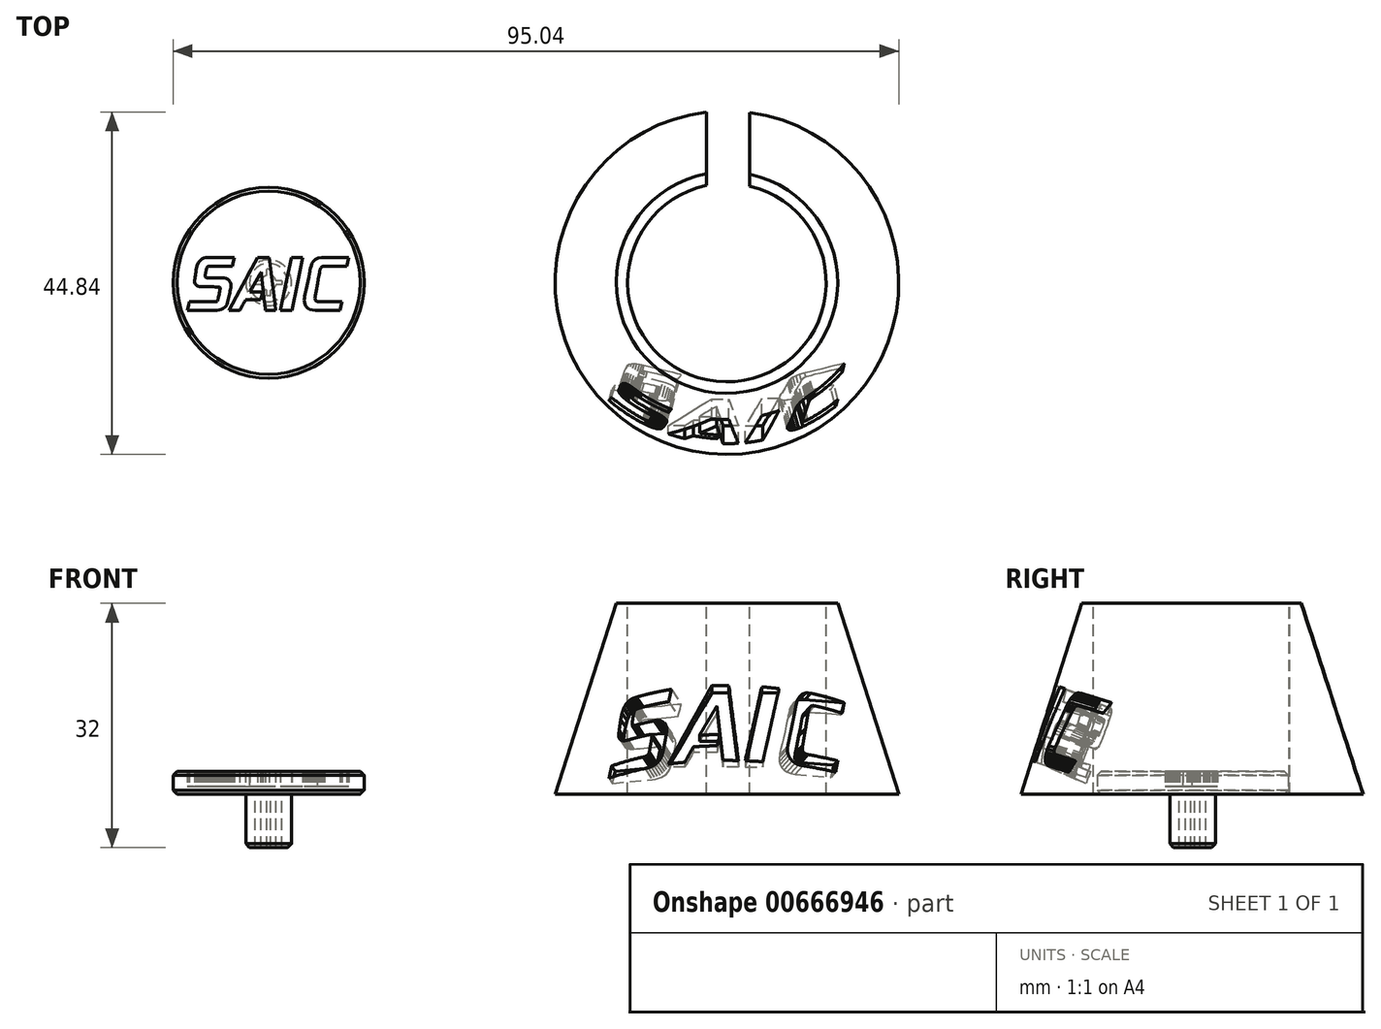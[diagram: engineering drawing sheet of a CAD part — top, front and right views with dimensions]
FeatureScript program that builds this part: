
annotation { "Feature Type Name" : "Feature", "Feature Type Description" : "" }
export const myFeature = defineFeature(function(context is Context, id is Id, definition is map)
    precondition{}
    {
        {
            var Q0;
            Q0=qCreatedBy(makeId("Top.planeOp"),FACE);
            var sketch = newSketch(context, id + "F0", { "sketchPlane" : qUnion([Q0])});
            skCircle(sketch, "E0", {"center": v(0, 0) * mm, "radius": 22.5 * mm});
            skSolve(sketch);
        }
        {
            var Q0;
            Q0=qCreatedBy(makeId("Top.planeOp"),FACE);
            cPlane(context, id + "F1", {"entities" : qUnion([Q0]), "cplaneType" : CPlaneType.OFFSET, "offset" : 25 * mm, "width" : 150 * mm, "height" : 150 * mm});
        }
        {
            var Q0;
            Q0=qCreatedBy(id+"F1.planeOp",FACE);
            var sketch = newSketch(context, id + "F2", { "sketchPlane" : qUnion([Q0])});
            skCircle(sketch, "E1", {"center": v(0, 0) * mm, "radius": 14.5 * mm});
            skSolve(sketch);
        }
        {
            var Q0;
            Q0=makeQuery(id+"F2.imprint","IMPRINT",FACE,{"disambiguationData":[TD([[makeQuery(id+"F2.imprint","IMPRINT",EDGE,{"derivedFrom":sQuery(id+"F2.wireOp",EDGE,"E1")}),1.0]])]});
            var Q1;
            Q1=makeQuery(id+"F0.imprint","IMPRINT",FACE,{"disambiguationData":[TD([[makeQuery(id+"F0.imprint","IMPRINT",EDGE,{"derivedFrom":sQuery(id+"F0.wireOp",EDGE,"E0")}),1.0]])]});
            loft(context, id + "F3", {"sheetProfilesArray" : [{ "sheetProfileEntities" : qUnion([Q0]) }, { "sheetProfileEntities" : qUnion([Q1]) }]});
        }
        {
            var Q0;
            Q0=qCreatedBy(id+"F1.planeOp",FACE);
            var sketch = newSketch(context, id + "F4", { "sketchPlane" : qUnion([Q0])});
            skCircle(sketch, "E2", {"center": v(0, 0) * mm, "radius": 13 * mm});
            skSolve(sketch);
        }
        {
            var Q0;
            Q0 = qSketchRegion(id + "F4", true);
            extrude(context, id + "F5", {"entities" : qUnion([Q0]), "operationType" : NewBodyOperationType.REMOVE, "oppositeDirection" : true, "depth" : 32.3 * mm, "offsetDistance" : 25 * mm});
        }
        {
            var Q0;
            Q0=qCreatedBy(makeId("Top.planeOp"),FACE);
            var sketch = newSketch(context, id + "F6", { "sketchPlane" : qUnion([Q0])});
            skLineSegment(sketch, "E3.bottom", {"start": v(-2.67, 29.37) * mm, "end": v(2.99, 29.37) * mm});
            skLineSegment(sketch, "E3.top", {"start": v(-2.67, 0) * mm, "end": v(2.99, 0) * mm});
            skLineSegment(sketch, "E3.left", {"start": v(-2.67, 0) * mm, "end": v(-2.67, 29.37) * mm});
            skLineSegment(sketch, "E3.right", {"start": v(2.99, 0) * mm, "end": v(2.99, 29.37) * mm});
            skSolve(sketch);
        }
        {
            var Q0;
            Q0 = qSketchRegion(id + "F6", true);
            extrude(context, id + "F7", {"entities" : qUnion([Q0]), "operationType" : NewBodyOperationType.REMOVE, "depth" : 25 * mm, "offsetDistance" : 25 * mm});
        }
        {
            var Q0;
            Q0=qCreatedBy(makeId("Front.planeOp"),FACE);
            var sketch = newSketch(context, id + "F8", { "sketchPlane" : qUnion([Q0])});
            skLineSegment(sketch, "E4", {"start": v(33.86, 8.65) * mm, "end": v(33.95, 9.1) * mm});
            skLineSegment(sketch, "E5", {"start": v(33.95, 9.1) * mm, "end": v(34.07, 9.59) * mm});
            skLineSegment(sketch, "E6", {"start": v(34.07, 9.59) * mm, "end": v(34.25, 10.1) * mm});
            skLineSegment(sketch, "E7", {"start": v(34.25, 10.1) * mm, "end": v(34.5, 10.58) * mm});
            skLineSegment(sketch, "E8", {"start": v(34.5, 10.58) * mm, "end": v(34.88, 11.02) * mm});
            skLineSegment(sketch, "E9", {"start": v(34.88, 11.02) * mm, "end": v(35.38, 11.37) * mm});
            skLineSegment(sketch, "E10", {"start": v(35.38, 11.37) * mm, "end": v(36.04, 11.6) * mm});
            skLineSegment(sketch, "E11", {"start": v(36.04, 11.6) * mm, "end": v(36.88, 11.7) * mm});
            skLineSegment(sketch, "E12", {"start": v(36.88, 11.7) * mm, "end": v(37.88, 11.7) * mm});
            skLineSegment(sketch, "E13", {"start": v(37.88, 11.7) * mm, "end": v(39.7, 11.7) * mm});
            skLineSegment(sketch, "E14", {"start": v(39.7, 11.7) * mm, "end": v(42.05, 11.7) * mm});
            skLineSegment(sketch, "E15", {"start": v(42.05, 11.7) * mm, "end": v(44.63, 11.7) * mm});
            skLineSegment(sketch, "E16", {"start": v(44.63, 11.7) * mm, "end": v(47.15, 11.7) * mm});
            skLineSegment(sketch, "E17", {"start": v(47.15, 11.7) * mm, "end": v(49.32, 11.7) * mm});
            skLineSegment(sketch, "E18", {"start": v(49.32, 11.7) * mm, "end": v(50.83, 11.7) * mm});
            skLineSegment(sketch, "E19", {"start": v(50.83, 11.7) * mm, "end": v(51.4, 11.7) * mm});
            skLineSegment(sketch, "E20", {"start": v(51.4, 11.7) * mm, "end": v(51.57, 12.38) * mm});
            skLineSegment(sketch, "E21", {"start": v(51.57, 12.38) * mm, "end": v(51.73, 13.07) * mm});
            skLineSegment(sketch, "E22", {"start": v(51.73, 13.07) * mm, "end": v(51.9, 13.76) * mm});
            skLineSegment(sketch, "E23", {"start": v(51.9, 13.76) * mm, "end": v(52.07, 14.45) * mm});
            skLineSegment(sketch, "E24", {"start": v(52.07, 14.45) * mm, "end": v(52.23, 15.14) * mm});
            skLineSegment(sketch, "E25", {"start": v(52.23, 15.14) * mm, "end": v(52.4, 15.83) * mm});
            skLineSegment(sketch, "E26", {"start": v(52.4, 15.83) * mm, "end": v(52.56, 16.52) * mm});
            skLineSegment(sketch, "E27", {"start": v(52.56, 16.52) * mm, "end": v(52.73, 17.2) * mm});
            skLineSegment(sketch, "E28", {"start": v(52.73, 17.2) * mm, "end": v(52.16, 17.2) * mm});
            skLineSegment(sketch, "E29", {"start": v(52.16, 17.2) * mm, "end": v(50.64, 17.2) * mm});
            skLineSegment(sketch, "E30", {"start": v(50.64, 17.2) * mm, "end": v(48.4, 17.2) * mm});
            skLineSegment(sketch, "E31", {"start": v(48.4, 17.2) * mm, "end": v(45.68, 17.2) * mm});
            skLineSegment(sketch, "E32", {"start": v(45.68, 17.2) * mm, "end": v(42.74, 17.2) * mm});
            skLineSegment(sketch, "E33", {"start": v(42.74, 17.2) * mm, "end": v(39.81, 17.2) * mm});
            skLineSegment(sketch, "E34", {"start": v(39.81, 17.2) * mm, "end": v(37.15, 17.2) * mm});
            skLineSegment(sketch, "E35", {"start": v(37.15, 17.2) * mm, "end": v(35, 17.2) * mm});
            skLineSegment(sketch, "E36", {"start": v(35, 17.2) * mm, "end": v(32.75, 16.9) * mm});
            skLineSegment(sketch, "E37", {"start": v(32.75, 16.9) * mm, "end": v(31.02, 16.1) * mm});
            skLineSegment(sketch, "E38", {"start": v(31.02, 16.1) * mm, "end": v(29.74, 14.92) * mm});
            skLineSegment(sketch, "E39", {"start": v(29.74, 14.92) * mm, "end": v(28.83, 13.5) * mm});
            skLineSegment(sketch, "E40", {"start": v(28.83, 13.5) * mm, "end": v(28.2, 11.98) * mm});
            skLineSegment(sketch, "E41", {"start": v(28.2, 11.98) * mm, "end": v(27.81, 10.48) * mm});
            skLineSegment(sketch, "E42", {"start": v(27.81, 10.48) * mm, "end": v(27.57, 9.14) * mm});
            skLineSegment(sketch, "E43", {"start": v(27.57, 9.14) * mm, "end": v(27.4, 8.1) * mm});
            skLineSegment(sketch, "E44", {"start": v(27.4, 8.1) * mm, "end": v(27.12, 6.75) * mm});
            skLineSegment(sketch, "E45", {"start": v(27.12, 6.75) * mm, "end": v(26.67, 4.57) * mm});
            skLineSegment(sketch, "E46", {"start": v(26.67, 4.57) * mm, "end": v(26.1, 1.88) * mm});
            skLineSegment(sketch, "E47", {"start": v(26.1, 1.88) * mm, "end": v(25.49, -1.04) * mm});
            skLineSegment(sketch, "E48", {"start": v(25.49, -1.04) * mm, "end": v(24.88, -3.87) * mm});
            skLineSegment(sketch, "E49", {"start": v(24.88, -3.87) * mm, "end": v(24.36, -6.34) * mm});
            skLineSegment(sketch, "E50", {"start": v(24.36, -6.34) * mm, "end": v(23.98, -8.13) * mm});
            skLineSegment(sketch, "E51", {"start": v(23.98, -8.13) * mm, "end": v(23.81, -8.95) * mm});
            skLineSegment(sketch, "E52", {"start": v(23.81, -8.95) * mm, "end": v(23.65, -10.47) * mm});
            skLineSegment(sketch, "E53", {"start": v(23.65, -10.47) * mm, "end": v(23.76, -11.94) * mm});
            skLineSegment(sketch, "E54", {"start": v(23.76, -11.94) * mm, "end": v(24.17, -13.34) * mm});
            skLineSegment(sketch, "E55", {"start": v(24.17, -13.34) * mm, "end": v(24.87, -14.6) * mm});
            skLineSegment(sketch, "E56", {"start": v(24.87, -14.6) * mm, "end": v(25.88, -15.67) * mm});
            skLineSegment(sketch, "E57", {"start": v(25.88, -15.67) * mm, "end": v(27.22, -16.5) * mm});
            skLineSegment(sketch, "E58", {"start": v(27.22, -16.5) * mm, "end": v(28.89, -17.03) * mm});
            skLineSegment(sketch, "E59", {"start": v(28.89, -17.03) * mm, "end": v(30.9, -17.22) * mm});
            skLineSegment(sketch, "E60", {"start": v(30.9, -17.22) * mm, "end": v(32.92, -17.22) * mm});
            skLineSegment(sketch, "E61", {"start": v(32.92, -17.22) * mm, "end": v(34.94, -17.22) * mm});
            skLineSegment(sketch, "E62", {"start": v(34.94, -17.22) * mm, "end": v(36.96, -17.22) * mm});
            skLineSegment(sketch, "E63", {"start": v(36.96, -17.22) * mm, "end": v(38.98, -17.22) * mm});
            skLineSegment(sketch, "E64", {"start": v(38.98, -17.22) * mm, "end": v(41, -17.22) * mm});
            skLineSegment(sketch, "E65", {"start": v(41, -17.22) * mm, "end": v(43.02, -17.22) * mm});
            skLineSegment(sketch, "E66", {"start": v(43.02, -17.22) * mm, "end": v(45.04, -17.22) * mm});
            skLineSegment(sketch, "E67", {"start": v(45.04, -17.22) * mm, "end": v(47.06, -17.22) * mm});
            skLineSegment(sketch, "E68", {"start": v(47.06, -17.22) * mm, "end": v(47.22, -16.53) * mm});
            skLineSegment(sketch, "E69", {"start": v(47.22, -16.53) * mm, "end": v(47.37, -15.83) * mm});
            skLineSegment(sketch, "E70", {"start": v(47.37, -15.83) * mm, "end": v(47.52, -15.14) * mm});
            skLineSegment(sketch, "E71", {"start": v(47.52, -15.14) * mm, "end": v(47.68, -14.44) * mm});
            skLineSegment(sketch, "E72", {"start": v(47.68, -14.44) * mm, "end": v(47.83, -13.75) * mm});
            skLineSegment(sketch, "E73", {"start": v(47.83, -13.75) * mm, "end": v(47.98, -13.06) * mm});
            skLineSegment(sketch, "E74", {"start": v(47.98, -13.06) * mm, "end": v(48.14, -12.36) * mm});
            skLineSegment(sketch, "E75", {"start": v(48.14, -12.36) * mm, "end": v(48.29, -11.67) * mm});
            skLineSegment(sketch, "E76", {"start": v(48.29, -11.67) * mm, "end": v(46.43, -11.67) * mm});
            skLineSegment(sketch, "E77", {"start": v(46.43, -11.67) * mm, "end": v(44.57, -11.67) * mm});
            skLineSegment(sketch, "E78", {"start": v(44.57, -11.67) * mm, "end": v(42.71, -11.67) * mm});
            skLineSegment(sketch, "E79", {"start": v(42.71, -11.67) * mm, "end": v(40.85, -11.67) * mm});
            skLineSegment(sketch, "E80", {"start": v(40.85, -11.67) * mm, "end": v(39, -11.67) * mm});
            skLineSegment(sketch, "E81", {"start": v(39, -11.67) * mm, "end": v(37.14, -11.67) * mm});
            skLineSegment(sketch, "E82", {"start": v(37.14, -11.67) * mm, "end": v(35.28, -11.67) * mm});
            skLineSegment(sketch, "E83", {"start": v(35.28, -11.67) * mm, "end": v(33.42, -11.67) * mm});
            skLineSegment(sketch, "E84", {"start": v(33.42, -11.67) * mm, "end": v(32.47, -11.59) * mm});
            skLineSegment(sketch, "E85", {"start": v(32.47, -11.59) * mm, "end": v(31.76, -11.36) * mm});
            skLineSegment(sketch, "E86", {"start": v(31.76, -11.36) * mm, "end": v(31.26, -10.99) * mm});
            skLineSegment(sketch, "E87", {"start": v(31.26, -10.99) * mm, "end": v(30.93, -10.5) * mm});
            skLineSegment(sketch, "E88", {"start": v(30.93, -10.5) * mm, "end": v(30.76, -9.9) * mm});
            skLineSegment(sketch, "E89", {"start": v(30.76, -9.9) * mm, "end": v(30.72, -9.22) * mm});
            skLineSegment(sketch, "E90", {"start": v(30.72, -9.22) * mm, "end": v(30.77, -8.46) * mm});
            skLineSegment(sketch, "E91", {"start": v(30.77, -8.46) * mm, "end": v(30.9, -7.65) * mm});
            skLineSegment(sketch, "E92", {"start": v(30.9, -7.65) * mm, "end": v(31.09, -6.63) * mm});
            skLineSegment(sketch, "E93", {"start": v(31.09, -6.63) * mm, "end": v(31.27, -5.61) * mm});
            skLineSegment(sketch, "E94", {"start": v(31.27, -5.61) * mm, "end": v(31.45, -4.6) * mm});
            skLineSegment(sketch, "E95", {"start": v(31.45, -4.6) * mm, "end": v(31.64, -3.58) * mm});
            skLineSegment(sketch, "E96", {"start": v(31.64, -3.58) * mm, "end": v(31.82, -2.57) * mm});
            skLineSegment(sketch, "E97", {"start": v(31.82, -2.57) * mm, "end": v(32, -1.55) * mm});
            skLineSegment(sketch, "E98", {"start": v(32, -1.55) * mm, "end": v(32.19, -0.54) * mm});
            skLineSegment(sketch, "E99", {"start": v(32.19, -0.54) * mm, "end": v(32.37, 0.48) * mm});
            skLineSegment(sketch, "E100", {"start": v(32.37, 0.48) * mm, "end": v(32.37, 0.48) * mm});
            skLineSegment(sketch, "E101", {"start": v(32.37, 0.48) * mm, "end": v(32.38, 0.48) * mm});
            skLineSegment(sketch, "E102", {"start": v(32.38, 0.48) * mm, "end": v(32.38, 0.48) * mm});
            skLineSegment(sketch, "E103", {"start": v(32.38, 0.48) * mm, "end": v(32.42, 0.7) * mm});
            skLineSegment(sketch, "E104", {"start": v(32.42, 0.7) * mm, "end": v(32.52, 1.3) * mm});
            skLineSegment(sketch, "E105", {"start": v(32.52, 1.3) * mm, "end": v(32.67, 2.22) * mm});
            skLineSegment(sketch, "E106", {"start": v(32.67, 2.22) * mm, "end": v(32.87, 3.36) * mm});
            skLineSegment(sketch, "E107", {"start": v(32.87, 3.36) * mm, "end": v(33.1, 4.66) * mm});
            skLineSegment(sketch, "E108", {"start": v(33.1, 4.66) * mm, "end": v(33.35, 6.02) * mm});
            skLineSegment(sketch, "E109", {"start": v(33.35, 6.02) * mm, "end": v(33.6, 7.38) * mm});
            skLineSegment(sketch, "E110", {"start": v(33.6, 7.38) * mm, "end": v(33.86, 8.65) * mm});
            skLineSegment(sketch, "E111", {"start": v(22.75, 17.21) * mm, "end": v(21.8, 17.21) * mm});
            skLineSegment(sketch, "E112", {"start": v(21.8, 17.21) * mm, "end": v(20.87, 17.21) * mm});
            skLineSegment(sketch, "E113", {"start": v(20.87, 17.21) * mm, "end": v(19.93, 17.21) * mm});
            skLineSegment(sketch, "E114", {"start": v(19.93, 17.21) * mm, "end": v(18.99, 17.21) * mm});
            skLineSegment(sketch, "E115", {"start": v(18.99, 17.21) * mm, "end": v(18.05, 17.21) * mm});
            skLineSegment(sketch, "E116", {"start": v(18.05, 17.21) * mm, "end": v(17.1, 17.21) * mm});
            skLineSegment(sketch, "E117", {"start": v(17.1, 17.21) * mm, "end": v(16.17, 17.21) * mm});
            skLineSegment(sketch, "E118", {"start": v(16.17, 17.21) * mm, "end": v(15.23, 17.21) * mm});
            skLineSegment(sketch, "E119", {"start": v(15.23, 17.21) * mm, "end": v(14.32, 12.91) * mm});
            skLineSegment(sketch, "E120", {"start": v(14.32, 12.91) * mm, "end": v(13.42, 8.6) * mm});
            skLineSegment(sketch, "E121", {"start": v(13.42, 8.6) * mm, "end": v(12.51, 4.3) * mm});
            skLineSegment(sketch, "E122", {"start": v(12.51, 4.3) * mm, "end": v(11.6, 0) * mm});
            skLineSegment(sketch, "E123", {"start": v(11.6, 0) * mm, "end": v(10.7, -4.3) * mm});
            skLineSegment(sketch, "E124", {"start": v(10.7, -4.3) * mm, "end": v(9.8, -8.6) * mm});
            skLineSegment(sketch, "E125", {"start": v(9.8, -8.6) * mm, "end": v(8.9, -12.9) * mm});
            skLineSegment(sketch, "E126", {"start": v(8.9, -12.9) * mm, "end": v(7.99, -17.2) * mm});
            skLineSegment(sketch, "E127", {"start": v(7.99, -17.2) * mm, "end": v(8.94, -17.2) * mm});
            skLineSegment(sketch, "E128", {"start": v(8.94, -17.2) * mm, "end": v(9.9, -17.2) * mm});
            skLineSegment(sketch, "E129", {"start": v(9.9, -17.2) * mm, "end": v(10.86, -17.2) * mm});
            skLineSegment(sketch, "E130", {"start": v(10.86, -17.2) * mm, "end": v(11.81, -17.2) * mm});
            skLineSegment(sketch, "E131", {"start": v(11.81, -17.2) * mm, "end": v(12.77, -17.2) * mm});
            skLineSegment(sketch, "E132", {"start": v(12.77, -17.2) * mm, "end": v(13.73, -17.2) * mm});
            skLineSegment(sketch, "E133", {"start": v(13.73, -17.2) * mm, "end": v(14.68, -17.2) * mm});
            skLineSegment(sketch, "E134", {"start": v(14.68, -17.2) * mm, "end": v(15.64, -17.2) * mm});
            skLineSegment(sketch, "E135", {"start": v(15.64, -17.2) * mm, "end": v(16.53, -12.9) * mm});
            skLineSegment(sketch, "E136", {"start": v(16.53, -12.9) * mm, "end": v(17.42, -8.6) * mm});
            skLineSegment(sketch, "E137", {"start": v(17.42, -8.6) * mm, "end": v(18.3, -4.3) * mm});
            skLineSegment(sketch, "E138", {"start": v(18.3, -4.3) * mm, "end": v(19.2, 0) * mm});
            skLineSegment(sketch, "E139", {"start": v(19.2, 0) * mm, "end": v(20.08, 4.3) * mm});
            skLineSegment(sketch, "E140", {"start": v(20.08, 4.3) * mm, "end": v(20.97, 8.6) * mm});
            skLineSegment(sketch, "E141", {"start": v(20.97, 8.6) * mm, "end": v(21.86, 12.91) * mm});
            skLineSegment(sketch, "E142", {"start": v(21.86, 12.91) * mm, "end": v(22.75, 17.21) * mm});
            skLineSegment(sketch, "E143", {"start": v(-4.42, 7.79) * mm, "end": v(-4.76, 7.19) * mm});
            skLineSegment(sketch, "E144", {"start": v(-4.76, 7.19) * mm, "end": v(-5.58, 5.78) * mm});
            skLineSegment(sketch, "E145", {"start": v(-5.58, 5.78) * mm, "end": v(-6.72, 3.81) * mm});
            skLineSegment(sketch, "E146", {"start": v(-6.72, 3.81) * mm, "end": v(-8.03, 1.55) * mm});
            skLineSegment(sketch, "E147", {"start": v(-8.03, 1.55) * mm, "end": v(-9.37, -0.75) * mm});
            skLineSegment(sketch, "E148", {"start": v(-9.37, -0.75) * mm, "end": v(-10.57, -2.83) * mm});
            skLineSegment(sketch, "E149", {"start": v(-10.57, -2.83) * mm, "end": v(-11.5, -4.42) * mm});
            skLineSegment(sketch, "E150", {"start": v(-11.5, -4.42) * mm, "end": v(-12, -5.27) * mm});
            skLineSegment(sketch, "E151", {"start": v(-12, -5.27) * mm, "end": v(-12, -5.27) * mm});
            skLineSegment(sketch, "E152", {"start": v(-12, -5.27) * mm, "end": v(-12, -5.28) * mm});
            skLineSegment(sketch, "E153", {"start": v(-12, -5.28) * mm, "end": v(-11.99, -5.28) * mm});
            skLineSegment(sketch, "E154", {"start": v(-11.99, -5.28) * mm, "end": v(-11.99, -5.28) * mm});
            skLineSegment(sketch, "E155", {"start": v(-11.99, -5.28) * mm, "end": v(-11.98, -5.28) * mm});
            skLineSegment(sketch, "E156", {"start": v(-11.98, -5.28) * mm, "end": v(-11.98, -5.28) * mm});
            skLineSegment(sketch, "E157", {"start": v(-11.98, -5.28) * mm, "end": v(-11.63, -5.28) * mm});
            skLineSegment(sketch, "E158", {"start": v(-11.63, -5.28) * mm, "end": v(-11.43, -5.28) * mm});
            skLineSegment(sketch, "E159", {"start": v(-11.43, -5.28) * mm, "end": v(-11.18, -5.28) * mm});
            skLineSegment(sketch, "E160", {"start": v(-11.18, -5.28) * mm, "end": v(-10.71, -5.28) * mm});
            skLineSegment(sketch, "E161", {"start": v(-10.71, -5.28) * mm, "end": v(-9.85, -5.28) * mm});
            skLineSegment(sketch, "E162", {"start": v(-9.85, -5.28) * mm, "end": v(-8.41, -5.28) * mm});
            skLineSegment(sketch, "E163", {"start": v(-8.41, -5.28) * mm, "end": v(-6.23, -5.28) * mm});
            skLineSegment(sketch, "E164", {"start": v(-6.23, -5.28) * mm, "end": v(-3.11, -5.28) * mm});
            skLineSegment(sketch, "E165", {"start": v(-3.11, -5.28) * mm, "end": v(-3.25, -5.92) * mm});
            skLineSegment(sketch, "E166", {"start": v(-3.25, -5.92) * mm, "end": v(-3.4, -6.56) * mm});
            skLineSegment(sketch, "E167", {"start": v(-3.4, -6.56) * mm, "end": v(-3.54, -7.2) * mm});
            skLineSegment(sketch, "E168", {"start": v(-3.54, -7.2) * mm, "end": v(-3.68, -7.84) * mm});
            skLineSegment(sketch, "E169", {"start": v(-3.68, -7.84) * mm, "end": v(-3.82, -8.48) * mm});
            skLineSegment(sketch, "E170", {"start": v(-3.82, -8.48) * mm, "end": v(-3.96, -9.12) * mm});
            skLineSegment(sketch, "E171", {"start": v(-3.96, -9.12) * mm, "end": v(-4.1, -9.76) * mm});
            skLineSegment(sketch, "E172", {"start": v(-4.1, -9.76) * mm, "end": v(-4.25, -10.4) * mm});
            skLineSegment(sketch, "E173", {"start": v(-4.25, -10.4) * mm, "end": v(-4.68, -10.4) * mm});
            skLineSegment(sketch, "E174", {"start": v(-4.68, -10.4) * mm, "end": v(-5.83, -10.4) * mm});
            skLineSegment(sketch, "E175", {"start": v(-5.83, -10.4) * mm, "end": v(-7.45, -10.4) * mm});
            skLineSegment(sketch, "E176", {"start": v(-7.45, -10.4) * mm, "end": v(-9.32, -10.4) * mm});
            skLineSegment(sketch, "E177", {"start": v(-9.32, -10.4) * mm, "end": v(-11.21, -10.4) * mm});
            skLineSegment(sketch, "E178", {"start": v(-11.21, -10.4) * mm, "end": v(-12.88, -10.4) * mm});
            skLineSegment(sketch, "E179", {"start": v(-12.88, -10.4) * mm, "end": v(-14.1, -10.4) * mm});
            skLineSegment(sketch, "E180", {"start": v(-14.1, -10.4) * mm, "end": v(-14.64, -10.4) * mm});
            skLineSegment(sketch, "E181", {"start": v(-14.64, -10.4) * mm, "end": v(-14.84, -10.77) * mm});
            skLineSegment(sketch, "E182", {"start": v(-14.84, -10.77) * mm, "end": v(-15.3, -11.58) * mm});
            skLineSegment(sketch, "E183", {"start": v(-15.3, -11.58) * mm, "end": v(-15.9, -12.68) * mm});
            skLineSegment(sketch, "E184", {"start": v(-15.9, -12.68) * mm, "end": v(-16.58, -13.9) * mm});
            skLineSegment(sketch, "E185", {"start": v(-16.58, -13.9) * mm, "end": v(-17.26, -15.12) * mm});
            skLineSegment(sketch, "E186", {"start": v(-17.26, -15.12) * mm, "end": v(-17.85, -16.17) * mm});
            skLineSegment(sketch, "E187", {"start": v(-17.85, -16.17) * mm, "end": v(-18.26, -16.91) * mm});
            skLineSegment(sketch, "E188", {"start": v(-18.26, -16.91) * mm, "end": v(-18.42, -17.2) * mm});
            skLineSegment(sketch, "E189", {"start": v(-18.42, -17.2) * mm, "end": v(-19.32, -17.2) * mm});
            skLineSegment(sketch, "E190", {"start": v(-19.32, -17.2) * mm, "end": v(-20.22, -17.2) * mm});
            skLineSegment(sketch, "E191", {"start": v(-20.22, -17.2) * mm, "end": v(-21.12, -17.2) * mm});
            skLineSegment(sketch, "E192", {"start": v(-21.12, -17.2) * mm, "end": v(-22.02, -17.2) * mm});
            skLineSegment(sketch, "E193", {"start": v(-22.02, -17.2) * mm, "end": v(-22.92, -17.2) * mm});
            skLineSegment(sketch, "E194", {"start": v(-22.92, -17.2) * mm, "end": v(-23.82, -17.2) * mm});
            skLineSegment(sketch, "E195", {"start": v(-23.82, -17.2) * mm, "end": v(-24.72, -17.2) * mm});
            skLineSegment(sketch, "E196", {"start": v(-24.72, -17.2) * mm, "end": v(-25.61, -17.2) * mm});
            skLineSegment(sketch, "E197", {"start": v(-25.61, -17.2) * mm, "end": v(-23.25, -12.9) * mm});
            skLineSegment(sketch, "E198", {"start": v(-23.25, -12.9) * mm, "end": v(-20.88, -8.6) * mm});
            skLineSegment(sketch, "E199", {"start": v(-20.88, -8.6) * mm, "end": v(-18.5, -4.3) * mm});
            skLineSegment(sketch, "E200", {"start": v(-18.5, -4.3) * mm, "end": v(-16.14, 0) * mm});
            skLineSegment(sketch, "E201", {"start": v(-16.14, 0) * mm, "end": v(-13.77, 4.29) * mm});
            skLineSegment(sketch, "E202", {"start": v(-13.77, 4.29) * mm, "end": v(-11.4, 8.58) * mm});
            skLineSegment(sketch, "E203", {"start": v(-11.4, 8.58) * mm, "end": v(-9.03, 12.88) * mm});
            skLineSegment(sketch, "E204", {"start": v(-9.03, 12.88) * mm, "end": v(-6.66, 17.18) * mm});
            skLineSegment(sketch, "E205", {"start": v(-6.66, 17.18) * mm, "end": v(-5.72, 17.18) * mm});
            skLineSegment(sketch, "E206", {"start": v(-5.72, 17.18) * mm, "end": v(-4.78, 17.18) * mm});
            skLineSegment(sketch, "E207", {"start": v(-4.78, 17.18) * mm, "end": v(-3.85, 17.18) * mm});
            skLineSegment(sketch, "E208", {"start": v(-3.85, 17.18) * mm, "end": v(-2.9, 17.18) * mm});
            skLineSegment(sketch, "E209", {"start": v(-2.9, 17.18) * mm, "end": v(-1.97, 17.18) * mm});
            skLineSegment(sketch, "E210", {"start": v(-1.97, 17.18) * mm, "end": v(-1.03, 17.18) * mm});
            skLineSegment(sketch, "E211", {"start": v(-1.03, 17.18) * mm, "end": v(-0.09, 17.18) * mm});
            skLineSegment(sketch, "E212", {"start": v(-0.09, 17.18) * mm, "end": v(0.85, 17.18) * mm});
            skLineSegment(sketch, "E213", {"start": v(0.85, 17.18) * mm, "end": v(1.37, 12.88) * mm});
            skLineSegment(sketch, "E214", {"start": v(1.37, 12.88) * mm, "end": v(1.88, 8.58) * mm});
            skLineSegment(sketch, "E215", {"start": v(1.88, 8.58) * mm, "end": v(2.4, 4.29) * mm});
            skLineSegment(sketch, "E216", {"start": v(2.4, 4.29) * mm, "end": v(2.91, 0) * mm});
            skLineSegment(sketch, "E217", {"start": v(2.91, 0) * mm, "end": v(3.43, -4.3) * mm});
            skLineSegment(sketch, "E218", {"start": v(3.43, -4.3) * mm, "end": v(3.94, -8.6) * mm});
            skLineSegment(sketch, "E219", {"start": v(3.94, -8.6) * mm, "end": v(4.46, -12.9) * mm});
            skLineSegment(sketch, "E220", {"start": v(4.46, -12.9) * mm, "end": v(4.98, -17.2) * mm});
            skLineSegment(sketch, "E221", {"start": v(4.98, -17.2) * mm, "end": v(4.14, -17.2) * mm});
            skLineSegment(sketch, "E222", {"start": v(4.14, -17.2) * mm, "end": v(3.3, -17.2) * mm});
            skLineSegment(sketch, "E223", {"start": v(3.3, -17.2) * mm, "end": v(2.46, -17.2) * mm});
            skLineSegment(sketch, "E224", {"start": v(2.46, -17.2) * mm, "end": v(1.62, -17.2) * mm});
            skLineSegment(sketch, "E225", {"start": v(1.62, -17.2) * mm, "end": v(0.79, -17.2) * mm});
            skLineSegment(sketch, "E226", {"start": v(0.79, -17.2) * mm, "end": v(-0.05, -17.2) * mm});
            skLineSegment(sketch, "E227", {"start": v(-0.05, -17.2) * mm, "end": v(-0.89, -17.2) * mm});
            skLineSegment(sketch, "E228", {"start": v(-0.89, -17.2) * mm, "end": v(-1.73, -17.2) * mm});
            skLineSegment(sketch, "E229", {"start": v(-1.73, -17.2) * mm, "end": v(-1.84, -16.13) * mm});
            skLineSegment(sketch, "E230", {"start": v(-1.84, -16.13) * mm, "end": v(-2.14, -13.33) * mm});
            skLineSegment(sketch, "E231", {"start": v(-2.14, -13.33) * mm, "end": v(-2.57, -9.35) * mm});
            skLineSegment(sketch, "E232", {"start": v(-2.57, -9.35) * mm, "end": v(-3.06, -4.8) * mm});
            skLineSegment(sketch, "E233", {"start": v(-3.06, -4.8) * mm, "end": v(-3.55, -0.22) * mm});
            skLineSegment(sketch, "E234", {"start": v(-3.55, -0.22) * mm, "end": v(-3.98, 3.78) * mm});
            skLineSegment(sketch, "E235", {"start": v(-3.98, 3.78) * mm, "end": v(-4.3, 6.64) * mm});
            skLineSegment(sketch, "E236", {"start": v(-4.3, 6.64) * mm, "end": v(-4.42, 7.79) * mm});
            skLineSegment(sketch, "E237", {"start": v(-40.51, 8.53) * mm, "end": v(-40.36, 9.35) * mm});
            skLineSegment(sketch, "E238", {"start": v(-40.36, 9.35) * mm, "end": v(-40.23, 10.03) * mm});
            skLineSegment(sketch, "E239", {"start": v(-40.23, 10.03) * mm, "end": v(-40.08, 10.58) * mm});
            skLineSegment(sketch, "E240", {"start": v(-40.08, 10.58) * mm, "end": v(-39.84, 11.01) * mm});
            skLineSegment(sketch, "E241", {"start": v(-39.84, 11.01) * mm, "end": v(-39.47, 11.33) * mm});
            skLineSegment(sketch, "E242", {"start": v(-39.47, 11.33) * mm, "end": v(-38.92, 11.54) * mm});
            skLineSegment(sketch, "E243", {"start": v(-38.92, 11.54) * mm, "end": v(-38.13, 11.66) * mm});
            skLineSegment(sketch, "E244", {"start": v(-38.13, 11.66) * mm, "end": v(-37.06, 11.7) * mm});
            skLineSegment(sketch, "E245", {"start": v(-37.06, 11.7) * mm, "end": v(-35.22, 11.7) * mm});
            skLineSegment(sketch, "E246", {"start": v(-35.22, 11.7) * mm, "end": v(-33.06, 11.7) * mm});
            skLineSegment(sketch, "E247", {"start": v(-33.06, 11.7) * mm, "end": v(-30.77, 11.7) * mm});
            skLineSegment(sketch, "E248", {"start": v(-30.77, 11.7) * mm, "end": v(-28.51, 11.7) * mm});
            skLineSegment(sketch, "E249", {"start": v(-28.51, 11.7) * mm, "end": v(-26.46, 11.7) * mm});
            skLineSegment(sketch, "E250", {"start": v(-26.46, 11.7) * mm, "end": v(-24.78, 11.69) * mm});
            skLineSegment(sketch, "E251", {"start": v(-24.78, 11.69) * mm, "end": v(-23.64, 11.69) * mm});
            skLineSegment(sketch, "E252", {"start": v(-23.64, 11.69) * mm, "end": v(-23.23, 11.69) * mm});
            skLineSegment(sketch, "E253", {"start": v(-23.23, 11.69) * mm, "end": v(-23.06, 12.38) * mm});
            skLineSegment(sketch, "E254", {"start": v(-23.06, 12.38) * mm, "end": v(-22.9, 13.07) * mm});
            skLineSegment(sketch, "E255", {"start": v(-22.9, 13.07) * mm, "end": v(-22.72, 13.76) * mm});
            skLineSegment(sketch, "E256", {"start": v(-22.72, 13.76) * mm, "end": v(-22.56, 14.45) * mm});
            skLineSegment(sketch, "E257", {"start": v(-22.56, 14.45) * mm, "end": v(-22.4, 15.14) * mm});
            skLineSegment(sketch, "E258", {"start": v(-22.4, 15.14) * mm, "end": v(-22.22, 15.83) * mm});
            skLineSegment(sketch, "E259", {"start": v(-22.22, 15.83) * mm, "end": v(-22.06, 16.52) * mm});
            skLineSegment(sketch, "E260", {"start": v(-22.06, 16.52) * mm, "end": v(-21.89, 17.21) * mm});
            skLineSegment(sketch, "E261", {"start": v(-21.89, 17.21) * mm, "end": v(-22.35, 17.21) * mm});
            skLineSegment(sketch, "E262", {"start": v(-22.35, 17.21) * mm, "end": v(-23.61, 17.21) * mm});
            skLineSegment(sketch, "E263", {"start": v(-23.61, 17.21) * mm, "end": v(-25.52, 17.21) * mm});
            skLineSegment(sketch, "E264", {"start": v(-25.52, 17.21) * mm, "end": v(-27.89, 17.21) * mm});
            skLineSegment(sketch, "E265", {"start": v(-27.89, 17.21) * mm, "end": v(-30.56, 17.21) * mm});
            skLineSegment(sketch, "E266", {"start": v(-30.56, 17.21) * mm, "end": v(-33.36, 17.21) * mm});
            skLineSegment(sketch, "E267", {"start": v(-33.36, 17.21) * mm, "end": v(-36.12, 17.2) * mm});
            skLineSegment(sketch, "E268", {"start": v(-36.12, 17.2) * mm, "end": v(-38.68, 17.2) * mm});
            skLineSegment(sketch, "E269", {"start": v(-38.68, 17.2) * mm, "end": v(-39.6, 17.22) * mm});
            skLineSegment(sketch, "E270", {"start": v(-39.6, 17.22) * mm, "end": v(-40.71, 17.17) * mm});
            skLineSegment(sketch, "E271", {"start": v(-40.71, 17.17) * mm, "end": v(-41.91, 16.95) * mm});
            skLineSegment(sketch, "E272", {"start": v(-41.91, 16.95) * mm, "end": v(-43.15, 16.44) * mm});
            skLineSegment(sketch, "E273", {"start": v(-43.15, 16.44) * mm, "end": v(-44.34, 15.5) * mm});
            skLineSegment(sketch, "E274", {"start": v(-44.34, 15.5) * mm, "end": v(-45.42, 14.05) * mm});
            skLineSegment(sketch, "E275", {"start": v(-45.42, 14.05) * mm, "end": v(-46.31, 11.93) * mm});
            skLineSegment(sketch, "E276", {"start": v(-46.31, 11.93) * mm, "end": v(-46.95, 9.05) * mm});
            skLineSegment(sketch, "E277", {"start": v(-46.95, 9.05) * mm, "end": v(-47.15, 7.72) * mm});
            skLineSegment(sketch, "E278", {"start": v(-47.15, 7.72) * mm, "end": v(-47.33, 6.55) * mm});
            skLineSegment(sketch, "E279", {"start": v(-47.33, 6.55) * mm, "end": v(-47.48, 5.53) * mm});
            skLineSegment(sketch, "E280", {"start": v(-47.48, 5.53) * mm, "end": v(-47.61, 4.64) * mm});
            skLineSegment(sketch, "E281", {"start": v(-47.61, 4.64) * mm, "end": v(-47.72, 3.88) * mm});
            skLineSegment(sketch, "E282", {"start": v(-47.72, 3.88) * mm, "end": v(-47.8, 3.22) * mm});
            skLineSegment(sketch, "E283", {"start": v(-47.8, 3.22) * mm, "end": v(-47.87, 2.65) * mm});
            skLineSegment(sketch, "E284", {"start": v(-47.87, 2.65) * mm, "end": v(-47.91, 2.16) * mm});
            skLineSegment(sketch, "E285", {"start": v(-47.91, 2.16) * mm, "end": v(-47.86, 1.1) * mm});
            skLineSegment(sketch, "E286", {"start": v(-47.86, 1.1) * mm, "end": v(-47.57, 0.23) * mm});
            skLineSegment(sketch, "E287", {"start": v(-47.57, 0.23) * mm, "end": v(-47.09, -0.47) * mm});
            skLineSegment(sketch, "E288", {"start": v(-47.09, -0.47) * mm, "end": v(-46.45, -1.01) * mm});
            skLineSegment(sketch, "E289", {"start": v(-46.45, -1.01) * mm, "end": v(-45.7, -1.4) * mm});
            skLineSegment(sketch, "E290", {"start": v(-45.7, -1.4) * mm, "end": v(-44.86, -1.67) * mm});
            skLineSegment(sketch, "E291", {"start": v(-44.86, -1.67) * mm, "end": v(-43.98, -1.82) * mm});
            skLineSegment(sketch, "E292", {"start": v(-43.98, -1.82) * mm, "end": v(-43.11, -1.87) * mm});
            skLineSegment(sketch, "E293", {"start": v(-43.11, -1.87) * mm, "end": v(-41.8, -1.87) * mm});
            skLineSegment(sketch, "E294", {"start": v(-41.8, -1.87) * mm, "end": v(-40.26, -1.87) * mm});
            skLineSegment(sketch, "E295", {"start": v(-40.26, -1.87) * mm, "end": v(-38.6, -1.87) * mm});
            skLineSegment(sketch, "E296", {"start": v(-38.6, -1.87) * mm, "end": v(-36.98, -1.87) * mm});
            skLineSegment(sketch, "E297", {"start": v(-36.98, -1.87) * mm, "end": v(-35.5, -1.87) * mm});
            skLineSegment(sketch, "E298", {"start": v(-35.5, -1.87) * mm, "end": v(-34.29, -1.87) * mm});
            skLineSegment(sketch, "E299", {"start": v(-34.29, -1.87) * mm, "end": v(-33.47, -1.87) * mm});
            skLineSegment(sketch, "E300", {"start": v(-33.47, -1.87) * mm, "end": v(-33.16, -1.87) * mm});
            skLineSegment(sketch, "E301", {"start": v(-33.16, -1.87) * mm, "end": v(-32.64, -1.87) * mm});
            skLineSegment(sketch, "E302", {"start": v(-32.64, -1.87) * mm, "end": v(-32.2, -1.89) * mm});
            skLineSegment(sketch, "E303", {"start": v(-32.2, -1.89) * mm, "end": v(-31.85, -1.93) * mm});
            skLineSegment(sketch, "E304", {"start": v(-31.85, -1.93) * mm, "end": v(-31.57, -2.01) * mm});
            skLineSegment(sketch, "E305", {"start": v(-31.57, -2.01) * mm, "end": v(-31.37, -2.15) * mm});
            skLineSegment(sketch, "E306", {"start": v(-31.37, -2.15) * mm, "end": v(-31.26, -2.35) * mm});
            skLineSegment(sketch, "E307", {"start": v(-31.26, -2.35) * mm, "end": v(-31.22, -2.63) * mm});
            skLineSegment(sketch, "E308", {"start": v(-31.22, -2.63) * mm, "end": v(-31.26, -3) * mm});
            skLineSegment(sketch, "E309", {"start": v(-31.26, -3) * mm, "end": v(-31.41, -3.84) * mm});
            skLineSegment(sketch, "E310", {"start": v(-31.41, -3.84) * mm, "end": v(-31.6, -4.8) * mm});
            skLineSegment(sketch, "E311", {"start": v(-31.6, -4.8) * mm, "end": v(-31.79, -5.82) * mm});
            skLineSegment(sketch, "E312", {"start": v(-31.79, -5.82) * mm, "end": v(-32, -6.86) * mm});
            skLineSegment(sketch, "E313", {"start": v(-32, -6.86) * mm, "end": v(-32.19, -7.86) * mm});
            skLineSegment(sketch, "E314", {"start": v(-32.19, -7.86) * mm, "end": v(-32.37, -8.77) * mm});
            skLineSegment(sketch, "E315", {"start": v(-32.37, -8.77) * mm, "end": v(-32.53, -9.52) * mm});
            skLineSegment(sketch, "E316", {"start": v(-32.53, -9.52) * mm, "end": v(-32.64, -10.08) * mm});
            skLineSegment(sketch, "E317", {"start": v(-32.64, -10.08) * mm, "end": v(-32.87, -10.68) * mm});
            skLineSegment(sketch, "E318", {"start": v(-32.87, -10.68) * mm, "end": v(-33.23, -11.1) * mm});
            skLineSegment(sketch, "E319", {"start": v(-33.23, -11.1) * mm, "end": v(-33.72, -11.39) * mm});
            skLineSegment(sketch, "E320", {"start": v(-33.72, -11.39) * mm, "end": v(-34.29, -11.56) * mm});
            skLineSegment(sketch, "E321", {"start": v(-34.29, -11.56) * mm, "end": v(-34.93, -11.64) * mm});
            skLineSegment(sketch, "E322", {"start": v(-34.93, -11.64) * mm, "end": v(-35.63, -11.67) * mm});
            skLineSegment(sketch, "E323", {"start": v(-35.63, -11.67) * mm, "end": v(-36.34, -11.67) * mm});
            skLineSegment(sketch, "E324", {"start": v(-36.34, -11.67) * mm, "end": v(-37.06, -11.67) * mm});
            skLineSegment(sketch, "E325", {"start": v(-37.06, -11.67) * mm, "end": v(-38.86, -11.67) * mm});
            skLineSegment(sketch, "E326", {"start": v(-38.86, -11.67) * mm, "end": v(-40.66, -11.67) * mm});
            skLineSegment(sketch, "E327", {"start": v(-40.66, -11.67) * mm, "end": v(-42.47, -11.67) * mm});
            skLineSegment(sketch, "E328", {"start": v(-42.47, -11.67) * mm, "end": v(-44.27, -11.67) * mm});
            skLineSegment(sketch, "E329", {"start": v(-44.27, -11.67) * mm, "end": v(-46.07, -11.67) * mm});
            skLineSegment(sketch, "E330", {"start": v(-46.07, -11.67) * mm, "end": v(-47.87, -11.67) * mm});
            skLineSegment(sketch, "E331", {"start": v(-47.87, -11.67) * mm, "end": v(-49.67, -11.67) * mm});
            skLineSegment(sketch, "E332", {"start": v(-49.67, -11.67) * mm, "end": v(-51.47, -11.67) * mm});
            skLineSegment(sketch, "E333", {"start": v(-51.47, -11.67) * mm, "end": v(-51.63, -12.36) * mm});
            skLineSegment(sketch, "E334", {"start": v(-51.63, -12.36) * mm, "end": v(-51.79, -13.05) * mm});
            skLineSegment(sketch, "E335", {"start": v(-51.79, -13.05) * mm, "end": v(-51.94, -13.74) * mm});
            skLineSegment(sketch, "E336", {"start": v(-51.94, -13.74) * mm, "end": v(-52.1, -14.43) * mm});
            skLineSegment(sketch, "E337", {"start": v(-52.1, -14.43) * mm, "end": v(-52.26, -15.12) * mm});
            skLineSegment(sketch, "E338", {"start": v(-52.26, -15.12) * mm, "end": v(-52.41, -15.81) * mm});
            skLineSegment(sketch, "E339", {"start": v(-52.41, -15.81) * mm, "end": v(-52.57, -16.5) * mm});
            skLineSegment(sketch, "E340", {"start": v(-52.57, -16.5) * mm, "end": v(-52.73, -17.2) * mm});
            skLineSegment(sketch, "E341", {"start": v(-52.73, -17.2) * mm, "end": v(-52.1, -17.2) * mm});
            skLineSegment(sketch, "E342", {"start": v(-52.1, -17.2) * mm, "end": v(-50.45, -17.2) * mm});
            skLineSegment(sketch, "E343", {"start": v(-50.45, -17.2) * mm, "end": v(-48.03, -17.2) * mm});
            skLineSegment(sketch, "E344", {"start": v(-48.03, -17.2) * mm, "end": v(-45.14, -17.2) * mm});
            skLineSegment(sketch, "E345", {"start": v(-45.14, -17.2) * mm, "end": v(-42.07, -17.2) * mm});
            skLineSegment(sketch, "E346", {"start": v(-42.07, -17.2) * mm, "end": v(-39.12, -17.2) * mm});
            skLineSegment(sketch, "E347", {"start": v(-39.12, -17.2) * mm, "end": v(-36.55, -17.2) * mm});
            skLineSegment(sketch, "E348", {"start": v(-36.55, -17.2) * mm, "end": v(-34.68, -17.2) * mm});
            skLineSegment(sketch, "E349", {"start": v(-34.68, -17.2) * mm, "end": v(-33.26, -17.13) * mm});
            skLineSegment(sketch, "E350", {"start": v(-33.26, -17.13) * mm, "end": v(-31.9, -16.92) * mm});
            skLineSegment(sketch, "E351", {"start": v(-31.9, -16.92) * mm, "end": v(-30.62, -16.56) * mm});
            skLineSegment(sketch, "E352", {"start": v(-30.62, -16.56) * mm, "end": v(-29.46, -16.03) * mm});
            skLineSegment(sketch, "E353", {"start": v(-29.46, -16.03) * mm, "end": v(-28.42, -15.32) * mm});
            skLineSegment(sketch, "E354", {"start": v(-28.42, -15.32) * mm, "end": v(-27.55, -14.42) * mm});
            skLineSegment(sketch, "E355", {"start": v(-27.55, -14.42) * mm, "end": v(-26.87, -13.31) * mm});
            skLineSegment(sketch, "E356", {"start": v(-26.87, -13.31) * mm, "end": v(-26.4, -12) * mm});
            skLineSegment(sketch, "E357", {"start": v(-26.4, -12) * mm, "end": v(-26.05, -10.58) * mm});
            skLineSegment(sketch, "E358", {"start": v(-26.05, -10.58) * mm, "end": v(-25.74, -9.27) * mm});
            skLineSegment(sketch, "E359", {"start": v(-25.74, -9.27) * mm, "end": v(-25.47, -8.04) * mm});
            skLineSegment(sketch, "E360", {"start": v(-25.47, -8.04) * mm, "end": v(-25.22, -6.87) * mm});
            skLineSegment(sketch, "E361", {"start": v(-25.22, -6.87) * mm, "end": v(-25, -5.73) * mm});
            skLineSegment(sketch, "E362", {"start": v(-25, -5.73) * mm, "end": v(-24.77, -4.6) * mm});
            skLineSegment(sketch, "E363", {"start": v(-24.77, -4.6) * mm, "end": v(-24.56, -3.48) * mm});
            skLineSegment(sketch, "E364", {"start": v(-24.56, -3.48) * mm, "end": v(-24.36, -2.34) * mm});
            skLineSegment(sketch, "E365", {"start": v(-24.36, -2.34) * mm, "end": v(-24.24, -1) * mm});
            skLineSegment(sketch, "E366", {"start": v(-24.24, -1) * mm, "end": v(-24.38, 0.24) * mm});
            skLineSegment(sketch, "E367", {"start": v(-24.38, 0.24) * mm, "end": v(-24.78, 1.34) * mm});
            skLineSegment(sketch, "E368", {"start": v(-24.78, 1.34) * mm, "end": v(-25.4, 2.28) * mm});
            skLineSegment(sketch, "E369", {"start": v(-25.4, 2.28) * mm, "end": v(-26.27, 3.05) * mm});
            skLineSegment(sketch, "E370", {"start": v(-26.27, 3.05) * mm, "end": v(-27.34, 3.62) * mm});
            skLineSegment(sketch, "E371", {"start": v(-27.34, 3.62) * mm, "end": v(-28.62, 3.98) * mm});
            skLineSegment(sketch, "E372", {"start": v(-28.62, 3.98) * mm, "end": v(-30.08, 4.1) * mm});
            skLineSegment(sketch, "E373", {"start": v(-30.08, 4.1) * mm, "end": v(-30.66, 4.1) * mm});
            skLineSegment(sketch, "E374", {"start": v(-30.66, 4.1) * mm, "end": v(-31.75, 4.1) * mm});
            skLineSegment(sketch, "E375", {"start": v(-31.75, 4.1) * mm, "end": v(-33.17, 4.1) * mm});
            skLineSegment(sketch, "E376", {"start": v(-33.17, 4.1) * mm, "end": v(-34.73, 4.1) * mm});
            skLineSegment(sketch, "E377", {"start": v(-34.73, 4.1) * mm, "end": v(-36.26, 4.1) * mm});
            skLineSegment(sketch, "E378", {"start": v(-36.26, 4.1) * mm, "end": v(-37.58, 4.1) * mm});
            skLineSegment(sketch, "E379", {"start": v(-37.58, 4.1) * mm, "end": v(-38.5, 4.1) * mm});
            skLineSegment(sketch, "E380", {"start": v(-38.5, 4.1) * mm, "end": v(-38.85, 4.1) * mm});
            skLineSegment(sketch, "E381", {"start": v(-38.85, 4.1) * mm, "end": v(-39.23, 4.1) * mm});
            skLineSegment(sketch, "E382", {"start": v(-39.23, 4.1) * mm, "end": v(-39.63, 4.1) * mm});
            skLineSegment(sketch, "E383", {"start": v(-39.63, 4.1) * mm, "end": v(-40.04, 4.12) * mm});
            skLineSegment(sketch, "E384", {"start": v(-40.04, 4.12) * mm, "end": v(-40.4, 4.2) * mm});
            skLineSegment(sketch, "E385", {"start": v(-40.4, 4.2) * mm, "end": v(-40.72, 4.35) * mm});
            skLineSegment(sketch, "E386", {"start": v(-40.72, 4.35) * mm, "end": v(-40.95, 4.6) * mm});
            skLineSegment(sketch, "E387", {"start": v(-40.95, 4.6) * mm, "end": v(-41.06, 4.97) * mm});
            skLineSegment(sketch, "E388", {"start": v(-41.06, 4.97) * mm, "end": v(-41.03, 5.5) * mm});
            skLineSegment(sketch, "E389", {"start": v(-41.03, 5.5) * mm, "end": v(-40.99, 5.77) * mm});
            skLineSegment(sketch, "E390", {"start": v(-40.99, 5.77) * mm, "end": v(-40.94, 6.06) * mm});
            skLineSegment(sketch, "E391", {"start": v(-40.94, 6.06) * mm, "end": v(-40.89, 6.37) * mm});
            skLineSegment(sketch, "E392", {"start": v(-40.89, 6.37) * mm, "end": v(-40.83, 6.72) * mm});
            skLineSegment(sketch, "E393", {"start": v(-40.83, 6.72) * mm, "end": v(-40.77, 7.1) * mm});
            skLineSegment(sketch, "E394", {"start": v(-40.77, 7.1) * mm, "end": v(-40.7, 7.53) * mm});
            skLineSegment(sketch, "E395", {"start": v(-40.7, 7.53) * mm, "end": v(-40.61, 8) * mm});
            skLineSegment(sketch, "E396", {"start": v(-40.61, 8) * mm, "end": v(-40.51, 8.53) * mm});
            skSolve(sketch);
        }
        {
            var Q0;
            Q0 = qSketchRegion(id + "F8", true);
            extrude(context, id + "F9", {"entities" : qUnion([Q0]), "depth" : 40 * mm, "offsetDistance" : 25 * mm});
        }
        {
            var Q0;
            Q0=makeQuery(id+"F9.opExtrude","SWEPT_BODY",BODY,{"disambiguationData":[OSD([sQuery(id+"F8.wireOp",EDGE,"E237"),sQuery(id+"F8.wireOp",EDGE,"E238"),sQuery(id+"F8.wireOp",EDGE,"E239"),sQuery(id+"F8.wireOp",EDGE,"E240"),sQuery(id+"F8.wireOp",EDGE,"E241"),sQuery(id+"F8.wireOp",EDGE,"E242"),sQuery(id+"F8.wireOp",EDGE,"E243"),sQuery(id+"F8.wireOp",EDGE,"E244"),sQuery(id+"F8.wireOp",EDGE,"E245"),sQuery(id+"F8.wireOp",EDGE,"E246"),sQuery(id+"F8.wireOp",EDGE,"E247"),sQuery(id+"F8.wireOp",EDGE,"E248"),sQuery(id+"F8.wireOp",EDGE,"E249"),sQuery(id+"F8.wireOp",EDGE,"E250"),sQuery(id+"F8.wireOp",EDGE,"E251"),sQuery(id+"F8.wireOp",EDGE,"E252"),sQuery(id+"F8.wireOp",EDGE,"E253"),sQuery(id+"F8.wireOp",EDGE,"E254"),sQuery(id+"F8.wireOp",EDGE,"E255"),sQuery(id+"F8.wireOp",EDGE,"E256"),sQuery(id+"F8.wireOp",EDGE,"E257"),sQuery(id+"F8.wireOp",EDGE,"E258"),sQuery(id+"F8.wireOp",EDGE,"E259"),sQuery(id+"F8.wireOp",EDGE,"E260"),sQuery(id+"F8.wireOp",EDGE,"E261"),sQuery(id+"F8.wireOp",EDGE,"E262"),sQuery(id+"F8.wireOp",EDGE,"E263"),sQuery(id+"F8.wireOp",EDGE,"E264"),sQuery(id+"F8.wireOp",EDGE,"E265"),sQuery(id+"F8.wireOp",EDGE,"E266"),sQuery(id+"F8.wireOp",EDGE,"E267"),sQuery(id+"F8.wireOp",EDGE,"E268"),sQuery(id+"F8.wireOp",EDGE,"E269"),sQuery(id+"F8.wireOp",EDGE,"E270"),sQuery(id+"F8.wireOp",EDGE,"E271"),sQuery(id+"F8.wireOp",EDGE,"E272"),sQuery(id+"F8.wireOp",EDGE,"E273"),sQuery(id+"F8.wireOp",EDGE,"E274"),sQuery(id+"F8.wireOp",EDGE,"E275"),sQuery(id+"F8.wireOp",EDGE,"E276"),sQuery(id+"F8.wireOp",EDGE,"E277"),sQuery(id+"F8.wireOp",EDGE,"E278"),sQuery(id+"F8.wireOp",EDGE,"E279"),sQuery(id+"F8.wireOp",EDGE,"E280"),sQuery(id+"F8.wireOp",EDGE,"E281"),sQuery(id+"F8.wireOp",EDGE,"E282"),sQuery(id+"F8.wireOp",EDGE,"E283"),sQuery(id+"F8.wireOp",EDGE,"E284"),sQuery(id+"F8.wireOp",EDGE,"E285"),sQuery(id+"F8.wireOp",EDGE,"E286"),sQuery(id+"F8.wireOp",EDGE,"E287"),sQuery(id+"F8.wireOp",EDGE,"E288"),sQuery(id+"F8.wireOp",EDGE,"E289"),sQuery(id+"F8.wireOp",EDGE,"E290"),sQuery(id+"F8.wireOp",EDGE,"E291"),sQuery(id+"F8.wireOp",EDGE,"E292"),sQuery(id+"F8.wireOp",EDGE,"E293"),sQuery(id+"F8.wireOp",EDGE,"E294"),sQuery(id+"F8.wireOp",EDGE,"E295"),sQuery(id+"F8.wireOp",EDGE,"E296"),sQuery(id+"F8.wireOp",EDGE,"E297"),sQuery(id+"F8.wireOp",EDGE,"E298"),sQuery(id+"F8.wireOp",EDGE,"E299"),sQuery(id+"F8.wireOp",EDGE,"E300"),sQuery(id+"F8.wireOp",EDGE,"E301"),sQuery(id+"F8.wireOp",EDGE,"E302"),sQuery(id+"F8.wireOp",EDGE,"E303"),sQuery(id+"F8.wireOp",EDGE,"E304"),sQuery(id+"F8.wireOp",EDGE,"E305"),sQuery(id+"F8.wireOp",EDGE,"E306"),sQuery(id+"F8.wireOp",EDGE,"E307"),sQuery(id+"F8.wireOp",EDGE,"E308"),sQuery(id+"F8.wireOp",EDGE,"E309"),sQuery(id+"F8.wireOp",EDGE,"E310"),sQuery(id+"F8.wireOp",EDGE,"E311"),sQuery(id+"F8.wireOp",EDGE,"E312"),sQuery(id+"F8.wireOp",EDGE,"E313"),sQuery(id+"F8.wireOp",EDGE,"E314"),sQuery(id+"F8.wireOp",EDGE,"E315"),sQuery(id+"F8.wireOp",EDGE,"E316"),sQuery(id+"F8.wireOp",EDGE,"E317"),sQuery(id+"F8.wireOp",EDGE,"E318"),sQuery(id+"F8.wireOp",EDGE,"E319"),sQuery(id+"F8.wireOp",EDGE,"E320"),sQuery(id+"F8.wireOp",EDGE,"E321"),sQuery(id+"F8.wireOp",EDGE,"E322"),sQuery(id+"F8.wireOp",EDGE,"E323"),sQuery(id+"F8.wireOp",EDGE,"E324"),sQuery(id+"F8.wireOp",EDGE,"E325"),sQuery(id+"F8.wireOp",EDGE,"E326"),sQuery(id+"F8.wireOp",EDGE,"E327"),sQuery(id+"F8.wireOp",EDGE,"E328"),sQuery(id+"F8.wireOp",EDGE,"E329"),sQuery(id+"F8.wireOp",EDGE,"E330"),sQuery(id+"F8.wireOp",EDGE,"E331"),sQuery(id+"F8.wireOp",EDGE,"E332"),sQuery(id+"F8.wireOp",EDGE,"E333"),sQuery(id+"F8.wireOp",EDGE,"E334"),sQuery(id+"F8.wireOp",EDGE,"E335"),sQuery(id+"F8.wireOp",EDGE,"E336"),sQuery(id+"F8.wireOp",EDGE,"E337"),sQuery(id+"F8.wireOp",EDGE,"E338"),sQuery(id+"F8.wireOp",EDGE,"E339"),sQuery(id+"F8.wireOp",EDGE,"E340"),sQuery(id+"F8.wireOp",EDGE,"E341"),sQuery(id+"F8.wireOp",EDGE,"E342"),sQuery(id+"F8.wireOp",EDGE,"E343"),sQuery(id+"F8.wireOp",EDGE,"E344"),sQuery(id+"F8.wireOp",EDGE,"E345"),sQuery(id+"F8.wireOp",EDGE,"E346"),sQuery(id+"F8.wireOp",EDGE,"E347"),sQuery(id+"F8.wireOp",EDGE,"E348"),sQuery(id+"F8.wireOp",EDGE,"E349"),sQuery(id+"F8.wireOp",EDGE,"E350"),sQuery(id+"F8.wireOp",EDGE,"E351"),sQuery(id+"F8.wireOp",EDGE,"E352"),sQuery(id+"F8.wireOp",EDGE,"E353"),sQuery(id+"F8.wireOp",EDGE,"E354"),sQuery(id+"F8.wireOp",EDGE,"E355"),sQuery(id+"F8.wireOp",EDGE,"E356"),sQuery(id+"F8.wireOp",EDGE,"E357"),sQuery(id+"F8.wireOp",EDGE,"E358"),sQuery(id+"F8.wireOp",EDGE,"E359"),sQuery(id+"F8.wireOp",EDGE,"E360"),sQuery(id+"F8.wireOp",EDGE,"E361"),sQuery(id+"F8.wireOp",EDGE,"E362"),sQuery(id+"F8.wireOp",EDGE,"E363"),sQuery(id+"F8.wireOp",EDGE,"E364"),sQuery(id+"F8.wireOp",EDGE,"E365"),sQuery(id+"F8.wireOp",EDGE,"E366"),sQuery(id+"F8.wireOp",EDGE,"E367"),sQuery(id+"F8.wireOp",EDGE,"E368"),sQuery(id+"F8.wireOp",EDGE,"E369"),sQuery(id+"F8.wireOp",EDGE,"E370"),sQuery(id+"F8.wireOp",EDGE,"E371"),sQuery(id+"F8.wireOp",EDGE,"E372"),sQuery(id+"F8.wireOp",EDGE,"E373"),sQuery(id+"F8.wireOp",EDGE,"E374"),sQuery(id+"F8.wireOp",EDGE,"E375"),sQuery(id+"F8.wireOp",EDGE,"E376"),sQuery(id+"F8.wireOp",EDGE,"E377"),sQuery(id+"F8.wireOp",EDGE,"E378"),sQuery(id+"F8.wireOp",EDGE,"E379"),sQuery(id+"F8.wireOp",EDGE,"E380"),sQuery(id+"F8.wireOp",EDGE,"E381"),sQuery(id+"F8.wireOp",EDGE,"E382"),sQuery(id+"F8.wireOp",EDGE,"E383"),sQuery(id+"F8.wireOp",EDGE,"E384"),sQuery(id+"F8.wireOp",EDGE,"E385"),sQuery(id+"F8.wireOp",EDGE,"E386"),sQuery(id+"F8.wireOp",EDGE,"E387"),sQuery(id+"F8.wireOp",EDGE,"E388"),sQuery(id+"F8.wireOp",EDGE,"E389"),sQuery(id+"F8.wireOp",EDGE,"E390"),sQuery(id+"F8.wireOp",EDGE,"E391"),sQuery(id+"F8.wireOp",EDGE,"E392"),sQuery(id+"F8.wireOp",EDGE,"E393"),sQuery(id+"F8.wireOp",EDGE,"E394"),sQuery(id+"F8.wireOp",EDGE,"E395"),sQuery(id+"F8.wireOp",EDGE,"E396")])]});
            var Q1;
            Q1=makeQuery(id+"F9.opExtrude","SWEPT_BODY",BODY,{"disambiguationData":[OSD([sQuery(id+"F8.wireOp",EDGE,"E143"),sQuery(id+"F8.wireOp",EDGE,"E144"),sQuery(id+"F8.wireOp",EDGE,"E145"),sQuery(id+"F8.wireOp",EDGE,"E146"),sQuery(id+"F8.wireOp",EDGE,"E147"),sQuery(id+"F8.wireOp",EDGE,"E148"),sQuery(id+"F8.wireOp",EDGE,"E149"),sQuery(id+"F8.wireOp",EDGE,"E150"),sQuery(id+"F8.wireOp",EDGE,"E151"),sQuery(id+"F8.wireOp",EDGE,"E152"),sQuery(id+"F8.wireOp",EDGE,"E153"),sQuery(id+"F8.wireOp",EDGE,"E154"),sQuery(id+"F8.wireOp",EDGE,"E155"),sQuery(id+"F8.wireOp",EDGE,"E156"),sQuery(id+"F8.wireOp",EDGE,"E156"),sQuery(id+"F8.wireOp",EDGE,"E156"),sQuery(id+"F8.wireOp",EDGE,"E157"),sQuery(id+"F8.wireOp",EDGE,"E158"),sQuery(id+"F8.wireOp",EDGE,"E159"),sQuery(id+"F8.wireOp",EDGE,"E160"),sQuery(id+"F8.wireOp",EDGE,"E161"),sQuery(id+"F8.wireOp",EDGE,"E162"),sQuery(id+"F8.wireOp",EDGE,"E163"),sQuery(id+"F8.wireOp",EDGE,"E164"),sQuery(id+"F8.wireOp",EDGE,"E165"),sQuery(id+"F8.wireOp",EDGE,"E166"),sQuery(id+"F8.wireOp",EDGE,"E167"),sQuery(id+"F8.wireOp",EDGE,"E168"),sQuery(id+"F8.wireOp",EDGE,"E169"),sQuery(id+"F8.wireOp",EDGE,"E170"),sQuery(id+"F8.wireOp",EDGE,"E171"),sQuery(id+"F8.wireOp",EDGE,"E172"),sQuery(id+"F8.wireOp",EDGE,"E173"),sQuery(id+"F8.wireOp",EDGE,"E174"),sQuery(id+"F8.wireOp",EDGE,"E175"),sQuery(id+"F8.wireOp",EDGE,"E176"),sQuery(id+"F8.wireOp",EDGE,"E177"),sQuery(id+"F8.wireOp",EDGE,"E178"),sQuery(id+"F8.wireOp",EDGE,"E179"),sQuery(id+"F8.wireOp",EDGE,"E180"),sQuery(id+"F8.wireOp",EDGE,"E181"),sQuery(id+"F8.wireOp",EDGE,"E182"),sQuery(id+"F8.wireOp",EDGE,"E183"),sQuery(id+"F8.wireOp",EDGE,"E184"),sQuery(id+"F8.wireOp",EDGE,"E185"),sQuery(id+"F8.wireOp",EDGE,"E186"),sQuery(id+"F8.wireOp",EDGE,"E187"),sQuery(id+"F8.wireOp",EDGE,"E188"),sQuery(id+"F8.wireOp",EDGE,"E189"),sQuery(id+"F8.wireOp",EDGE,"E190"),sQuery(id+"F8.wireOp",EDGE,"E191"),sQuery(id+"F8.wireOp",EDGE,"E192"),sQuery(id+"F8.wireOp",EDGE,"E193"),sQuery(id+"F8.wireOp",EDGE,"E194"),sQuery(id+"F8.wireOp",EDGE,"E195"),sQuery(id+"F8.wireOp",EDGE,"E196"),sQuery(id+"F8.wireOp",EDGE,"E197"),sQuery(id+"F8.wireOp",EDGE,"E198"),sQuery(id+"F8.wireOp",EDGE,"E199"),sQuery(id+"F8.wireOp",EDGE,"E200"),sQuery(id+"F8.wireOp",EDGE,"E201"),sQuery(id+"F8.wireOp",EDGE,"E202"),sQuery(id+"F8.wireOp",EDGE,"E203"),sQuery(id+"F8.wireOp",EDGE,"E204"),sQuery(id+"F8.wireOp",EDGE,"E205"),sQuery(id+"F8.wireOp",EDGE,"E206"),sQuery(id+"F8.wireOp",EDGE,"E207"),sQuery(id+"F8.wireOp",EDGE,"E208"),sQuery(id+"F8.wireOp",EDGE,"E209"),sQuery(id+"F8.wireOp",EDGE,"E210"),sQuery(id+"F8.wireOp",EDGE,"E211"),sQuery(id+"F8.wireOp",EDGE,"E212"),sQuery(id+"F8.wireOp",EDGE,"E213"),sQuery(id+"F8.wireOp",EDGE,"E214"),sQuery(id+"F8.wireOp",EDGE,"E215"),sQuery(id+"F8.wireOp",EDGE,"E216"),sQuery(id+"F8.wireOp",EDGE,"E217"),sQuery(id+"F8.wireOp",EDGE,"E218"),sQuery(id+"F8.wireOp",EDGE,"E219"),sQuery(id+"F8.wireOp",EDGE,"E220"),sQuery(id+"F8.wireOp",EDGE,"E221"),sQuery(id+"F8.wireOp",EDGE,"E222"),sQuery(id+"F8.wireOp",EDGE,"E223"),sQuery(id+"F8.wireOp",EDGE,"E224"),sQuery(id+"F8.wireOp",EDGE,"E225"),sQuery(id+"F8.wireOp",EDGE,"E226"),sQuery(id+"F8.wireOp",EDGE,"E227"),sQuery(id+"F8.wireOp",EDGE,"E228"),sQuery(id+"F8.wireOp",EDGE,"E229"),sQuery(id+"F8.wireOp",EDGE,"E230"),sQuery(id+"F8.wireOp",EDGE,"E231"),sQuery(id+"F8.wireOp",EDGE,"E232"),sQuery(id+"F8.wireOp",EDGE,"E233"),sQuery(id+"F8.wireOp",EDGE,"E234"),sQuery(id+"F8.wireOp",EDGE,"E235"),sQuery(id+"F8.wireOp",EDGE,"E236")])]});
            var Q2;
            Q2=makeQuery(id+"F9.opExtrude","SWEPT_BODY",BODY,{"disambiguationData":[OSD([sQuery(id+"F8.wireOp",EDGE,"E111"),sQuery(id+"F8.wireOp",EDGE,"E112"),sQuery(id+"F8.wireOp",EDGE,"E113"),sQuery(id+"F8.wireOp",EDGE,"E114"),sQuery(id+"F8.wireOp",EDGE,"E115"),sQuery(id+"F8.wireOp",EDGE,"E116"),sQuery(id+"F8.wireOp",EDGE,"E117"),sQuery(id+"F8.wireOp",EDGE,"E118"),sQuery(id+"F8.wireOp",EDGE,"E119"),sQuery(id+"F8.wireOp",EDGE,"E120"),sQuery(id+"F8.wireOp",EDGE,"E121"),sQuery(id+"F8.wireOp",EDGE,"E122"),sQuery(id+"F8.wireOp",EDGE,"E123"),sQuery(id+"F8.wireOp",EDGE,"E124"),sQuery(id+"F8.wireOp",EDGE,"E125"),sQuery(id+"F8.wireOp",EDGE,"E126"),sQuery(id+"F8.wireOp",EDGE,"E127"),sQuery(id+"F8.wireOp",EDGE,"E128"),sQuery(id+"F8.wireOp",EDGE,"E129"),sQuery(id+"F8.wireOp",EDGE,"E130"),sQuery(id+"F8.wireOp",EDGE,"E131"),sQuery(id+"F8.wireOp",EDGE,"E132"),sQuery(id+"F8.wireOp",EDGE,"E133"),sQuery(id+"F8.wireOp",EDGE,"E134"),sQuery(id+"F8.wireOp",EDGE,"E135"),sQuery(id+"F8.wireOp",EDGE,"E136"),sQuery(id+"F8.wireOp",EDGE,"E137"),sQuery(id+"F8.wireOp",EDGE,"E138"),sQuery(id+"F8.wireOp",EDGE,"E139"),sQuery(id+"F8.wireOp",EDGE,"E140"),sQuery(id+"F8.wireOp",EDGE,"E141"),sQuery(id+"F8.wireOp",EDGE,"E142")])]});
            var Q3;
            Q3=makeQuery(id+"F9.opExtrude","SWEPT_BODY",BODY,{"disambiguationData":[OSD([sQuery(id+"F8.wireOp",EDGE,"E4"),sQuery(id+"F8.wireOp",EDGE,"E5"),sQuery(id+"F8.wireOp",EDGE,"E6"),sQuery(id+"F8.wireOp",EDGE,"E7"),sQuery(id+"F8.wireOp",EDGE,"E8"),sQuery(id+"F8.wireOp",EDGE,"E9"),sQuery(id+"F8.wireOp",EDGE,"E10"),sQuery(id+"F8.wireOp",EDGE,"E11"),sQuery(id+"F8.wireOp",EDGE,"E12"),sQuery(id+"F8.wireOp",EDGE,"E13"),sQuery(id+"F8.wireOp",EDGE,"E14"),sQuery(id+"F8.wireOp",EDGE,"E15"),sQuery(id+"F8.wireOp",EDGE,"E16"),sQuery(id+"F8.wireOp",EDGE,"E17"),sQuery(id+"F8.wireOp",EDGE,"E18"),sQuery(id+"F8.wireOp",EDGE,"E19"),sQuery(id+"F8.wireOp",EDGE,"E20"),sQuery(id+"F8.wireOp",EDGE,"E21"),sQuery(id+"F8.wireOp",EDGE,"E22"),sQuery(id+"F8.wireOp",EDGE,"E23"),sQuery(id+"F8.wireOp",EDGE,"E24"),sQuery(id+"F8.wireOp",EDGE,"E25"),sQuery(id+"F8.wireOp",EDGE,"E26"),sQuery(id+"F8.wireOp",EDGE,"E27"),sQuery(id+"F8.wireOp",EDGE,"E28"),sQuery(id+"F8.wireOp",EDGE,"E29"),sQuery(id+"F8.wireOp",EDGE,"E30"),sQuery(id+"F8.wireOp",EDGE,"E31"),sQuery(id+"F8.wireOp",EDGE,"E32"),sQuery(id+"F8.wireOp",EDGE,"E33"),sQuery(id+"F8.wireOp",EDGE,"E34"),sQuery(id+"F8.wireOp",EDGE,"E35"),sQuery(id+"F8.wireOp",EDGE,"E36"),sQuery(id+"F8.wireOp",EDGE,"E37"),sQuery(id+"F8.wireOp",EDGE,"E38"),sQuery(id+"F8.wireOp",EDGE,"E39"),sQuery(id+"F8.wireOp",EDGE,"E40"),sQuery(id+"F8.wireOp",EDGE,"E41"),sQuery(id+"F8.wireOp",EDGE,"E42"),sQuery(id+"F8.wireOp",EDGE,"E43"),sQuery(id+"F8.wireOp",EDGE,"E44"),sQuery(id+"F8.wireOp",EDGE,"E45"),sQuery(id+"F8.wireOp",EDGE,"E46"),sQuery(id+"F8.wireOp",EDGE,"E47"),sQuery(id+"F8.wireOp",EDGE,"E48"),sQuery(id+"F8.wireOp",EDGE,"E49"),sQuery(id+"F8.wireOp",EDGE,"E50"),sQuery(id+"F8.wireOp",EDGE,"E51"),sQuery(id+"F8.wireOp",EDGE,"E52"),sQuery(id+"F8.wireOp",EDGE,"E53"),sQuery(id+"F8.wireOp",EDGE,"E54"),sQuery(id+"F8.wireOp",EDGE,"E55"),sQuery(id+"F8.wireOp",EDGE,"E56"),sQuery(id+"F8.wireOp",EDGE,"E57"),sQuery(id+"F8.wireOp",EDGE,"E58"),sQuery(id+"F8.wireOp",EDGE,"E59"),sQuery(id+"F8.wireOp",EDGE,"E60"),sQuery(id+"F8.wireOp",EDGE,"E61"),sQuery(id+"F8.wireOp",EDGE,"E62"),sQuery(id+"F8.wireOp",EDGE,"E63"),sQuery(id+"F8.wireOp",EDGE,"E64"),sQuery(id+"F8.wireOp",EDGE,"E65"),sQuery(id+"F8.wireOp",EDGE,"E66"),sQuery(id+"F8.wireOp",EDGE,"E67"),sQuery(id+"F8.wireOp",EDGE,"E68"),sQuery(id+"F8.wireOp",EDGE,"E69"),sQuery(id+"F8.wireOp",EDGE,"E70"),sQuery(id+"F8.wireOp",EDGE,"E71"),sQuery(id+"F8.wireOp",EDGE,"E72"),sQuery(id+"F8.wireOp",EDGE,"E73"),sQuery(id+"F8.wireOp",EDGE,"E74"),sQuery(id+"F8.wireOp",EDGE,"E75"),sQuery(id+"F8.wireOp",EDGE,"E76"),sQuery(id+"F8.wireOp",EDGE,"E77"),sQuery(id+"F8.wireOp",EDGE,"E78"),sQuery(id+"F8.wireOp",EDGE,"E79"),sQuery(id+"F8.wireOp",EDGE,"E80"),sQuery(id+"F8.wireOp",EDGE,"E81"),sQuery(id+"F8.wireOp",EDGE,"E82"),sQuery(id+"F8.wireOp",EDGE,"E83"),sQuery(id+"F8.wireOp",EDGE,"E84"),sQuery(id+"F8.wireOp",EDGE,"E85"),sQuery(id+"F8.wireOp",EDGE,"E86"),sQuery(id+"F8.wireOp",EDGE,"E87"),sQuery(id+"F8.wireOp",EDGE,"E88"),sQuery(id+"F8.wireOp",EDGE,"E89"),sQuery(id+"F8.wireOp",EDGE,"E90"),sQuery(id+"F8.wireOp",EDGE,"E91"),sQuery(id+"F8.wireOp",EDGE,"E92"),sQuery(id+"F8.wireOp",EDGE,"E93"),sQuery(id+"F8.wireOp",EDGE,"E94"),sQuery(id+"F8.wireOp",EDGE,"E95"),sQuery(id+"F8.wireOp",EDGE,"E96"),sQuery(id+"F8.wireOp",EDGE,"E97"),sQuery(id+"F8.wireOp",EDGE,"E98"),sQuery(id+"F8.wireOp",EDGE,"E99"),sQuery(id+"F8.wireOp",EDGE,"E100"),sQuery(id+"F8.wireOp",EDGE,"E100"),sQuery(id+"F8.wireOp",EDGE,"E100"),sQuery(id+"F8.wireOp",EDGE,"E101"),sQuery(id+"F8.wireOp",EDGE,"E102"),sQuery(id+"F8.wireOp",EDGE,"E102"),sQuery(id+"F8.wireOp",EDGE,"E102"),sQuery(id+"F8.wireOp",EDGE,"E102"),sQuery(id+"F8.wireOp",EDGE,"E103"),sQuery(id+"F8.wireOp",EDGE,"E104"),sQuery(id+"F8.wireOp",EDGE,"E105"),sQuery(id+"F8.wireOp",EDGE,"E106"),sQuery(id+"F8.wireOp",EDGE,"E107"),sQuery(id+"F8.wireOp",EDGE,"E108"),sQuery(id+"F8.wireOp",EDGE,"E109"),sQuery(id+"F8.wireOp",EDGE,"E110")])]});
            var Q4;
            Q4=sQuery(id+"F0.wireOp",VERTEX,"E0.center");
            transform(context, id + "F10", {"entities" : qUnion([Q0, Q1, Q2, Q3]), "transformType" : TransformType.SCALE_UNIFORMLY, "scale" : 0.3, "scalePoint" : qUnion([Q4]), "makeCopy" : false});
        }
        {
            var Q0;
            Q0=makeQuery(id+"F9.opExtrude","SWEPT_BODY",BODY,{"disambiguationData":[OSD([sQuery(id+"F8.wireOp",EDGE,"E237"),sQuery(id+"F8.wireOp",EDGE,"E238"),sQuery(id+"F8.wireOp",EDGE,"E239"),sQuery(id+"F8.wireOp",EDGE,"E240"),sQuery(id+"F8.wireOp",EDGE,"E241"),sQuery(id+"F8.wireOp",EDGE,"E242"),sQuery(id+"F8.wireOp",EDGE,"E243"),sQuery(id+"F8.wireOp",EDGE,"E244"),sQuery(id+"F8.wireOp",EDGE,"E245"),sQuery(id+"F8.wireOp",EDGE,"E246"),sQuery(id+"F8.wireOp",EDGE,"E247"),sQuery(id+"F8.wireOp",EDGE,"E248"),sQuery(id+"F8.wireOp",EDGE,"E249"),sQuery(id+"F8.wireOp",EDGE,"E250"),sQuery(id+"F8.wireOp",EDGE,"E251"),sQuery(id+"F8.wireOp",EDGE,"E252"),sQuery(id+"F8.wireOp",EDGE,"E253"),sQuery(id+"F8.wireOp",EDGE,"E254"),sQuery(id+"F8.wireOp",EDGE,"E255"),sQuery(id+"F8.wireOp",EDGE,"E256"),sQuery(id+"F8.wireOp",EDGE,"E257"),sQuery(id+"F8.wireOp",EDGE,"E258"),sQuery(id+"F8.wireOp",EDGE,"E259"),sQuery(id+"F8.wireOp",EDGE,"E260"),sQuery(id+"F8.wireOp",EDGE,"E261"),sQuery(id+"F8.wireOp",EDGE,"E262"),sQuery(id+"F8.wireOp",EDGE,"E263"),sQuery(id+"F8.wireOp",EDGE,"E264"),sQuery(id+"F8.wireOp",EDGE,"E265"),sQuery(id+"F8.wireOp",EDGE,"E266"),sQuery(id+"F8.wireOp",EDGE,"E267"),sQuery(id+"F8.wireOp",EDGE,"E268"),sQuery(id+"F8.wireOp",EDGE,"E269"),sQuery(id+"F8.wireOp",EDGE,"E270"),sQuery(id+"F8.wireOp",EDGE,"E271"),sQuery(id+"F8.wireOp",EDGE,"E272"),sQuery(id+"F8.wireOp",EDGE,"E273"),sQuery(id+"F8.wireOp",EDGE,"E274"),sQuery(id+"F8.wireOp",EDGE,"E275"),sQuery(id+"F8.wireOp",EDGE,"E276"),sQuery(id+"F8.wireOp",EDGE,"E277"),sQuery(id+"F8.wireOp",EDGE,"E278"),sQuery(id+"F8.wireOp",EDGE,"E279"),sQuery(id+"F8.wireOp",EDGE,"E280"),sQuery(id+"F8.wireOp",EDGE,"E281"),sQuery(id+"F8.wireOp",EDGE,"E282"),sQuery(id+"F8.wireOp",EDGE,"E283"),sQuery(id+"F8.wireOp",EDGE,"E284"),sQuery(id+"F8.wireOp",EDGE,"E285"),sQuery(id+"F8.wireOp",EDGE,"E286"),sQuery(id+"F8.wireOp",EDGE,"E287"),sQuery(id+"F8.wireOp",EDGE,"E288"),sQuery(id+"F8.wireOp",EDGE,"E289"),sQuery(id+"F8.wireOp",EDGE,"E290"),sQuery(id+"F8.wireOp",EDGE,"E291"),sQuery(id+"F8.wireOp",EDGE,"E292"),sQuery(id+"F8.wireOp",EDGE,"E293"),sQuery(id+"F8.wireOp",EDGE,"E294"),sQuery(id+"F8.wireOp",EDGE,"E295"),sQuery(id+"F8.wireOp",EDGE,"E296"),sQuery(id+"F8.wireOp",EDGE,"E297"),sQuery(id+"F8.wireOp",EDGE,"E298"),sQuery(id+"F8.wireOp",EDGE,"E299"),sQuery(id+"F8.wireOp",EDGE,"E300"),sQuery(id+"F8.wireOp",EDGE,"E301"),sQuery(id+"F8.wireOp",EDGE,"E302"),sQuery(id+"F8.wireOp",EDGE,"E303"),sQuery(id+"F8.wireOp",EDGE,"E304"),sQuery(id+"F8.wireOp",EDGE,"E305"),sQuery(id+"F8.wireOp",EDGE,"E306"),sQuery(id+"F8.wireOp",EDGE,"E307"),sQuery(id+"F8.wireOp",EDGE,"E308"),sQuery(id+"F8.wireOp",EDGE,"E309"),sQuery(id+"F8.wireOp",EDGE,"E310"),sQuery(id+"F8.wireOp",EDGE,"E311"),sQuery(id+"F8.wireOp",EDGE,"E312"),sQuery(id+"F8.wireOp",EDGE,"E313"),sQuery(id+"F8.wireOp",EDGE,"E314"),sQuery(id+"F8.wireOp",EDGE,"E315"),sQuery(id+"F8.wireOp",EDGE,"E316"),sQuery(id+"F8.wireOp",EDGE,"E317"),sQuery(id+"F8.wireOp",EDGE,"E318"),sQuery(id+"F8.wireOp",EDGE,"E319"),sQuery(id+"F8.wireOp",EDGE,"E320"),sQuery(id+"F8.wireOp",EDGE,"E321"),sQuery(id+"F8.wireOp",EDGE,"E322"),sQuery(id+"F8.wireOp",EDGE,"E323"),sQuery(id+"F8.wireOp",EDGE,"E324"),sQuery(id+"F8.wireOp",EDGE,"E325"),sQuery(id+"F8.wireOp",EDGE,"E326"),sQuery(id+"F8.wireOp",EDGE,"E327"),sQuery(id+"F8.wireOp",EDGE,"E328"),sQuery(id+"F8.wireOp",EDGE,"E329"),sQuery(id+"F8.wireOp",EDGE,"E330"),sQuery(id+"F8.wireOp",EDGE,"E331"),sQuery(id+"F8.wireOp",EDGE,"E332"),sQuery(id+"F8.wireOp",EDGE,"E333"),sQuery(id+"F8.wireOp",EDGE,"E334"),sQuery(id+"F8.wireOp",EDGE,"E335"),sQuery(id+"F8.wireOp",EDGE,"E336"),sQuery(id+"F8.wireOp",EDGE,"E337"),sQuery(id+"F8.wireOp",EDGE,"E338"),sQuery(id+"F8.wireOp",EDGE,"E339"),sQuery(id+"F8.wireOp",EDGE,"E340"),sQuery(id+"F8.wireOp",EDGE,"E341"),sQuery(id+"F8.wireOp",EDGE,"E342"),sQuery(id+"F8.wireOp",EDGE,"E343"),sQuery(id+"F8.wireOp",EDGE,"E344"),sQuery(id+"F8.wireOp",EDGE,"E345"),sQuery(id+"F8.wireOp",EDGE,"E346"),sQuery(id+"F8.wireOp",EDGE,"E347"),sQuery(id+"F8.wireOp",EDGE,"E348"),sQuery(id+"F8.wireOp",EDGE,"E349"),sQuery(id+"F8.wireOp",EDGE,"E350"),sQuery(id+"F8.wireOp",EDGE,"E351"),sQuery(id+"F8.wireOp",EDGE,"E352"),sQuery(id+"F8.wireOp",EDGE,"E353"),sQuery(id+"F8.wireOp",EDGE,"E354"),sQuery(id+"F8.wireOp",EDGE,"E355"),sQuery(id+"F8.wireOp",EDGE,"E356"),sQuery(id+"F8.wireOp",EDGE,"E357"),sQuery(id+"F8.wireOp",EDGE,"E358"),sQuery(id+"F8.wireOp",EDGE,"E359"),sQuery(id+"F8.wireOp",EDGE,"E360"),sQuery(id+"F8.wireOp",EDGE,"E361"),sQuery(id+"F8.wireOp",EDGE,"E362"),sQuery(id+"F8.wireOp",EDGE,"E363"),sQuery(id+"F8.wireOp",EDGE,"E364"),sQuery(id+"F8.wireOp",EDGE,"E365"),sQuery(id+"F8.wireOp",EDGE,"E366"),sQuery(id+"F8.wireOp",EDGE,"E367"),sQuery(id+"F8.wireOp",EDGE,"E368"),sQuery(id+"F8.wireOp",EDGE,"E369"),sQuery(id+"F8.wireOp",EDGE,"E370"),sQuery(id+"F8.wireOp",EDGE,"E371"),sQuery(id+"F8.wireOp",EDGE,"E372"),sQuery(id+"F8.wireOp",EDGE,"E373"),sQuery(id+"F8.wireOp",EDGE,"E374"),sQuery(id+"F8.wireOp",EDGE,"E375"),sQuery(id+"F8.wireOp",EDGE,"E376"),sQuery(id+"F8.wireOp",EDGE,"E377"),sQuery(id+"F8.wireOp",EDGE,"E378"),sQuery(id+"F8.wireOp",EDGE,"E379"),sQuery(id+"F8.wireOp",EDGE,"E380"),sQuery(id+"F8.wireOp",EDGE,"E381"),sQuery(id+"F8.wireOp",EDGE,"E382"),sQuery(id+"F8.wireOp",EDGE,"E383"),sQuery(id+"F8.wireOp",EDGE,"E384"),sQuery(id+"F8.wireOp",EDGE,"E385"),sQuery(id+"F8.wireOp",EDGE,"E386"),sQuery(id+"F8.wireOp",EDGE,"E387"),sQuery(id+"F8.wireOp",EDGE,"E388"),sQuery(id+"F8.wireOp",EDGE,"E389"),sQuery(id+"F8.wireOp",EDGE,"E390"),sQuery(id+"F8.wireOp",EDGE,"E391"),sQuery(id+"F8.wireOp",EDGE,"E392"),sQuery(id+"F8.wireOp",EDGE,"E393"),sQuery(id+"F8.wireOp",EDGE,"E394"),sQuery(id+"F8.wireOp",EDGE,"E395"),sQuery(id+"F8.wireOp",EDGE,"E396")])]});
            var Q1;
            Q1=makeQuery(id+"F9.opExtrude","SWEPT_BODY",BODY,{"disambiguationData":[OSD([sQuery(id+"F8.wireOp",EDGE,"E143"),sQuery(id+"F8.wireOp",EDGE,"E144"),sQuery(id+"F8.wireOp",EDGE,"E145"),sQuery(id+"F8.wireOp",EDGE,"E146"),sQuery(id+"F8.wireOp",EDGE,"E147"),sQuery(id+"F8.wireOp",EDGE,"E148"),sQuery(id+"F8.wireOp",EDGE,"E149"),sQuery(id+"F8.wireOp",EDGE,"E150"),sQuery(id+"F8.wireOp",EDGE,"E151"),sQuery(id+"F8.wireOp",EDGE,"E152"),sQuery(id+"F8.wireOp",EDGE,"E153"),sQuery(id+"F8.wireOp",EDGE,"E154"),sQuery(id+"F8.wireOp",EDGE,"E155"),sQuery(id+"F8.wireOp",EDGE,"E156"),sQuery(id+"F8.wireOp",EDGE,"E156"),sQuery(id+"F8.wireOp",EDGE,"E156"),sQuery(id+"F8.wireOp",EDGE,"E157"),sQuery(id+"F8.wireOp",EDGE,"E158"),sQuery(id+"F8.wireOp",EDGE,"E159"),sQuery(id+"F8.wireOp",EDGE,"E160"),sQuery(id+"F8.wireOp",EDGE,"E161"),sQuery(id+"F8.wireOp",EDGE,"E162"),sQuery(id+"F8.wireOp",EDGE,"E163"),sQuery(id+"F8.wireOp",EDGE,"E164"),sQuery(id+"F8.wireOp",EDGE,"E165"),sQuery(id+"F8.wireOp",EDGE,"E166"),sQuery(id+"F8.wireOp",EDGE,"E167"),sQuery(id+"F8.wireOp",EDGE,"E168"),sQuery(id+"F8.wireOp",EDGE,"E169"),sQuery(id+"F8.wireOp",EDGE,"E170"),sQuery(id+"F8.wireOp",EDGE,"E171"),sQuery(id+"F8.wireOp",EDGE,"E172"),sQuery(id+"F8.wireOp",EDGE,"E173"),sQuery(id+"F8.wireOp",EDGE,"E174"),sQuery(id+"F8.wireOp",EDGE,"E175"),sQuery(id+"F8.wireOp",EDGE,"E176"),sQuery(id+"F8.wireOp",EDGE,"E177"),sQuery(id+"F8.wireOp",EDGE,"E178"),sQuery(id+"F8.wireOp",EDGE,"E179"),sQuery(id+"F8.wireOp",EDGE,"E180"),sQuery(id+"F8.wireOp",EDGE,"E181"),sQuery(id+"F8.wireOp",EDGE,"E182"),sQuery(id+"F8.wireOp",EDGE,"E183"),sQuery(id+"F8.wireOp",EDGE,"E184"),sQuery(id+"F8.wireOp",EDGE,"E185"),sQuery(id+"F8.wireOp",EDGE,"E186"),sQuery(id+"F8.wireOp",EDGE,"E187"),sQuery(id+"F8.wireOp",EDGE,"E188"),sQuery(id+"F8.wireOp",EDGE,"E189"),sQuery(id+"F8.wireOp",EDGE,"E190"),sQuery(id+"F8.wireOp",EDGE,"E191"),sQuery(id+"F8.wireOp",EDGE,"E192"),sQuery(id+"F8.wireOp",EDGE,"E193"),sQuery(id+"F8.wireOp",EDGE,"E194"),sQuery(id+"F8.wireOp",EDGE,"E195"),sQuery(id+"F8.wireOp",EDGE,"E196"),sQuery(id+"F8.wireOp",EDGE,"E197"),sQuery(id+"F8.wireOp",EDGE,"E198"),sQuery(id+"F8.wireOp",EDGE,"E199"),sQuery(id+"F8.wireOp",EDGE,"E200"),sQuery(id+"F8.wireOp",EDGE,"E201"),sQuery(id+"F8.wireOp",EDGE,"E202"),sQuery(id+"F8.wireOp",EDGE,"E203"),sQuery(id+"F8.wireOp",EDGE,"E204"),sQuery(id+"F8.wireOp",EDGE,"E205"),sQuery(id+"F8.wireOp",EDGE,"E206"),sQuery(id+"F8.wireOp",EDGE,"E207"),sQuery(id+"F8.wireOp",EDGE,"E208"),sQuery(id+"F8.wireOp",EDGE,"E209"),sQuery(id+"F8.wireOp",EDGE,"E210"),sQuery(id+"F8.wireOp",EDGE,"E211"),sQuery(id+"F8.wireOp",EDGE,"E212"),sQuery(id+"F8.wireOp",EDGE,"E213"),sQuery(id+"F8.wireOp",EDGE,"E214"),sQuery(id+"F8.wireOp",EDGE,"E215"),sQuery(id+"F8.wireOp",EDGE,"E216"),sQuery(id+"F8.wireOp",EDGE,"E217"),sQuery(id+"F8.wireOp",EDGE,"E218"),sQuery(id+"F8.wireOp",EDGE,"E219"),sQuery(id+"F8.wireOp",EDGE,"E220"),sQuery(id+"F8.wireOp",EDGE,"E221"),sQuery(id+"F8.wireOp",EDGE,"E222"),sQuery(id+"F8.wireOp",EDGE,"E223"),sQuery(id+"F8.wireOp",EDGE,"E224"),sQuery(id+"F8.wireOp",EDGE,"E225"),sQuery(id+"F8.wireOp",EDGE,"E226"),sQuery(id+"F8.wireOp",EDGE,"E227"),sQuery(id+"F8.wireOp",EDGE,"E228"),sQuery(id+"F8.wireOp",EDGE,"E229"),sQuery(id+"F8.wireOp",EDGE,"E230"),sQuery(id+"F8.wireOp",EDGE,"E231"),sQuery(id+"F8.wireOp",EDGE,"E232"),sQuery(id+"F8.wireOp",EDGE,"E233"),sQuery(id+"F8.wireOp",EDGE,"E234"),sQuery(id+"F8.wireOp",EDGE,"E235"),sQuery(id+"F8.wireOp",EDGE,"E236")])]});
            var Q2;
            Q2=makeQuery(id+"F9.opExtrude","SWEPT_BODY",BODY,{"disambiguationData":[OSD([sQuery(id+"F8.wireOp",EDGE,"E111"),sQuery(id+"F8.wireOp",EDGE,"E112"),sQuery(id+"F8.wireOp",EDGE,"E113"),sQuery(id+"F8.wireOp",EDGE,"E114"),sQuery(id+"F8.wireOp",EDGE,"E115"),sQuery(id+"F8.wireOp",EDGE,"E116"),sQuery(id+"F8.wireOp",EDGE,"E117"),sQuery(id+"F8.wireOp",EDGE,"E118"),sQuery(id+"F8.wireOp",EDGE,"E119"),sQuery(id+"F8.wireOp",EDGE,"E120"),sQuery(id+"F8.wireOp",EDGE,"E121"),sQuery(id+"F8.wireOp",EDGE,"E122"),sQuery(id+"F8.wireOp",EDGE,"E123"),sQuery(id+"F8.wireOp",EDGE,"E124"),sQuery(id+"F8.wireOp",EDGE,"E125"),sQuery(id+"F8.wireOp",EDGE,"E126"),sQuery(id+"F8.wireOp",EDGE,"E127"),sQuery(id+"F8.wireOp",EDGE,"E128"),sQuery(id+"F8.wireOp",EDGE,"E129"),sQuery(id+"F8.wireOp",EDGE,"E130"),sQuery(id+"F8.wireOp",EDGE,"E131"),sQuery(id+"F8.wireOp",EDGE,"E132"),sQuery(id+"F8.wireOp",EDGE,"E133"),sQuery(id+"F8.wireOp",EDGE,"E134"),sQuery(id+"F8.wireOp",EDGE,"E135"),sQuery(id+"F8.wireOp",EDGE,"E136"),sQuery(id+"F8.wireOp",EDGE,"E137"),sQuery(id+"F8.wireOp",EDGE,"E138"),sQuery(id+"F8.wireOp",EDGE,"E139"),sQuery(id+"F8.wireOp",EDGE,"E140"),sQuery(id+"F8.wireOp",EDGE,"E141"),sQuery(id+"F8.wireOp",EDGE,"E142")])]});
            var Q3;
            Q3=makeQuery(id+"F9.opExtrude","SWEPT_BODY",BODY,{"disambiguationData":[OSD([sQuery(id+"F8.wireOp",EDGE,"E4"),sQuery(id+"F8.wireOp",EDGE,"E5"),sQuery(id+"F8.wireOp",EDGE,"E6"),sQuery(id+"F8.wireOp",EDGE,"E7"),sQuery(id+"F8.wireOp",EDGE,"E8"),sQuery(id+"F8.wireOp",EDGE,"E9"),sQuery(id+"F8.wireOp",EDGE,"E10"),sQuery(id+"F8.wireOp",EDGE,"E11"),sQuery(id+"F8.wireOp",EDGE,"E12"),sQuery(id+"F8.wireOp",EDGE,"E13"),sQuery(id+"F8.wireOp",EDGE,"E14"),sQuery(id+"F8.wireOp",EDGE,"E15"),sQuery(id+"F8.wireOp",EDGE,"E16"),sQuery(id+"F8.wireOp",EDGE,"E17"),sQuery(id+"F8.wireOp",EDGE,"E18"),sQuery(id+"F8.wireOp",EDGE,"E19"),sQuery(id+"F8.wireOp",EDGE,"E20"),sQuery(id+"F8.wireOp",EDGE,"E21"),sQuery(id+"F8.wireOp",EDGE,"E22"),sQuery(id+"F8.wireOp",EDGE,"E23"),sQuery(id+"F8.wireOp",EDGE,"E24"),sQuery(id+"F8.wireOp",EDGE,"E25"),sQuery(id+"F8.wireOp",EDGE,"E26"),sQuery(id+"F8.wireOp",EDGE,"E27"),sQuery(id+"F8.wireOp",EDGE,"E28"),sQuery(id+"F8.wireOp",EDGE,"E29"),sQuery(id+"F8.wireOp",EDGE,"E30"),sQuery(id+"F8.wireOp",EDGE,"E31"),sQuery(id+"F8.wireOp",EDGE,"E32"),sQuery(id+"F8.wireOp",EDGE,"E33"),sQuery(id+"F8.wireOp",EDGE,"E34"),sQuery(id+"F8.wireOp",EDGE,"E35"),sQuery(id+"F8.wireOp",EDGE,"E36"),sQuery(id+"F8.wireOp",EDGE,"E37"),sQuery(id+"F8.wireOp",EDGE,"E38"),sQuery(id+"F8.wireOp",EDGE,"E39"),sQuery(id+"F8.wireOp",EDGE,"E40"),sQuery(id+"F8.wireOp",EDGE,"E41"),sQuery(id+"F8.wireOp",EDGE,"E42"),sQuery(id+"F8.wireOp",EDGE,"E43"),sQuery(id+"F8.wireOp",EDGE,"E44"),sQuery(id+"F8.wireOp",EDGE,"E45"),sQuery(id+"F8.wireOp",EDGE,"E46"),sQuery(id+"F8.wireOp",EDGE,"E47"),sQuery(id+"F8.wireOp",EDGE,"E48"),sQuery(id+"F8.wireOp",EDGE,"E49"),sQuery(id+"F8.wireOp",EDGE,"E50"),sQuery(id+"F8.wireOp",EDGE,"E51"),sQuery(id+"F8.wireOp",EDGE,"E52"),sQuery(id+"F8.wireOp",EDGE,"E53"),sQuery(id+"F8.wireOp",EDGE,"E54"),sQuery(id+"F8.wireOp",EDGE,"E55"),sQuery(id+"F8.wireOp",EDGE,"E56"),sQuery(id+"F8.wireOp",EDGE,"E57"),sQuery(id+"F8.wireOp",EDGE,"E58"),sQuery(id+"F8.wireOp",EDGE,"E59"),sQuery(id+"F8.wireOp",EDGE,"E60"),sQuery(id+"F8.wireOp",EDGE,"E61"),sQuery(id+"F8.wireOp",EDGE,"E62"),sQuery(id+"F8.wireOp",EDGE,"E63"),sQuery(id+"F8.wireOp",EDGE,"E64"),sQuery(id+"F8.wireOp",EDGE,"E65"),sQuery(id+"F8.wireOp",EDGE,"E66"),sQuery(id+"F8.wireOp",EDGE,"E67"),sQuery(id+"F8.wireOp",EDGE,"E68"),sQuery(id+"F8.wireOp",EDGE,"E69"),sQuery(id+"F8.wireOp",EDGE,"E70"),sQuery(id+"F8.wireOp",EDGE,"E71"),sQuery(id+"F8.wireOp",EDGE,"E72"),sQuery(id+"F8.wireOp",EDGE,"E73"),sQuery(id+"F8.wireOp",EDGE,"E74"),sQuery(id+"F8.wireOp",EDGE,"E75"),sQuery(id+"F8.wireOp",EDGE,"E76"),sQuery(id+"F8.wireOp",EDGE,"E77"),sQuery(id+"F8.wireOp",EDGE,"E78"),sQuery(id+"F8.wireOp",EDGE,"E79"),sQuery(id+"F8.wireOp",EDGE,"E80"),sQuery(id+"F8.wireOp",EDGE,"E81"),sQuery(id+"F8.wireOp",EDGE,"E82"),sQuery(id+"F8.wireOp",EDGE,"E83"),sQuery(id+"F8.wireOp",EDGE,"E84"),sQuery(id+"F8.wireOp",EDGE,"E85"),sQuery(id+"F8.wireOp",EDGE,"E86"),sQuery(id+"F8.wireOp",EDGE,"E87"),sQuery(id+"F8.wireOp",EDGE,"E88"),sQuery(id+"F8.wireOp",EDGE,"E89"),sQuery(id+"F8.wireOp",EDGE,"E90"),sQuery(id+"F8.wireOp",EDGE,"E91"),sQuery(id+"F8.wireOp",EDGE,"E92"),sQuery(id+"F8.wireOp",EDGE,"E93"),sQuery(id+"F8.wireOp",EDGE,"E94"),sQuery(id+"F8.wireOp",EDGE,"E95"),sQuery(id+"F8.wireOp",EDGE,"E96"),sQuery(id+"F8.wireOp",EDGE,"E97"),sQuery(id+"F8.wireOp",EDGE,"E98"),sQuery(id+"F8.wireOp",EDGE,"E99"),sQuery(id+"F8.wireOp",EDGE,"E100"),sQuery(id+"F8.wireOp",EDGE,"E100"),sQuery(id+"F8.wireOp",EDGE,"E100"),sQuery(id+"F8.wireOp",EDGE,"E101"),sQuery(id+"F8.wireOp",EDGE,"E102"),sQuery(id+"F8.wireOp",EDGE,"E102"),sQuery(id+"F8.wireOp",EDGE,"E102"),sQuery(id+"F8.wireOp",EDGE,"E102"),sQuery(id+"F8.wireOp",EDGE,"E103"),sQuery(id+"F8.wireOp",EDGE,"E104"),sQuery(id+"F8.wireOp",EDGE,"E105"),sQuery(id+"F8.wireOp",EDGE,"E106"),sQuery(id+"F8.wireOp",EDGE,"E107"),sQuery(id+"F8.wireOp",EDGE,"E108"),sQuery(id+"F8.wireOp",EDGE,"E109"),sQuery(id+"F8.wireOp",EDGE,"E110")])]});
            transform(context, id + "F11", {"entities" : qUnion([Q0, Q1, Q2, Q3]), "transformType" : TransformType.TRANSLATION_3D, "dx" : 0 * mm, "dy" : -9.4 * mm, "dz" : 12.2 * mm, "makeCopy" : false});
        }
        {
            var Q0;
            Q0=makeQuery(id+"F9.opExtrude","SWEPT_BODY",BODY,{"disambiguationData":[OSD([sQuery(id+"F8.wireOp",EDGE,"E143"),sQuery(id+"F8.wireOp",EDGE,"E144"),sQuery(id+"F8.wireOp",EDGE,"E145"),sQuery(id+"F8.wireOp",EDGE,"E146"),sQuery(id+"F8.wireOp",EDGE,"E147"),sQuery(id+"F8.wireOp",EDGE,"E148"),sQuery(id+"F8.wireOp",EDGE,"E149"),sQuery(id+"F8.wireOp",EDGE,"E150"),sQuery(id+"F8.wireOp",EDGE,"E151"),sQuery(id+"F8.wireOp",EDGE,"E152"),sQuery(id+"F8.wireOp",EDGE,"E153"),sQuery(id+"F8.wireOp",EDGE,"E154"),sQuery(id+"F8.wireOp",EDGE,"E155"),sQuery(id+"F8.wireOp",EDGE,"E156"),sQuery(id+"F8.wireOp",EDGE,"E156"),sQuery(id+"F8.wireOp",EDGE,"E156"),sQuery(id+"F8.wireOp",EDGE,"E157"),sQuery(id+"F8.wireOp",EDGE,"E158"),sQuery(id+"F8.wireOp",EDGE,"E159"),sQuery(id+"F8.wireOp",EDGE,"E160"),sQuery(id+"F8.wireOp",EDGE,"E161"),sQuery(id+"F8.wireOp",EDGE,"E162"),sQuery(id+"F8.wireOp",EDGE,"E163"),sQuery(id+"F8.wireOp",EDGE,"E164"),sQuery(id+"F8.wireOp",EDGE,"E165"),sQuery(id+"F8.wireOp",EDGE,"E166"),sQuery(id+"F8.wireOp",EDGE,"E167"),sQuery(id+"F8.wireOp",EDGE,"E168"),sQuery(id+"F8.wireOp",EDGE,"E169"),sQuery(id+"F8.wireOp",EDGE,"E170"),sQuery(id+"F8.wireOp",EDGE,"E171"),sQuery(id+"F8.wireOp",EDGE,"E172"),sQuery(id+"F8.wireOp",EDGE,"E173"),sQuery(id+"F8.wireOp",EDGE,"E174"),sQuery(id+"F8.wireOp",EDGE,"E175"),sQuery(id+"F8.wireOp",EDGE,"E176"),sQuery(id+"F8.wireOp",EDGE,"E177"),sQuery(id+"F8.wireOp",EDGE,"E178"),sQuery(id+"F8.wireOp",EDGE,"E179"),sQuery(id+"F8.wireOp",EDGE,"E180"),sQuery(id+"F8.wireOp",EDGE,"E181"),sQuery(id+"F8.wireOp",EDGE,"E182"),sQuery(id+"F8.wireOp",EDGE,"E183"),sQuery(id+"F8.wireOp",EDGE,"E184"),sQuery(id+"F8.wireOp",EDGE,"E185"),sQuery(id+"F8.wireOp",EDGE,"E186"),sQuery(id+"F8.wireOp",EDGE,"E187"),sQuery(id+"F8.wireOp",EDGE,"E188"),sQuery(id+"F8.wireOp",EDGE,"E189"),sQuery(id+"F8.wireOp",EDGE,"E190"),sQuery(id+"F8.wireOp",EDGE,"E191"),sQuery(id+"F8.wireOp",EDGE,"E192"),sQuery(id+"F8.wireOp",EDGE,"E193"),sQuery(id+"F8.wireOp",EDGE,"E194"),sQuery(id+"F8.wireOp",EDGE,"E195"),sQuery(id+"F8.wireOp",EDGE,"E196"),sQuery(id+"F8.wireOp",EDGE,"E197"),sQuery(id+"F8.wireOp",EDGE,"E198"),sQuery(id+"F8.wireOp",EDGE,"E199"),sQuery(id+"F8.wireOp",EDGE,"E200"),sQuery(id+"F8.wireOp",EDGE,"E201"),sQuery(id+"F8.wireOp",EDGE,"E202"),sQuery(id+"F8.wireOp",EDGE,"E203"),sQuery(id+"F8.wireOp",EDGE,"E204"),sQuery(id+"F8.wireOp",EDGE,"E205"),sQuery(id+"F8.wireOp",EDGE,"E206"),sQuery(id+"F8.wireOp",EDGE,"E207"),sQuery(id+"F8.wireOp",EDGE,"E208"),sQuery(id+"F8.wireOp",EDGE,"E209"),sQuery(id+"F8.wireOp",EDGE,"E210"),sQuery(id+"F8.wireOp",EDGE,"E211"),sQuery(id+"F8.wireOp",EDGE,"E212"),sQuery(id+"F8.wireOp",EDGE,"E213"),sQuery(id+"F8.wireOp",EDGE,"E214"),sQuery(id+"F8.wireOp",EDGE,"E215"),sQuery(id+"F8.wireOp",EDGE,"E216"),sQuery(id+"F8.wireOp",EDGE,"E217"),sQuery(id+"F8.wireOp",EDGE,"E218"),sQuery(id+"F8.wireOp",EDGE,"E219"),sQuery(id+"F8.wireOp",EDGE,"E220"),sQuery(id+"F8.wireOp",EDGE,"E221"),sQuery(id+"F8.wireOp",EDGE,"E222"),sQuery(id+"F8.wireOp",EDGE,"E223"),sQuery(id+"F8.wireOp",EDGE,"E224"),sQuery(id+"F8.wireOp",EDGE,"E225"),sQuery(id+"F8.wireOp",EDGE,"E226"),sQuery(id+"F8.wireOp",EDGE,"E227"),sQuery(id+"F8.wireOp",EDGE,"E228"),sQuery(id+"F8.wireOp",EDGE,"E229"),sQuery(id+"F8.wireOp",EDGE,"E230"),sQuery(id+"F8.wireOp",EDGE,"E231"),sQuery(id+"F8.wireOp",EDGE,"E232"),sQuery(id+"F8.wireOp",EDGE,"E233"),sQuery(id+"F8.wireOp",EDGE,"E234"),sQuery(id+"F8.wireOp",EDGE,"E235"),sQuery(id+"F8.wireOp",EDGE,"E236")])]});
            var Q1;
            Q1=makeQuery(id+"F9.opExtrude","SWEPT_BODY",BODY,{"disambiguationData":[OSD([sQuery(id+"F8.wireOp",EDGE,"E111"),sQuery(id+"F8.wireOp",EDGE,"E112"),sQuery(id+"F8.wireOp",EDGE,"E113"),sQuery(id+"F8.wireOp",EDGE,"E114"),sQuery(id+"F8.wireOp",EDGE,"E115"),sQuery(id+"F8.wireOp",EDGE,"E116"),sQuery(id+"F8.wireOp",EDGE,"E117"),sQuery(id+"F8.wireOp",EDGE,"E118"),sQuery(id+"F8.wireOp",EDGE,"E119"),sQuery(id+"F8.wireOp",EDGE,"E120"),sQuery(id+"F8.wireOp",EDGE,"E121"),sQuery(id+"F8.wireOp",EDGE,"E122"),sQuery(id+"F8.wireOp",EDGE,"E123"),sQuery(id+"F8.wireOp",EDGE,"E124"),sQuery(id+"F8.wireOp",EDGE,"E125"),sQuery(id+"F8.wireOp",EDGE,"E126"),sQuery(id+"F8.wireOp",EDGE,"E127"),sQuery(id+"F8.wireOp",EDGE,"E128"),sQuery(id+"F8.wireOp",EDGE,"E129"),sQuery(id+"F8.wireOp",EDGE,"E130"),sQuery(id+"F8.wireOp",EDGE,"E131"),sQuery(id+"F8.wireOp",EDGE,"E132"),sQuery(id+"F8.wireOp",EDGE,"E133"),sQuery(id+"F8.wireOp",EDGE,"E134"),sQuery(id+"F8.wireOp",EDGE,"E135"),sQuery(id+"F8.wireOp",EDGE,"E136"),sQuery(id+"F8.wireOp",EDGE,"E137"),sQuery(id+"F8.wireOp",EDGE,"E138"),sQuery(id+"F8.wireOp",EDGE,"E139"),sQuery(id+"F8.wireOp",EDGE,"E140"),sQuery(id+"F8.wireOp",EDGE,"E141"),sQuery(id+"F8.wireOp",EDGE,"E142")])]});
            transform(context, id + "F12", {"entities" : qUnion([Q0, Q1]), "transformType" : TransformType.TRANSLATION_3D, "dx" : 0 * mm, "dy" : -5.1 * mm, "dz" : 0 * mm, "makeCopy" : false});
        }
        {
            var Q0;
            Q0=makeQuery(id+"F9.opExtrude","SWEPT_BODY",BODY,{"disambiguationData":[OSD([sQuery(id+"F8.wireOp",EDGE,"E237"),sQuery(id+"F8.wireOp",EDGE,"E238"),sQuery(id+"F8.wireOp",EDGE,"E239"),sQuery(id+"F8.wireOp",EDGE,"E240"),sQuery(id+"F8.wireOp",EDGE,"E241"),sQuery(id+"F8.wireOp",EDGE,"E242"),sQuery(id+"F8.wireOp",EDGE,"E243"),sQuery(id+"F8.wireOp",EDGE,"E244"),sQuery(id+"F8.wireOp",EDGE,"E245"),sQuery(id+"F8.wireOp",EDGE,"E246"),sQuery(id+"F8.wireOp",EDGE,"E247"),sQuery(id+"F8.wireOp",EDGE,"E248"),sQuery(id+"F8.wireOp",EDGE,"E249"),sQuery(id+"F8.wireOp",EDGE,"E250"),sQuery(id+"F8.wireOp",EDGE,"E251"),sQuery(id+"F8.wireOp",EDGE,"E252"),sQuery(id+"F8.wireOp",EDGE,"E253"),sQuery(id+"F8.wireOp",EDGE,"E254"),sQuery(id+"F8.wireOp",EDGE,"E255"),sQuery(id+"F8.wireOp",EDGE,"E256"),sQuery(id+"F8.wireOp",EDGE,"E257"),sQuery(id+"F8.wireOp",EDGE,"E258"),sQuery(id+"F8.wireOp",EDGE,"E259"),sQuery(id+"F8.wireOp",EDGE,"E260"),sQuery(id+"F8.wireOp",EDGE,"E261"),sQuery(id+"F8.wireOp",EDGE,"E262"),sQuery(id+"F8.wireOp",EDGE,"E263"),sQuery(id+"F8.wireOp",EDGE,"E264"),sQuery(id+"F8.wireOp",EDGE,"E265"),sQuery(id+"F8.wireOp",EDGE,"E266"),sQuery(id+"F8.wireOp",EDGE,"E267"),sQuery(id+"F8.wireOp",EDGE,"E268"),sQuery(id+"F8.wireOp",EDGE,"E269"),sQuery(id+"F8.wireOp",EDGE,"E270"),sQuery(id+"F8.wireOp",EDGE,"E271"),sQuery(id+"F8.wireOp",EDGE,"E272"),sQuery(id+"F8.wireOp",EDGE,"E273"),sQuery(id+"F8.wireOp",EDGE,"E274"),sQuery(id+"F8.wireOp",EDGE,"E275"),sQuery(id+"F8.wireOp",EDGE,"E276"),sQuery(id+"F8.wireOp",EDGE,"E277"),sQuery(id+"F8.wireOp",EDGE,"E278"),sQuery(id+"F8.wireOp",EDGE,"E279"),sQuery(id+"F8.wireOp",EDGE,"E280"),sQuery(id+"F8.wireOp",EDGE,"E281"),sQuery(id+"F8.wireOp",EDGE,"E282"),sQuery(id+"F8.wireOp",EDGE,"E283"),sQuery(id+"F8.wireOp",EDGE,"E284"),sQuery(id+"F8.wireOp",EDGE,"E285"),sQuery(id+"F8.wireOp",EDGE,"E286"),sQuery(id+"F8.wireOp",EDGE,"E287"),sQuery(id+"F8.wireOp",EDGE,"E288"),sQuery(id+"F8.wireOp",EDGE,"E289"),sQuery(id+"F8.wireOp",EDGE,"E290"),sQuery(id+"F8.wireOp",EDGE,"E291"),sQuery(id+"F8.wireOp",EDGE,"E292"),sQuery(id+"F8.wireOp",EDGE,"E293"),sQuery(id+"F8.wireOp",EDGE,"E294"),sQuery(id+"F8.wireOp",EDGE,"E295"),sQuery(id+"F8.wireOp",EDGE,"E296"),sQuery(id+"F8.wireOp",EDGE,"E297"),sQuery(id+"F8.wireOp",EDGE,"E298"),sQuery(id+"F8.wireOp",EDGE,"E299"),sQuery(id+"F8.wireOp",EDGE,"E300"),sQuery(id+"F8.wireOp",EDGE,"E301"),sQuery(id+"F8.wireOp",EDGE,"E302"),sQuery(id+"F8.wireOp",EDGE,"E303"),sQuery(id+"F8.wireOp",EDGE,"E304"),sQuery(id+"F8.wireOp",EDGE,"E305"),sQuery(id+"F8.wireOp",EDGE,"E306"),sQuery(id+"F8.wireOp",EDGE,"E307"),sQuery(id+"F8.wireOp",EDGE,"E308"),sQuery(id+"F8.wireOp",EDGE,"E309"),sQuery(id+"F8.wireOp",EDGE,"E310"),sQuery(id+"F8.wireOp",EDGE,"E311"),sQuery(id+"F8.wireOp",EDGE,"E312"),sQuery(id+"F8.wireOp",EDGE,"E313"),sQuery(id+"F8.wireOp",EDGE,"E314"),sQuery(id+"F8.wireOp",EDGE,"E315"),sQuery(id+"F8.wireOp",EDGE,"E316"),sQuery(id+"F8.wireOp",EDGE,"E317"),sQuery(id+"F8.wireOp",EDGE,"E318"),sQuery(id+"F8.wireOp",EDGE,"E319"),sQuery(id+"F8.wireOp",EDGE,"E320"),sQuery(id+"F8.wireOp",EDGE,"E321"),sQuery(id+"F8.wireOp",EDGE,"E322"),sQuery(id+"F8.wireOp",EDGE,"E323"),sQuery(id+"F8.wireOp",EDGE,"E324"),sQuery(id+"F8.wireOp",EDGE,"E325"),sQuery(id+"F8.wireOp",EDGE,"E326"),sQuery(id+"F8.wireOp",EDGE,"E327"),sQuery(id+"F8.wireOp",EDGE,"E328"),sQuery(id+"F8.wireOp",EDGE,"E329"),sQuery(id+"F8.wireOp",EDGE,"E330"),sQuery(id+"F8.wireOp",EDGE,"E331"),sQuery(id+"F8.wireOp",EDGE,"E332"),sQuery(id+"F8.wireOp",EDGE,"E333"),sQuery(id+"F8.wireOp",EDGE,"E334"),sQuery(id+"F8.wireOp",EDGE,"E335"),sQuery(id+"F8.wireOp",EDGE,"E336"),sQuery(id+"F8.wireOp",EDGE,"E337"),sQuery(id+"F8.wireOp",EDGE,"E338"),sQuery(id+"F8.wireOp",EDGE,"E339"),sQuery(id+"F8.wireOp",EDGE,"E340"),sQuery(id+"F8.wireOp",EDGE,"E341"),sQuery(id+"F8.wireOp",EDGE,"E342"),sQuery(id+"F8.wireOp",EDGE,"E343"),sQuery(id+"F8.wireOp",EDGE,"E344"),sQuery(id+"F8.wireOp",EDGE,"E345"),sQuery(id+"F8.wireOp",EDGE,"E346"),sQuery(id+"F8.wireOp",EDGE,"E347"),sQuery(id+"F8.wireOp",EDGE,"E348"),sQuery(id+"F8.wireOp",EDGE,"E349"),sQuery(id+"F8.wireOp",EDGE,"E350"),sQuery(id+"F8.wireOp",EDGE,"E351"),sQuery(id+"F8.wireOp",EDGE,"E352"),sQuery(id+"F8.wireOp",EDGE,"E353"),sQuery(id+"F8.wireOp",EDGE,"E354"),sQuery(id+"F8.wireOp",EDGE,"E355"),sQuery(id+"F8.wireOp",EDGE,"E356"),sQuery(id+"F8.wireOp",EDGE,"E357"),sQuery(id+"F8.wireOp",EDGE,"E358"),sQuery(id+"F8.wireOp",EDGE,"E359"),sQuery(id+"F8.wireOp",EDGE,"E360"),sQuery(id+"F8.wireOp",EDGE,"E361"),sQuery(id+"F8.wireOp",EDGE,"E362"),sQuery(id+"F8.wireOp",EDGE,"E363"),sQuery(id+"F8.wireOp",EDGE,"E364"),sQuery(id+"F8.wireOp",EDGE,"E365"),sQuery(id+"F8.wireOp",EDGE,"E366"),sQuery(id+"F8.wireOp",EDGE,"E367"),sQuery(id+"F8.wireOp",EDGE,"E368"),sQuery(id+"F8.wireOp",EDGE,"E369"),sQuery(id+"F8.wireOp",EDGE,"E370"),sQuery(id+"F8.wireOp",EDGE,"E371"),sQuery(id+"F8.wireOp",EDGE,"E372"),sQuery(id+"F8.wireOp",EDGE,"E373"),sQuery(id+"F8.wireOp",EDGE,"E374"),sQuery(id+"F8.wireOp",EDGE,"E375"),sQuery(id+"F8.wireOp",EDGE,"E376"),sQuery(id+"F8.wireOp",EDGE,"E377"),sQuery(id+"F8.wireOp",EDGE,"E378"),sQuery(id+"F8.wireOp",EDGE,"E379"),sQuery(id+"F8.wireOp",EDGE,"E380"),sQuery(id+"F8.wireOp",EDGE,"E381"),sQuery(id+"F8.wireOp",EDGE,"E382"),sQuery(id+"F8.wireOp",EDGE,"E383"),sQuery(id+"F8.wireOp",EDGE,"E384"),sQuery(id+"F8.wireOp",EDGE,"E385"),sQuery(id+"F8.wireOp",EDGE,"E386"),sQuery(id+"F8.wireOp",EDGE,"E387"),sQuery(id+"F8.wireOp",EDGE,"E388"),sQuery(id+"F8.wireOp",EDGE,"E389"),sQuery(id+"F8.wireOp",EDGE,"E390"),sQuery(id+"F8.wireOp",EDGE,"E391"),sQuery(id+"F8.wireOp",EDGE,"E392"),sQuery(id+"F8.wireOp",EDGE,"E393"),sQuery(id+"F8.wireOp",EDGE,"E394"),sQuery(id+"F8.wireOp",EDGE,"E395"),sQuery(id+"F8.wireOp",EDGE,"E396")])]});
            var Q1;
            Q1=makeQuery(id+"F9.opExtrude","SWEPT_BODY",BODY,{"disambiguationData":[OSD([sQuery(id+"F8.wireOp",EDGE,"E143"),sQuery(id+"F8.wireOp",EDGE,"E144"),sQuery(id+"F8.wireOp",EDGE,"E145"),sQuery(id+"F8.wireOp",EDGE,"E146"),sQuery(id+"F8.wireOp",EDGE,"E147"),sQuery(id+"F8.wireOp",EDGE,"E148"),sQuery(id+"F8.wireOp",EDGE,"E149"),sQuery(id+"F8.wireOp",EDGE,"E150"),sQuery(id+"F8.wireOp",EDGE,"E151"),sQuery(id+"F8.wireOp",EDGE,"E152"),sQuery(id+"F8.wireOp",EDGE,"E153"),sQuery(id+"F8.wireOp",EDGE,"E154"),sQuery(id+"F8.wireOp",EDGE,"E155"),sQuery(id+"F8.wireOp",EDGE,"E156"),sQuery(id+"F8.wireOp",EDGE,"E156"),sQuery(id+"F8.wireOp",EDGE,"E156"),sQuery(id+"F8.wireOp",EDGE,"E157"),sQuery(id+"F8.wireOp",EDGE,"E158"),sQuery(id+"F8.wireOp",EDGE,"E159"),sQuery(id+"F8.wireOp",EDGE,"E160"),sQuery(id+"F8.wireOp",EDGE,"E161"),sQuery(id+"F8.wireOp",EDGE,"E162"),sQuery(id+"F8.wireOp",EDGE,"E163"),sQuery(id+"F8.wireOp",EDGE,"E164"),sQuery(id+"F8.wireOp",EDGE,"E165"),sQuery(id+"F8.wireOp",EDGE,"E166"),sQuery(id+"F8.wireOp",EDGE,"E167"),sQuery(id+"F8.wireOp",EDGE,"E168"),sQuery(id+"F8.wireOp",EDGE,"E169"),sQuery(id+"F8.wireOp",EDGE,"E170"),sQuery(id+"F8.wireOp",EDGE,"E171"),sQuery(id+"F8.wireOp",EDGE,"E172"),sQuery(id+"F8.wireOp",EDGE,"E173"),sQuery(id+"F8.wireOp",EDGE,"E174"),sQuery(id+"F8.wireOp",EDGE,"E175"),sQuery(id+"F8.wireOp",EDGE,"E176"),sQuery(id+"F8.wireOp",EDGE,"E177"),sQuery(id+"F8.wireOp",EDGE,"E178"),sQuery(id+"F8.wireOp",EDGE,"E179"),sQuery(id+"F8.wireOp",EDGE,"E180"),sQuery(id+"F8.wireOp",EDGE,"E181"),sQuery(id+"F8.wireOp",EDGE,"E182"),sQuery(id+"F8.wireOp",EDGE,"E183"),sQuery(id+"F8.wireOp",EDGE,"E184"),sQuery(id+"F8.wireOp",EDGE,"E185"),sQuery(id+"F8.wireOp",EDGE,"E186"),sQuery(id+"F8.wireOp",EDGE,"E187"),sQuery(id+"F8.wireOp",EDGE,"E188"),sQuery(id+"F8.wireOp",EDGE,"E189"),sQuery(id+"F8.wireOp",EDGE,"E190"),sQuery(id+"F8.wireOp",EDGE,"E191"),sQuery(id+"F8.wireOp",EDGE,"E192"),sQuery(id+"F8.wireOp",EDGE,"E193"),sQuery(id+"F8.wireOp",EDGE,"E194"),sQuery(id+"F8.wireOp",EDGE,"E195"),sQuery(id+"F8.wireOp",EDGE,"E196"),sQuery(id+"F8.wireOp",EDGE,"E197"),sQuery(id+"F8.wireOp",EDGE,"E198"),sQuery(id+"F8.wireOp",EDGE,"E199"),sQuery(id+"F8.wireOp",EDGE,"E200"),sQuery(id+"F8.wireOp",EDGE,"E201"),sQuery(id+"F8.wireOp",EDGE,"E202"),sQuery(id+"F8.wireOp",EDGE,"E203"),sQuery(id+"F8.wireOp",EDGE,"E204"),sQuery(id+"F8.wireOp",EDGE,"E205"),sQuery(id+"F8.wireOp",EDGE,"E206"),sQuery(id+"F8.wireOp",EDGE,"E207"),sQuery(id+"F8.wireOp",EDGE,"E208"),sQuery(id+"F8.wireOp",EDGE,"E209"),sQuery(id+"F8.wireOp",EDGE,"E210"),sQuery(id+"F8.wireOp",EDGE,"E211"),sQuery(id+"F8.wireOp",EDGE,"E212"),sQuery(id+"F8.wireOp",EDGE,"E213"),sQuery(id+"F8.wireOp",EDGE,"E214"),sQuery(id+"F8.wireOp",EDGE,"E215"),sQuery(id+"F8.wireOp",EDGE,"E216"),sQuery(id+"F8.wireOp",EDGE,"E217"),sQuery(id+"F8.wireOp",EDGE,"E218"),sQuery(id+"F8.wireOp",EDGE,"E219"),sQuery(id+"F8.wireOp",EDGE,"E220"),sQuery(id+"F8.wireOp",EDGE,"E221"),sQuery(id+"F8.wireOp",EDGE,"E222"),sQuery(id+"F8.wireOp",EDGE,"E223"),sQuery(id+"F8.wireOp",EDGE,"E224"),sQuery(id+"F8.wireOp",EDGE,"E225"),sQuery(id+"F8.wireOp",EDGE,"E226"),sQuery(id+"F8.wireOp",EDGE,"E227"),sQuery(id+"F8.wireOp",EDGE,"E228"),sQuery(id+"F8.wireOp",EDGE,"E229"),sQuery(id+"F8.wireOp",EDGE,"E230"),sQuery(id+"F8.wireOp",EDGE,"E231"),sQuery(id+"F8.wireOp",EDGE,"E232"),sQuery(id+"F8.wireOp",EDGE,"E233"),sQuery(id+"F8.wireOp",EDGE,"E234"),sQuery(id+"F8.wireOp",EDGE,"E235"),sQuery(id+"F8.wireOp",EDGE,"E236")])]});
            var Q2;
            Q2=makeQuery(id+"F9.opExtrude","SWEPT_BODY",BODY,{"disambiguationData":[OSD([sQuery(id+"F8.wireOp",EDGE,"E111"),sQuery(id+"F8.wireOp",EDGE,"E112"),sQuery(id+"F8.wireOp",EDGE,"E113"),sQuery(id+"F8.wireOp",EDGE,"E114"),sQuery(id+"F8.wireOp",EDGE,"E115"),sQuery(id+"F8.wireOp",EDGE,"E116"),sQuery(id+"F8.wireOp",EDGE,"E117"),sQuery(id+"F8.wireOp",EDGE,"E118"),sQuery(id+"F8.wireOp",EDGE,"E119"),sQuery(id+"F8.wireOp",EDGE,"E120"),sQuery(id+"F8.wireOp",EDGE,"E121"),sQuery(id+"F8.wireOp",EDGE,"E122"),sQuery(id+"F8.wireOp",EDGE,"E123"),sQuery(id+"F8.wireOp",EDGE,"E124"),sQuery(id+"F8.wireOp",EDGE,"E125"),sQuery(id+"F8.wireOp",EDGE,"E126"),sQuery(id+"F8.wireOp",EDGE,"E127"),sQuery(id+"F8.wireOp",EDGE,"E128"),sQuery(id+"F8.wireOp",EDGE,"E129"),sQuery(id+"F8.wireOp",EDGE,"E130"),sQuery(id+"F8.wireOp",EDGE,"E131"),sQuery(id+"F8.wireOp",EDGE,"E132"),sQuery(id+"F8.wireOp",EDGE,"E133"),sQuery(id+"F8.wireOp",EDGE,"E134"),sQuery(id+"F8.wireOp",EDGE,"E135"),sQuery(id+"F8.wireOp",EDGE,"E136"),sQuery(id+"F8.wireOp",EDGE,"E137"),sQuery(id+"F8.wireOp",EDGE,"E138"),sQuery(id+"F8.wireOp",EDGE,"E139"),sQuery(id+"F8.wireOp",EDGE,"E140"),sQuery(id+"F8.wireOp",EDGE,"E141"),sQuery(id+"F8.wireOp",EDGE,"E142")])]});
            var Q3;
            Q3=makeQuery(id+"F9.opExtrude","SWEPT_BODY",BODY,{"disambiguationData":[OSD([sQuery(id+"F8.wireOp",EDGE,"E4"),sQuery(id+"F8.wireOp",EDGE,"E5"),sQuery(id+"F8.wireOp",EDGE,"E6"),sQuery(id+"F8.wireOp",EDGE,"E7"),sQuery(id+"F8.wireOp",EDGE,"E8"),sQuery(id+"F8.wireOp",EDGE,"E9"),sQuery(id+"F8.wireOp",EDGE,"E10"),sQuery(id+"F8.wireOp",EDGE,"E11"),sQuery(id+"F8.wireOp",EDGE,"E12"),sQuery(id+"F8.wireOp",EDGE,"E13"),sQuery(id+"F8.wireOp",EDGE,"E14"),sQuery(id+"F8.wireOp",EDGE,"E15"),sQuery(id+"F8.wireOp",EDGE,"E16"),sQuery(id+"F8.wireOp",EDGE,"E17"),sQuery(id+"F8.wireOp",EDGE,"E18"),sQuery(id+"F8.wireOp",EDGE,"E19"),sQuery(id+"F8.wireOp",EDGE,"E20"),sQuery(id+"F8.wireOp",EDGE,"E21"),sQuery(id+"F8.wireOp",EDGE,"E22"),sQuery(id+"F8.wireOp",EDGE,"E23"),sQuery(id+"F8.wireOp",EDGE,"E24"),sQuery(id+"F8.wireOp",EDGE,"E25"),sQuery(id+"F8.wireOp",EDGE,"E26"),sQuery(id+"F8.wireOp",EDGE,"E27"),sQuery(id+"F8.wireOp",EDGE,"E28"),sQuery(id+"F8.wireOp",EDGE,"E29"),sQuery(id+"F8.wireOp",EDGE,"E30"),sQuery(id+"F8.wireOp",EDGE,"E31"),sQuery(id+"F8.wireOp",EDGE,"E32"),sQuery(id+"F8.wireOp",EDGE,"E33"),sQuery(id+"F8.wireOp",EDGE,"E34"),sQuery(id+"F8.wireOp",EDGE,"E35"),sQuery(id+"F8.wireOp",EDGE,"E36"),sQuery(id+"F8.wireOp",EDGE,"E37"),sQuery(id+"F8.wireOp",EDGE,"E38"),sQuery(id+"F8.wireOp",EDGE,"E39"),sQuery(id+"F8.wireOp",EDGE,"E40"),sQuery(id+"F8.wireOp",EDGE,"E41"),sQuery(id+"F8.wireOp",EDGE,"E42"),sQuery(id+"F8.wireOp",EDGE,"E43"),sQuery(id+"F8.wireOp",EDGE,"E44"),sQuery(id+"F8.wireOp",EDGE,"E45"),sQuery(id+"F8.wireOp",EDGE,"E46"),sQuery(id+"F8.wireOp",EDGE,"E47"),sQuery(id+"F8.wireOp",EDGE,"E48"),sQuery(id+"F8.wireOp",EDGE,"E49"),sQuery(id+"F8.wireOp",EDGE,"E50"),sQuery(id+"F8.wireOp",EDGE,"E51"),sQuery(id+"F8.wireOp",EDGE,"E52"),sQuery(id+"F8.wireOp",EDGE,"E53"),sQuery(id+"F8.wireOp",EDGE,"E54"),sQuery(id+"F8.wireOp",EDGE,"E55"),sQuery(id+"F8.wireOp",EDGE,"E56"),sQuery(id+"F8.wireOp",EDGE,"E57"),sQuery(id+"F8.wireOp",EDGE,"E58"),sQuery(id+"F8.wireOp",EDGE,"E59"),sQuery(id+"F8.wireOp",EDGE,"E60"),sQuery(id+"F8.wireOp",EDGE,"E61"),sQuery(id+"F8.wireOp",EDGE,"E62"),sQuery(id+"F8.wireOp",EDGE,"E63"),sQuery(id+"F8.wireOp",EDGE,"E64"),sQuery(id+"F8.wireOp",EDGE,"E65"),sQuery(id+"F8.wireOp",EDGE,"E66"),sQuery(id+"F8.wireOp",EDGE,"E67"),sQuery(id+"F8.wireOp",EDGE,"E68"),sQuery(id+"F8.wireOp",EDGE,"E69"),sQuery(id+"F8.wireOp",EDGE,"E70"),sQuery(id+"F8.wireOp",EDGE,"E71"),sQuery(id+"F8.wireOp",EDGE,"E72"),sQuery(id+"F8.wireOp",EDGE,"E73"),sQuery(id+"F8.wireOp",EDGE,"E74"),sQuery(id+"F8.wireOp",EDGE,"E75"),sQuery(id+"F8.wireOp",EDGE,"E76"),sQuery(id+"F8.wireOp",EDGE,"E77"),sQuery(id+"F8.wireOp",EDGE,"E78"),sQuery(id+"F8.wireOp",EDGE,"E79"),sQuery(id+"F8.wireOp",EDGE,"E80"),sQuery(id+"F8.wireOp",EDGE,"E81"),sQuery(id+"F8.wireOp",EDGE,"E82"),sQuery(id+"F8.wireOp",EDGE,"E83"),sQuery(id+"F8.wireOp",EDGE,"E84"),sQuery(id+"F8.wireOp",EDGE,"E85"),sQuery(id+"F8.wireOp",EDGE,"E86"),sQuery(id+"F8.wireOp",EDGE,"E87"),sQuery(id+"F8.wireOp",EDGE,"E88"),sQuery(id+"F8.wireOp",EDGE,"E89"),sQuery(id+"F8.wireOp",EDGE,"E90"),sQuery(id+"F8.wireOp",EDGE,"E91"),sQuery(id+"F8.wireOp",EDGE,"E92"),sQuery(id+"F8.wireOp",EDGE,"E93"),sQuery(id+"F8.wireOp",EDGE,"E94"),sQuery(id+"F8.wireOp",EDGE,"E95"),sQuery(id+"F8.wireOp",EDGE,"E96"),sQuery(id+"F8.wireOp",EDGE,"E97"),sQuery(id+"F8.wireOp",EDGE,"E98"),sQuery(id+"F8.wireOp",EDGE,"E99"),sQuery(id+"F8.wireOp",EDGE,"E100"),sQuery(id+"F8.wireOp",EDGE,"E100"),sQuery(id+"F8.wireOp",EDGE,"E100"),sQuery(id+"F8.wireOp",EDGE,"E101"),sQuery(id+"F8.wireOp",EDGE,"E102"),sQuery(id+"F8.wireOp",EDGE,"E102"),sQuery(id+"F8.wireOp",EDGE,"E102"),sQuery(id+"F8.wireOp",EDGE,"E102"),sQuery(id+"F8.wireOp",EDGE,"E103"),sQuery(id+"F8.wireOp",EDGE,"E104"),sQuery(id+"F8.wireOp",EDGE,"E105"),sQuery(id+"F8.wireOp",EDGE,"E106"),sQuery(id+"F8.wireOp",EDGE,"E107"),sQuery(id+"F8.wireOp",EDGE,"E108"),sQuery(id+"F8.wireOp",EDGE,"E109"),sQuery(id+"F8.wireOp",EDGE,"E110")])]});
            var Q4;
            Q4=makeQuery(id+"F9.opExtrude","CAP_EDGE",EDGE,{"disambiguationData":[OSD([sQuery(id+"F8.wireOp",EDGE,"E205"),sQuery(id+"F8.wireOp",EDGE,"E206"),sQuery(id+"F8.wireOp",EDGE,"E207"),sQuery(id+"F8.wireOp",EDGE,"E208"),sQuery(id+"F8.wireOp",EDGE,"E209"),sQuery(id+"F8.wireOp",EDGE,"E210"),sQuery(id+"F8.wireOp",EDGE,"E211"),sQuery(id+"F8.wireOp",EDGE,"E212")])],"isStart":false});
            transform(context, id + "F13", {"entities" : qUnion([Q0, Q1, Q2, Q3]), "transformType" : TransformType.ROTATION, "transformAxis" : qUnion([Q4]), "angle" : 20 * degree, "oppositeDirection" : true, "makeCopy" : false});
        }
        {
            var Q0;
            Q0=makeQuery(id+"F9.opExtrude","SWEPT_BODY",BODY,{"disambiguationData":[OSD([sQuery(id+"F8.wireOp",EDGE,"E237"),sQuery(id+"F8.wireOp",EDGE,"E238"),sQuery(id+"F8.wireOp",EDGE,"E239"),sQuery(id+"F8.wireOp",EDGE,"E240"),sQuery(id+"F8.wireOp",EDGE,"E241"),sQuery(id+"F8.wireOp",EDGE,"E242"),sQuery(id+"F8.wireOp",EDGE,"E243"),sQuery(id+"F8.wireOp",EDGE,"E244"),sQuery(id+"F8.wireOp",EDGE,"E245"),sQuery(id+"F8.wireOp",EDGE,"E246"),sQuery(id+"F8.wireOp",EDGE,"E247"),sQuery(id+"F8.wireOp",EDGE,"E248"),sQuery(id+"F8.wireOp",EDGE,"E249"),sQuery(id+"F8.wireOp",EDGE,"E250"),sQuery(id+"F8.wireOp",EDGE,"E251"),sQuery(id+"F8.wireOp",EDGE,"E252"),sQuery(id+"F8.wireOp",EDGE,"E253"),sQuery(id+"F8.wireOp",EDGE,"E254"),sQuery(id+"F8.wireOp",EDGE,"E255"),sQuery(id+"F8.wireOp",EDGE,"E256"),sQuery(id+"F8.wireOp",EDGE,"E257"),sQuery(id+"F8.wireOp",EDGE,"E258"),sQuery(id+"F8.wireOp",EDGE,"E259"),sQuery(id+"F8.wireOp",EDGE,"E260"),sQuery(id+"F8.wireOp",EDGE,"E261"),sQuery(id+"F8.wireOp",EDGE,"E262"),sQuery(id+"F8.wireOp",EDGE,"E263"),sQuery(id+"F8.wireOp",EDGE,"E264"),sQuery(id+"F8.wireOp",EDGE,"E265"),sQuery(id+"F8.wireOp",EDGE,"E266"),sQuery(id+"F8.wireOp",EDGE,"E267"),sQuery(id+"F8.wireOp",EDGE,"E268"),sQuery(id+"F8.wireOp",EDGE,"E269"),sQuery(id+"F8.wireOp",EDGE,"E270"),sQuery(id+"F8.wireOp",EDGE,"E271"),sQuery(id+"F8.wireOp",EDGE,"E272"),sQuery(id+"F8.wireOp",EDGE,"E273"),sQuery(id+"F8.wireOp",EDGE,"E274"),sQuery(id+"F8.wireOp",EDGE,"E275"),sQuery(id+"F8.wireOp",EDGE,"E276"),sQuery(id+"F8.wireOp",EDGE,"E277"),sQuery(id+"F8.wireOp",EDGE,"E278"),sQuery(id+"F8.wireOp",EDGE,"E279"),sQuery(id+"F8.wireOp",EDGE,"E280"),sQuery(id+"F8.wireOp",EDGE,"E281"),sQuery(id+"F8.wireOp",EDGE,"E282"),sQuery(id+"F8.wireOp",EDGE,"E283"),sQuery(id+"F8.wireOp",EDGE,"E284"),sQuery(id+"F8.wireOp",EDGE,"E285"),sQuery(id+"F8.wireOp",EDGE,"E286"),sQuery(id+"F8.wireOp",EDGE,"E287"),sQuery(id+"F8.wireOp",EDGE,"E288"),sQuery(id+"F8.wireOp",EDGE,"E289"),sQuery(id+"F8.wireOp",EDGE,"E290"),sQuery(id+"F8.wireOp",EDGE,"E291"),sQuery(id+"F8.wireOp",EDGE,"E292"),sQuery(id+"F8.wireOp",EDGE,"E293"),sQuery(id+"F8.wireOp",EDGE,"E294"),sQuery(id+"F8.wireOp",EDGE,"E295"),sQuery(id+"F8.wireOp",EDGE,"E296"),sQuery(id+"F8.wireOp",EDGE,"E297"),sQuery(id+"F8.wireOp",EDGE,"E298"),sQuery(id+"F8.wireOp",EDGE,"E299"),sQuery(id+"F8.wireOp",EDGE,"E300"),sQuery(id+"F8.wireOp",EDGE,"E301"),sQuery(id+"F8.wireOp",EDGE,"E302"),sQuery(id+"F8.wireOp",EDGE,"E303"),sQuery(id+"F8.wireOp",EDGE,"E304"),sQuery(id+"F8.wireOp",EDGE,"E305"),sQuery(id+"F8.wireOp",EDGE,"E306"),sQuery(id+"F8.wireOp",EDGE,"E307"),sQuery(id+"F8.wireOp",EDGE,"E308"),sQuery(id+"F8.wireOp",EDGE,"E309"),sQuery(id+"F8.wireOp",EDGE,"E310"),sQuery(id+"F8.wireOp",EDGE,"E311"),sQuery(id+"F8.wireOp",EDGE,"E312"),sQuery(id+"F8.wireOp",EDGE,"E313"),sQuery(id+"F8.wireOp",EDGE,"E314"),sQuery(id+"F8.wireOp",EDGE,"E315"),sQuery(id+"F8.wireOp",EDGE,"E316"),sQuery(id+"F8.wireOp",EDGE,"E317"),sQuery(id+"F8.wireOp",EDGE,"E318"),sQuery(id+"F8.wireOp",EDGE,"E319"),sQuery(id+"F8.wireOp",EDGE,"E320"),sQuery(id+"F8.wireOp",EDGE,"E321"),sQuery(id+"F8.wireOp",EDGE,"E322"),sQuery(id+"F8.wireOp",EDGE,"E323"),sQuery(id+"F8.wireOp",EDGE,"E324"),sQuery(id+"F8.wireOp",EDGE,"E325"),sQuery(id+"F8.wireOp",EDGE,"E326"),sQuery(id+"F8.wireOp",EDGE,"E327"),sQuery(id+"F8.wireOp",EDGE,"E328"),sQuery(id+"F8.wireOp",EDGE,"E329"),sQuery(id+"F8.wireOp",EDGE,"E330"),sQuery(id+"F8.wireOp",EDGE,"E331"),sQuery(id+"F8.wireOp",EDGE,"E332"),sQuery(id+"F8.wireOp",EDGE,"E333"),sQuery(id+"F8.wireOp",EDGE,"E334"),sQuery(id+"F8.wireOp",EDGE,"E335"),sQuery(id+"F8.wireOp",EDGE,"E336"),sQuery(id+"F8.wireOp",EDGE,"E337"),sQuery(id+"F8.wireOp",EDGE,"E338"),sQuery(id+"F8.wireOp",EDGE,"E339"),sQuery(id+"F8.wireOp",EDGE,"E340"),sQuery(id+"F8.wireOp",EDGE,"E341"),sQuery(id+"F8.wireOp",EDGE,"E342"),sQuery(id+"F8.wireOp",EDGE,"E343"),sQuery(id+"F8.wireOp",EDGE,"E344"),sQuery(id+"F8.wireOp",EDGE,"E345"),sQuery(id+"F8.wireOp",EDGE,"E346"),sQuery(id+"F8.wireOp",EDGE,"E347"),sQuery(id+"F8.wireOp",EDGE,"E348"),sQuery(id+"F8.wireOp",EDGE,"E349"),sQuery(id+"F8.wireOp",EDGE,"E350"),sQuery(id+"F8.wireOp",EDGE,"E351"),sQuery(id+"F8.wireOp",EDGE,"E352"),sQuery(id+"F8.wireOp",EDGE,"E353"),sQuery(id+"F8.wireOp",EDGE,"E354"),sQuery(id+"F8.wireOp",EDGE,"E355"),sQuery(id+"F8.wireOp",EDGE,"E356"),sQuery(id+"F8.wireOp",EDGE,"E357"),sQuery(id+"F8.wireOp",EDGE,"E358"),sQuery(id+"F8.wireOp",EDGE,"E359"),sQuery(id+"F8.wireOp",EDGE,"E360"),sQuery(id+"F8.wireOp",EDGE,"E361"),sQuery(id+"F8.wireOp",EDGE,"E362"),sQuery(id+"F8.wireOp",EDGE,"E363"),sQuery(id+"F8.wireOp",EDGE,"E364"),sQuery(id+"F8.wireOp",EDGE,"E365"),sQuery(id+"F8.wireOp",EDGE,"E366"),sQuery(id+"F8.wireOp",EDGE,"E367"),sQuery(id+"F8.wireOp",EDGE,"E368"),sQuery(id+"F8.wireOp",EDGE,"E369"),sQuery(id+"F8.wireOp",EDGE,"E370"),sQuery(id+"F8.wireOp",EDGE,"E371"),sQuery(id+"F8.wireOp",EDGE,"E372"),sQuery(id+"F8.wireOp",EDGE,"E373"),sQuery(id+"F8.wireOp",EDGE,"E374"),sQuery(id+"F8.wireOp",EDGE,"E375"),sQuery(id+"F8.wireOp",EDGE,"E376"),sQuery(id+"F8.wireOp",EDGE,"E377"),sQuery(id+"F8.wireOp",EDGE,"E378"),sQuery(id+"F8.wireOp",EDGE,"E379"),sQuery(id+"F8.wireOp",EDGE,"E380"),sQuery(id+"F8.wireOp",EDGE,"E381"),sQuery(id+"F8.wireOp",EDGE,"E382"),sQuery(id+"F8.wireOp",EDGE,"E383"),sQuery(id+"F8.wireOp",EDGE,"E384"),sQuery(id+"F8.wireOp",EDGE,"E385"),sQuery(id+"F8.wireOp",EDGE,"E386"),sQuery(id+"F8.wireOp",EDGE,"E387"),sQuery(id+"F8.wireOp",EDGE,"E388"),sQuery(id+"F8.wireOp",EDGE,"E389"),sQuery(id+"F8.wireOp",EDGE,"E390"),sQuery(id+"F8.wireOp",EDGE,"E391"),sQuery(id+"F8.wireOp",EDGE,"E392"),sQuery(id+"F8.wireOp",EDGE,"E393"),sQuery(id+"F8.wireOp",EDGE,"E394"),sQuery(id+"F8.wireOp",EDGE,"E395"),sQuery(id+"F8.wireOp",EDGE,"E396")])]});
            var Q1;
            Q1=makeQuery(id+"F9.opExtrude","CAP_EDGE",EDGE,{"disambiguationData":[OSD([sQuery(id+"F8.wireOp",EDGE,"E336")])],"isStart":true});
            transform(context, id + "F14", {"entities" : qUnion([Q0]), "transformType" : TransformType.ROTATION, "transformAxis" : qUnion([Q1]), "angle" : 15 * degree, "makeCopy" : false});
        }
        {
            var Q0;
            Q0=makeQuery(id+"F9.opExtrude","SWEPT_BODY",BODY,{"disambiguationData":[OSD([sQuery(id+"F8.wireOp",EDGE,"E237"),sQuery(id+"F8.wireOp",EDGE,"E238"),sQuery(id+"F8.wireOp",EDGE,"E239"),sQuery(id+"F8.wireOp",EDGE,"E240"),sQuery(id+"F8.wireOp",EDGE,"E241"),sQuery(id+"F8.wireOp",EDGE,"E242"),sQuery(id+"F8.wireOp",EDGE,"E243"),sQuery(id+"F8.wireOp",EDGE,"E244"),sQuery(id+"F8.wireOp",EDGE,"E245"),sQuery(id+"F8.wireOp",EDGE,"E246"),sQuery(id+"F8.wireOp",EDGE,"E247"),sQuery(id+"F8.wireOp",EDGE,"E248"),sQuery(id+"F8.wireOp",EDGE,"E249"),sQuery(id+"F8.wireOp",EDGE,"E250"),sQuery(id+"F8.wireOp",EDGE,"E251"),sQuery(id+"F8.wireOp",EDGE,"E252"),sQuery(id+"F8.wireOp",EDGE,"E253"),sQuery(id+"F8.wireOp",EDGE,"E254"),sQuery(id+"F8.wireOp",EDGE,"E255"),sQuery(id+"F8.wireOp",EDGE,"E256"),sQuery(id+"F8.wireOp",EDGE,"E257"),sQuery(id+"F8.wireOp",EDGE,"E258"),sQuery(id+"F8.wireOp",EDGE,"E259"),sQuery(id+"F8.wireOp",EDGE,"E260"),sQuery(id+"F8.wireOp",EDGE,"E261"),sQuery(id+"F8.wireOp",EDGE,"E262"),sQuery(id+"F8.wireOp",EDGE,"E263"),sQuery(id+"F8.wireOp",EDGE,"E264"),sQuery(id+"F8.wireOp",EDGE,"E265"),sQuery(id+"F8.wireOp",EDGE,"E266"),sQuery(id+"F8.wireOp",EDGE,"E267"),sQuery(id+"F8.wireOp",EDGE,"E268"),sQuery(id+"F8.wireOp",EDGE,"E269"),sQuery(id+"F8.wireOp",EDGE,"E270"),sQuery(id+"F8.wireOp",EDGE,"E271"),sQuery(id+"F8.wireOp",EDGE,"E272"),sQuery(id+"F8.wireOp",EDGE,"E273"),sQuery(id+"F8.wireOp",EDGE,"E274"),sQuery(id+"F8.wireOp",EDGE,"E275"),sQuery(id+"F8.wireOp",EDGE,"E276"),sQuery(id+"F8.wireOp",EDGE,"E277"),sQuery(id+"F8.wireOp",EDGE,"E278"),sQuery(id+"F8.wireOp",EDGE,"E279"),sQuery(id+"F8.wireOp",EDGE,"E280"),sQuery(id+"F8.wireOp",EDGE,"E281"),sQuery(id+"F8.wireOp",EDGE,"E282"),sQuery(id+"F8.wireOp",EDGE,"E283"),sQuery(id+"F8.wireOp",EDGE,"E284"),sQuery(id+"F8.wireOp",EDGE,"E285"),sQuery(id+"F8.wireOp",EDGE,"E286"),sQuery(id+"F8.wireOp",EDGE,"E287"),sQuery(id+"F8.wireOp",EDGE,"E288"),sQuery(id+"F8.wireOp",EDGE,"E289"),sQuery(id+"F8.wireOp",EDGE,"E290"),sQuery(id+"F8.wireOp",EDGE,"E291"),sQuery(id+"F8.wireOp",EDGE,"E292"),sQuery(id+"F8.wireOp",EDGE,"E293"),sQuery(id+"F8.wireOp",EDGE,"E294"),sQuery(id+"F8.wireOp",EDGE,"E295"),sQuery(id+"F8.wireOp",EDGE,"E296"),sQuery(id+"F8.wireOp",EDGE,"E297"),sQuery(id+"F8.wireOp",EDGE,"E298"),sQuery(id+"F8.wireOp",EDGE,"E299"),sQuery(id+"F8.wireOp",EDGE,"E300"),sQuery(id+"F8.wireOp",EDGE,"E301"),sQuery(id+"F8.wireOp",EDGE,"E302"),sQuery(id+"F8.wireOp",EDGE,"E303"),sQuery(id+"F8.wireOp",EDGE,"E304"),sQuery(id+"F8.wireOp",EDGE,"E305"),sQuery(id+"F8.wireOp",EDGE,"E306"),sQuery(id+"F8.wireOp",EDGE,"E307"),sQuery(id+"F8.wireOp",EDGE,"E308"),sQuery(id+"F8.wireOp",EDGE,"E309"),sQuery(id+"F8.wireOp",EDGE,"E310"),sQuery(id+"F8.wireOp",EDGE,"E311"),sQuery(id+"F8.wireOp",EDGE,"E312"),sQuery(id+"F8.wireOp",EDGE,"E313"),sQuery(id+"F8.wireOp",EDGE,"E314"),sQuery(id+"F8.wireOp",EDGE,"E315"),sQuery(id+"F8.wireOp",EDGE,"E316"),sQuery(id+"F8.wireOp",EDGE,"E317"),sQuery(id+"F8.wireOp",EDGE,"E318"),sQuery(id+"F8.wireOp",EDGE,"E319"),sQuery(id+"F8.wireOp",EDGE,"E320"),sQuery(id+"F8.wireOp",EDGE,"E321"),sQuery(id+"F8.wireOp",EDGE,"E322"),sQuery(id+"F8.wireOp",EDGE,"E323"),sQuery(id+"F8.wireOp",EDGE,"E324"),sQuery(id+"F8.wireOp",EDGE,"E325"),sQuery(id+"F8.wireOp",EDGE,"E326"),sQuery(id+"F8.wireOp",EDGE,"E327"),sQuery(id+"F8.wireOp",EDGE,"E328"),sQuery(id+"F8.wireOp",EDGE,"E329"),sQuery(id+"F8.wireOp",EDGE,"E330"),sQuery(id+"F8.wireOp",EDGE,"E331"),sQuery(id+"F8.wireOp",EDGE,"E332"),sQuery(id+"F8.wireOp",EDGE,"E333"),sQuery(id+"F8.wireOp",EDGE,"E334"),sQuery(id+"F8.wireOp",EDGE,"E335"),sQuery(id+"F8.wireOp",EDGE,"E336"),sQuery(id+"F8.wireOp",EDGE,"E337"),sQuery(id+"F8.wireOp",EDGE,"E338"),sQuery(id+"F8.wireOp",EDGE,"E339"),sQuery(id+"F8.wireOp",EDGE,"E340"),sQuery(id+"F8.wireOp",EDGE,"E341"),sQuery(id+"F8.wireOp",EDGE,"E342"),sQuery(id+"F8.wireOp",EDGE,"E343"),sQuery(id+"F8.wireOp",EDGE,"E344"),sQuery(id+"F8.wireOp",EDGE,"E345"),sQuery(id+"F8.wireOp",EDGE,"E346"),sQuery(id+"F8.wireOp",EDGE,"E347"),sQuery(id+"F8.wireOp",EDGE,"E348"),sQuery(id+"F8.wireOp",EDGE,"E349"),sQuery(id+"F8.wireOp",EDGE,"E350"),sQuery(id+"F8.wireOp",EDGE,"E351"),sQuery(id+"F8.wireOp",EDGE,"E352"),sQuery(id+"F8.wireOp",EDGE,"E353"),sQuery(id+"F8.wireOp",EDGE,"E354"),sQuery(id+"F8.wireOp",EDGE,"E355"),sQuery(id+"F8.wireOp",EDGE,"E356"),sQuery(id+"F8.wireOp",EDGE,"E357"),sQuery(id+"F8.wireOp",EDGE,"E358"),sQuery(id+"F8.wireOp",EDGE,"E359"),sQuery(id+"F8.wireOp",EDGE,"E360"),sQuery(id+"F8.wireOp",EDGE,"E361"),sQuery(id+"F8.wireOp",EDGE,"E362"),sQuery(id+"F8.wireOp",EDGE,"E363"),sQuery(id+"F8.wireOp",EDGE,"E364"),sQuery(id+"F8.wireOp",EDGE,"E365"),sQuery(id+"F8.wireOp",EDGE,"E366"),sQuery(id+"F8.wireOp",EDGE,"E367"),sQuery(id+"F8.wireOp",EDGE,"E368"),sQuery(id+"F8.wireOp",EDGE,"E369"),sQuery(id+"F8.wireOp",EDGE,"E370"),sQuery(id+"F8.wireOp",EDGE,"E371"),sQuery(id+"F8.wireOp",EDGE,"E372"),sQuery(id+"F8.wireOp",EDGE,"E373"),sQuery(id+"F8.wireOp",EDGE,"E374"),sQuery(id+"F8.wireOp",EDGE,"E375"),sQuery(id+"F8.wireOp",EDGE,"E376"),sQuery(id+"F8.wireOp",EDGE,"E377"),sQuery(id+"F8.wireOp",EDGE,"E378"),sQuery(id+"F8.wireOp",EDGE,"E379"),sQuery(id+"F8.wireOp",EDGE,"E380"),sQuery(id+"F8.wireOp",EDGE,"E381"),sQuery(id+"F8.wireOp",EDGE,"E382"),sQuery(id+"F8.wireOp",EDGE,"E383"),sQuery(id+"F8.wireOp",EDGE,"E384"),sQuery(id+"F8.wireOp",EDGE,"E385"),sQuery(id+"F8.wireOp",EDGE,"E386"),sQuery(id+"F8.wireOp",EDGE,"E387"),sQuery(id+"F8.wireOp",EDGE,"E388"),sQuery(id+"F8.wireOp",EDGE,"E389"),sQuery(id+"F8.wireOp",EDGE,"E390"),sQuery(id+"F8.wireOp",EDGE,"E391"),sQuery(id+"F8.wireOp",EDGE,"E392"),sQuery(id+"F8.wireOp",EDGE,"E393"),sQuery(id+"F8.wireOp",EDGE,"E394"),sQuery(id+"F8.wireOp",EDGE,"E395"),sQuery(id+"F8.wireOp",EDGE,"E396")])]});
            transform(context, id + "F15", {"entities" : qUnion([Q0]), "transformType" : TransformType.TRANSLATION_3D, "dx" : 0.8 * mm, "dy" : 0 * mm, "dz" : -0.4 * mm, "makeCopy" : false});
        }
        {
            var Q0;
            Q0=makeQuery(id+"F9.opExtrude","SWEPT_BODY",BODY,{"disambiguationData":[OSD([sQuery(id+"F8.wireOp",EDGE,"E4"),sQuery(id+"F8.wireOp",EDGE,"E5"),sQuery(id+"F8.wireOp",EDGE,"E6"),sQuery(id+"F8.wireOp",EDGE,"E7"),sQuery(id+"F8.wireOp",EDGE,"E8"),sQuery(id+"F8.wireOp",EDGE,"E9"),sQuery(id+"F8.wireOp",EDGE,"E10"),sQuery(id+"F8.wireOp",EDGE,"E11"),sQuery(id+"F8.wireOp",EDGE,"E12"),sQuery(id+"F8.wireOp",EDGE,"E13"),sQuery(id+"F8.wireOp",EDGE,"E14"),sQuery(id+"F8.wireOp",EDGE,"E15"),sQuery(id+"F8.wireOp",EDGE,"E16"),sQuery(id+"F8.wireOp",EDGE,"E17"),sQuery(id+"F8.wireOp",EDGE,"E18"),sQuery(id+"F8.wireOp",EDGE,"E19"),sQuery(id+"F8.wireOp",EDGE,"E20"),sQuery(id+"F8.wireOp",EDGE,"E21"),sQuery(id+"F8.wireOp",EDGE,"E22"),sQuery(id+"F8.wireOp",EDGE,"E23"),sQuery(id+"F8.wireOp",EDGE,"E24"),sQuery(id+"F8.wireOp",EDGE,"E25"),sQuery(id+"F8.wireOp",EDGE,"E26"),sQuery(id+"F8.wireOp",EDGE,"E27"),sQuery(id+"F8.wireOp",EDGE,"E28"),sQuery(id+"F8.wireOp",EDGE,"E29"),sQuery(id+"F8.wireOp",EDGE,"E30"),sQuery(id+"F8.wireOp",EDGE,"E31"),sQuery(id+"F8.wireOp",EDGE,"E32"),sQuery(id+"F8.wireOp",EDGE,"E33"),sQuery(id+"F8.wireOp",EDGE,"E34"),sQuery(id+"F8.wireOp",EDGE,"E35"),sQuery(id+"F8.wireOp",EDGE,"E36"),sQuery(id+"F8.wireOp",EDGE,"E37"),sQuery(id+"F8.wireOp",EDGE,"E38"),sQuery(id+"F8.wireOp",EDGE,"E39"),sQuery(id+"F8.wireOp",EDGE,"E40"),sQuery(id+"F8.wireOp",EDGE,"E41"),sQuery(id+"F8.wireOp",EDGE,"E42"),sQuery(id+"F8.wireOp",EDGE,"E43"),sQuery(id+"F8.wireOp",EDGE,"E44"),sQuery(id+"F8.wireOp",EDGE,"E45"),sQuery(id+"F8.wireOp",EDGE,"E46"),sQuery(id+"F8.wireOp",EDGE,"E47"),sQuery(id+"F8.wireOp",EDGE,"E48"),sQuery(id+"F8.wireOp",EDGE,"E49"),sQuery(id+"F8.wireOp",EDGE,"E50"),sQuery(id+"F8.wireOp",EDGE,"E51"),sQuery(id+"F8.wireOp",EDGE,"E52"),sQuery(id+"F8.wireOp",EDGE,"E53"),sQuery(id+"F8.wireOp",EDGE,"E54"),sQuery(id+"F8.wireOp",EDGE,"E55"),sQuery(id+"F8.wireOp",EDGE,"E56"),sQuery(id+"F8.wireOp",EDGE,"E57"),sQuery(id+"F8.wireOp",EDGE,"E58"),sQuery(id+"F8.wireOp",EDGE,"E59"),sQuery(id+"F8.wireOp",EDGE,"E60"),sQuery(id+"F8.wireOp",EDGE,"E61"),sQuery(id+"F8.wireOp",EDGE,"E62"),sQuery(id+"F8.wireOp",EDGE,"E63"),sQuery(id+"F8.wireOp",EDGE,"E64"),sQuery(id+"F8.wireOp",EDGE,"E65"),sQuery(id+"F8.wireOp",EDGE,"E66"),sQuery(id+"F8.wireOp",EDGE,"E67"),sQuery(id+"F8.wireOp",EDGE,"E68"),sQuery(id+"F8.wireOp",EDGE,"E69"),sQuery(id+"F8.wireOp",EDGE,"E70"),sQuery(id+"F8.wireOp",EDGE,"E71"),sQuery(id+"F8.wireOp",EDGE,"E72"),sQuery(id+"F8.wireOp",EDGE,"E73"),sQuery(id+"F8.wireOp",EDGE,"E74"),sQuery(id+"F8.wireOp",EDGE,"E75"),sQuery(id+"F8.wireOp",EDGE,"E76"),sQuery(id+"F8.wireOp",EDGE,"E77"),sQuery(id+"F8.wireOp",EDGE,"E78"),sQuery(id+"F8.wireOp",EDGE,"E79"),sQuery(id+"F8.wireOp",EDGE,"E80"),sQuery(id+"F8.wireOp",EDGE,"E81"),sQuery(id+"F8.wireOp",EDGE,"E82"),sQuery(id+"F8.wireOp",EDGE,"E83"),sQuery(id+"F8.wireOp",EDGE,"E84"),sQuery(id+"F8.wireOp",EDGE,"E85"),sQuery(id+"F8.wireOp",EDGE,"E86"),sQuery(id+"F8.wireOp",EDGE,"E87"),sQuery(id+"F8.wireOp",EDGE,"E88"),sQuery(id+"F8.wireOp",EDGE,"E89"),sQuery(id+"F8.wireOp",EDGE,"E90"),sQuery(id+"F8.wireOp",EDGE,"E91"),sQuery(id+"F8.wireOp",EDGE,"E92"),sQuery(id+"F8.wireOp",EDGE,"E93"),sQuery(id+"F8.wireOp",EDGE,"E94"),sQuery(id+"F8.wireOp",EDGE,"E95"),sQuery(id+"F8.wireOp",EDGE,"E96"),sQuery(id+"F8.wireOp",EDGE,"E97"),sQuery(id+"F8.wireOp",EDGE,"E98"),sQuery(id+"F8.wireOp",EDGE,"E99"),sQuery(id+"F8.wireOp",EDGE,"E100"),sQuery(id+"F8.wireOp",EDGE,"E100"),sQuery(id+"F8.wireOp",EDGE,"E100"),sQuery(id+"F8.wireOp",EDGE,"E101"),sQuery(id+"F8.wireOp",EDGE,"E102"),sQuery(id+"F8.wireOp",EDGE,"E102"),sQuery(id+"F8.wireOp",EDGE,"E102"),sQuery(id+"F8.wireOp",EDGE,"E102"),sQuery(id+"F8.wireOp",EDGE,"E103"),sQuery(id+"F8.wireOp",EDGE,"E104"),sQuery(id+"F8.wireOp",EDGE,"E105"),sQuery(id+"F8.wireOp",EDGE,"E106"),sQuery(id+"F8.wireOp",EDGE,"E107"),sQuery(id+"F8.wireOp",EDGE,"E108"),sQuery(id+"F8.wireOp",EDGE,"E109"),sQuery(id+"F8.wireOp",EDGE,"E110")])]});
            transform(context, id + "F16", {"entities" : qUnion([Q0]), "transformType" : TransformType.TRANSLATION_3D, "dx" : -0.5 * mm, "dy" : 0 * mm, "dz" : 0.4 * mm, "makeCopy" : false});
        }
        {
            var Q0;
            Q0=makeQuery(id+"F9.opExtrude","SWEPT_BODY",BODY,{"disambiguationData":[OSD([sQuery(id+"F8.wireOp",EDGE,"E4"),sQuery(id+"F8.wireOp",EDGE,"E5"),sQuery(id+"F8.wireOp",EDGE,"E6"),sQuery(id+"F8.wireOp",EDGE,"E7"),sQuery(id+"F8.wireOp",EDGE,"E8"),sQuery(id+"F8.wireOp",EDGE,"E9"),sQuery(id+"F8.wireOp",EDGE,"E10"),sQuery(id+"F8.wireOp",EDGE,"E11"),sQuery(id+"F8.wireOp",EDGE,"E12"),sQuery(id+"F8.wireOp",EDGE,"E13"),sQuery(id+"F8.wireOp",EDGE,"E14"),sQuery(id+"F8.wireOp",EDGE,"E15"),sQuery(id+"F8.wireOp",EDGE,"E16"),sQuery(id+"F8.wireOp",EDGE,"E17"),sQuery(id+"F8.wireOp",EDGE,"E18"),sQuery(id+"F8.wireOp",EDGE,"E19"),sQuery(id+"F8.wireOp",EDGE,"E20"),sQuery(id+"F8.wireOp",EDGE,"E21"),sQuery(id+"F8.wireOp",EDGE,"E22"),sQuery(id+"F8.wireOp",EDGE,"E23"),sQuery(id+"F8.wireOp",EDGE,"E24"),sQuery(id+"F8.wireOp",EDGE,"E25"),sQuery(id+"F8.wireOp",EDGE,"E26"),sQuery(id+"F8.wireOp",EDGE,"E27"),sQuery(id+"F8.wireOp",EDGE,"E28"),sQuery(id+"F8.wireOp",EDGE,"E29"),sQuery(id+"F8.wireOp",EDGE,"E30"),sQuery(id+"F8.wireOp",EDGE,"E31"),sQuery(id+"F8.wireOp",EDGE,"E32"),sQuery(id+"F8.wireOp",EDGE,"E33"),sQuery(id+"F8.wireOp",EDGE,"E34"),sQuery(id+"F8.wireOp",EDGE,"E35"),sQuery(id+"F8.wireOp",EDGE,"E36"),sQuery(id+"F8.wireOp",EDGE,"E37"),sQuery(id+"F8.wireOp",EDGE,"E38"),sQuery(id+"F8.wireOp",EDGE,"E39"),sQuery(id+"F8.wireOp",EDGE,"E40"),sQuery(id+"F8.wireOp",EDGE,"E41"),sQuery(id+"F8.wireOp",EDGE,"E42"),sQuery(id+"F8.wireOp",EDGE,"E43"),sQuery(id+"F8.wireOp",EDGE,"E44"),sQuery(id+"F8.wireOp",EDGE,"E45"),sQuery(id+"F8.wireOp",EDGE,"E46"),sQuery(id+"F8.wireOp",EDGE,"E47"),sQuery(id+"F8.wireOp",EDGE,"E48"),sQuery(id+"F8.wireOp",EDGE,"E49"),sQuery(id+"F8.wireOp",EDGE,"E50"),sQuery(id+"F8.wireOp",EDGE,"E51"),sQuery(id+"F8.wireOp",EDGE,"E52"),sQuery(id+"F8.wireOp",EDGE,"E53"),sQuery(id+"F8.wireOp",EDGE,"E54"),sQuery(id+"F8.wireOp",EDGE,"E55"),sQuery(id+"F8.wireOp",EDGE,"E56"),sQuery(id+"F8.wireOp",EDGE,"E57"),sQuery(id+"F8.wireOp",EDGE,"E58"),sQuery(id+"F8.wireOp",EDGE,"E59"),sQuery(id+"F8.wireOp",EDGE,"E60"),sQuery(id+"F8.wireOp",EDGE,"E61"),sQuery(id+"F8.wireOp",EDGE,"E62"),sQuery(id+"F8.wireOp",EDGE,"E63"),sQuery(id+"F8.wireOp",EDGE,"E64"),sQuery(id+"F8.wireOp",EDGE,"E65"),sQuery(id+"F8.wireOp",EDGE,"E66"),sQuery(id+"F8.wireOp",EDGE,"E67"),sQuery(id+"F8.wireOp",EDGE,"E68"),sQuery(id+"F8.wireOp",EDGE,"E69"),sQuery(id+"F8.wireOp",EDGE,"E70"),sQuery(id+"F8.wireOp",EDGE,"E71"),sQuery(id+"F8.wireOp",EDGE,"E72"),sQuery(id+"F8.wireOp",EDGE,"E73"),sQuery(id+"F8.wireOp",EDGE,"E74"),sQuery(id+"F8.wireOp",EDGE,"E75"),sQuery(id+"F8.wireOp",EDGE,"E76"),sQuery(id+"F8.wireOp",EDGE,"E77"),sQuery(id+"F8.wireOp",EDGE,"E78"),sQuery(id+"F8.wireOp",EDGE,"E79"),sQuery(id+"F8.wireOp",EDGE,"E80"),sQuery(id+"F8.wireOp",EDGE,"E81"),sQuery(id+"F8.wireOp",EDGE,"E82"),sQuery(id+"F8.wireOp",EDGE,"E83"),sQuery(id+"F8.wireOp",EDGE,"E84"),sQuery(id+"F8.wireOp",EDGE,"E85"),sQuery(id+"F8.wireOp",EDGE,"E86"),sQuery(id+"F8.wireOp",EDGE,"E87"),sQuery(id+"F8.wireOp",EDGE,"E88"),sQuery(id+"F8.wireOp",EDGE,"E89"),sQuery(id+"F8.wireOp",EDGE,"E90"),sQuery(id+"F8.wireOp",EDGE,"E91"),sQuery(id+"F8.wireOp",EDGE,"E92"),sQuery(id+"F8.wireOp",EDGE,"E93"),sQuery(id+"F8.wireOp",EDGE,"E94"),sQuery(id+"F8.wireOp",EDGE,"E95"),sQuery(id+"F8.wireOp",EDGE,"E96"),sQuery(id+"F8.wireOp",EDGE,"E97"),sQuery(id+"F8.wireOp",EDGE,"E98"),sQuery(id+"F8.wireOp",EDGE,"E99"),sQuery(id+"F8.wireOp",EDGE,"E100"),sQuery(id+"F8.wireOp",EDGE,"E100"),sQuery(id+"F8.wireOp",EDGE,"E100"),sQuery(id+"F8.wireOp",EDGE,"E101"),sQuery(id+"F8.wireOp",EDGE,"E102"),sQuery(id+"F8.wireOp",EDGE,"E102"),sQuery(id+"F8.wireOp",EDGE,"E102"),sQuery(id+"F8.wireOp",EDGE,"E102"),sQuery(id+"F8.wireOp",EDGE,"E103"),sQuery(id+"F8.wireOp",EDGE,"E104"),sQuery(id+"F8.wireOp",EDGE,"E105"),sQuery(id+"F8.wireOp",EDGE,"E106"),sQuery(id+"F8.wireOp",EDGE,"E107"),sQuery(id+"F8.wireOp",EDGE,"E108"),sQuery(id+"F8.wireOp",EDGE,"E109"),sQuery(id+"F8.wireOp",EDGE,"E110")])]});
            var Q1;
            Q1=makeQuery(id+"F9.opExtrude","CAP_EDGE",EDGE,{"disambiguationData":[OSD([sQuery(id+"F8.wireOp",EDGE,"E71")])],"isStart":true});
            transform(context, id + "F17", {"entities" : qUnion([Q0]), "transformType" : TransformType.ROTATION, "transformAxis" : qUnion([Q1]), "angle" : 15 * degree, "makeCopy" : false});
        }
        {
            var Q0;
            Q0=makeQuery(id+"F9.opExtrude","SWEPT_BODY",BODY,{"disambiguationData":[OSD([sQuery(id+"F8.wireOp",EDGE,"E237"),sQuery(id+"F8.wireOp",EDGE,"E238"),sQuery(id+"F8.wireOp",EDGE,"E239"),sQuery(id+"F8.wireOp",EDGE,"E240"),sQuery(id+"F8.wireOp",EDGE,"E241"),sQuery(id+"F8.wireOp",EDGE,"E242"),sQuery(id+"F8.wireOp",EDGE,"E243"),sQuery(id+"F8.wireOp",EDGE,"E244"),sQuery(id+"F8.wireOp",EDGE,"E245"),sQuery(id+"F8.wireOp",EDGE,"E246"),sQuery(id+"F8.wireOp",EDGE,"E247"),sQuery(id+"F8.wireOp",EDGE,"E248"),sQuery(id+"F8.wireOp",EDGE,"E249"),sQuery(id+"F8.wireOp",EDGE,"E250"),sQuery(id+"F8.wireOp",EDGE,"E251"),sQuery(id+"F8.wireOp",EDGE,"E252"),sQuery(id+"F8.wireOp",EDGE,"E253"),sQuery(id+"F8.wireOp",EDGE,"E254"),sQuery(id+"F8.wireOp",EDGE,"E255"),sQuery(id+"F8.wireOp",EDGE,"E256"),sQuery(id+"F8.wireOp",EDGE,"E257"),sQuery(id+"F8.wireOp",EDGE,"E258"),sQuery(id+"F8.wireOp",EDGE,"E259"),sQuery(id+"F8.wireOp",EDGE,"E260"),sQuery(id+"F8.wireOp",EDGE,"E261"),sQuery(id+"F8.wireOp",EDGE,"E262"),sQuery(id+"F8.wireOp",EDGE,"E263"),sQuery(id+"F8.wireOp",EDGE,"E264"),sQuery(id+"F8.wireOp",EDGE,"E265"),sQuery(id+"F8.wireOp",EDGE,"E266"),sQuery(id+"F8.wireOp",EDGE,"E267"),sQuery(id+"F8.wireOp",EDGE,"E268"),sQuery(id+"F8.wireOp",EDGE,"E269"),sQuery(id+"F8.wireOp",EDGE,"E270"),sQuery(id+"F8.wireOp",EDGE,"E271"),sQuery(id+"F8.wireOp",EDGE,"E272"),sQuery(id+"F8.wireOp",EDGE,"E273"),sQuery(id+"F8.wireOp",EDGE,"E274"),sQuery(id+"F8.wireOp",EDGE,"E275"),sQuery(id+"F8.wireOp",EDGE,"E276"),sQuery(id+"F8.wireOp",EDGE,"E277"),sQuery(id+"F8.wireOp",EDGE,"E278"),sQuery(id+"F8.wireOp",EDGE,"E279"),sQuery(id+"F8.wireOp",EDGE,"E280"),sQuery(id+"F8.wireOp",EDGE,"E281"),sQuery(id+"F8.wireOp",EDGE,"E282"),sQuery(id+"F8.wireOp",EDGE,"E283"),sQuery(id+"F8.wireOp",EDGE,"E284"),sQuery(id+"F8.wireOp",EDGE,"E285"),sQuery(id+"F8.wireOp",EDGE,"E286"),sQuery(id+"F8.wireOp",EDGE,"E287"),sQuery(id+"F8.wireOp",EDGE,"E288"),sQuery(id+"F8.wireOp",EDGE,"E289"),sQuery(id+"F8.wireOp",EDGE,"E290"),sQuery(id+"F8.wireOp",EDGE,"E291"),sQuery(id+"F8.wireOp",EDGE,"E292"),sQuery(id+"F8.wireOp",EDGE,"E293"),sQuery(id+"F8.wireOp",EDGE,"E294"),sQuery(id+"F8.wireOp",EDGE,"E295"),sQuery(id+"F8.wireOp",EDGE,"E296"),sQuery(id+"F8.wireOp",EDGE,"E297"),sQuery(id+"F8.wireOp",EDGE,"E298"),sQuery(id+"F8.wireOp",EDGE,"E299"),sQuery(id+"F8.wireOp",EDGE,"E300"),sQuery(id+"F8.wireOp",EDGE,"E301"),sQuery(id+"F8.wireOp",EDGE,"E302"),sQuery(id+"F8.wireOp",EDGE,"E303"),sQuery(id+"F8.wireOp",EDGE,"E304"),sQuery(id+"F8.wireOp",EDGE,"E305"),sQuery(id+"F8.wireOp",EDGE,"E306"),sQuery(id+"F8.wireOp",EDGE,"E307"),sQuery(id+"F8.wireOp",EDGE,"E308"),sQuery(id+"F8.wireOp",EDGE,"E309"),sQuery(id+"F8.wireOp",EDGE,"E310"),sQuery(id+"F8.wireOp",EDGE,"E311"),sQuery(id+"F8.wireOp",EDGE,"E312"),sQuery(id+"F8.wireOp",EDGE,"E313"),sQuery(id+"F8.wireOp",EDGE,"E314"),sQuery(id+"F8.wireOp",EDGE,"E315"),sQuery(id+"F8.wireOp",EDGE,"E316"),sQuery(id+"F8.wireOp",EDGE,"E317"),sQuery(id+"F8.wireOp",EDGE,"E318"),sQuery(id+"F8.wireOp",EDGE,"E319"),sQuery(id+"F8.wireOp",EDGE,"E320"),sQuery(id+"F8.wireOp",EDGE,"E321"),sQuery(id+"F8.wireOp",EDGE,"E322"),sQuery(id+"F8.wireOp",EDGE,"E323"),sQuery(id+"F8.wireOp",EDGE,"E324"),sQuery(id+"F8.wireOp",EDGE,"E325"),sQuery(id+"F8.wireOp",EDGE,"E326"),sQuery(id+"F8.wireOp",EDGE,"E327"),sQuery(id+"F8.wireOp",EDGE,"E328"),sQuery(id+"F8.wireOp",EDGE,"E329"),sQuery(id+"F8.wireOp",EDGE,"E330"),sQuery(id+"F8.wireOp",EDGE,"E331"),sQuery(id+"F8.wireOp",EDGE,"E332"),sQuery(id+"F8.wireOp",EDGE,"E333"),sQuery(id+"F8.wireOp",EDGE,"E334"),sQuery(id+"F8.wireOp",EDGE,"E335"),sQuery(id+"F8.wireOp",EDGE,"E336"),sQuery(id+"F8.wireOp",EDGE,"E337"),sQuery(id+"F8.wireOp",EDGE,"E338"),sQuery(id+"F8.wireOp",EDGE,"E339"),sQuery(id+"F8.wireOp",EDGE,"E340"),sQuery(id+"F8.wireOp",EDGE,"E341"),sQuery(id+"F8.wireOp",EDGE,"E342"),sQuery(id+"F8.wireOp",EDGE,"E343"),sQuery(id+"F8.wireOp",EDGE,"E344"),sQuery(id+"F8.wireOp",EDGE,"E345"),sQuery(id+"F8.wireOp",EDGE,"E346"),sQuery(id+"F8.wireOp",EDGE,"E347"),sQuery(id+"F8.wireOp",EDGE,"E348"),sQuery(id+"F8.wireOp",EDGE,"E349"),sQuery(id+"F8.wireOp",EDGE,"E350"),sQuery(id+"F8.wireOp",EDGE,"E351"),sQuery(id+"F8.wireOp",EDGE,"E352"),sQuery(id+"F8.wireOp",EDGE,"E353"),sQuery(id+"F8.wireOp",EDGE,"E354"),sQuery(id+"F8.wireOp",EDGE,"E355"),sQuery(id+"F8.wireOp",EDGE,"E356"),sQuery(id+"F8.wireOp",EDGE,"E357"),sQuery(id+"F8.wireOp",EDGE,"E358"),sQuery(id+"F8.wireOp",EDGE,"E359"),sQuery(id+"F8.wireOp",EDGE,"E360"),sQuery(id+"F8.wireOp",EDGE,"E361"),sQuery(id+"F8.wireOp",EDGE,"E362"),sQuery(id+"F8.wireOp",EDGE,"E363"),sQuery(id+"F8.wireOp",EDGE,"E364"),sQuery(id+"F8.wireOp",EDGE,"E365"),sQuery(id+"F8.wireOp",EDGE,"E366"),sQuery(id+"F8.wireOp",EDGE,"E367"),sQuery(id+"F8.wireOp",EDGE,"E368"),sQuery(id+"F8.wireOp",EDGE,"E369"),sQuery(id+"F8.wireOp",EDGE,"E370"),sQuery(id+"F8.wireOp",EDGE,"E371"),sQuery(id+"F8.wireOp",EDGE,"E372"),sQuery(id+"F8.wireOp",EDGE,"E373"),sQuery(id+"F8.wireOp",EDGE,"E374"),sQuery(id+"F8.wireOp",EDGE,"E375"),sQuery(id+"F8.wireOp",EDGE,"E376"),sQuery(id+"F8.wireOp",EDGE,"E377"),sQuery(id+"F8.wireOp",EDGE,"E378"),sQuery(id+"F8.wireOp",EDGE,"E379"),sQuery(id+"F8.wireOp",EDGE,"E380"),sQuery(id+"F8.wireOp",EDGE,"E381"),sQuery(id+"F8.wireOp",EDGE,"E382"),sQuery(id+"F8.wireOp",EDGE,"E383"),sQuery(id+"F8.wireOp",EDGE,"E384"),sQuery(id+"F8.wireOp",EDGE,"E385"),sQuery(id+"F8.wireOp",EDGE,"E386"),sQuery(id+"F8.wireOp",EDGE,"E387"),sQuery(id+"F8.wireOp",EDGE,"E388"),sQuery(id+"F8.wireOp",EDGE,"E389"),sQuery(id+"F8.wireOp",EDGE,"E390"),sQuery(id+"F8.wireOp",EDGE,"E391"),sQuery(id+"F8.wireOp",EDGE,"E392"),sQuery(id+"F8.wireOp",EDGE,"E393"),sQuery(id+"F8.wireOp",EDGE,"E394"),sQuery(id+"F8.wireOp",EDGE,"E395"),sQuery(id+"F8.wireOp",EDGE,"E396")])]});
            var Q1;
            Q1=makeQuery(id+"F9.opExtrude","SWEPT_BODY",BODY,{"disambiguationData":[OSD([sQuery(id+"F8.wireOp",EDGE,"E143"),sQuery(id+"F8.wireOp",EDGE,"E144"),sQuery(id+"F8.wireOp",EDGE,"E145"),sQuery(id+"F8.wireOp",EDGE,"E146"),sQuery(id+"F8.wireOp",EDGE,"E147"),sQuery(id+"F8.wireOp",EDGE,"E148"),sQuery(id+"F8.wireOp",EDGE,"E149"),sQuery(id+"F8.wireOp",EDGE,"E150"),sQuery(id+"F8.wireOp",EDGE,"E151"),sQuery(id+"F8.wireOp",EDGE,"E152"),sQuery(id+"F8.wireOp",EDGE,"E153"),sQuery(id+"F8.wireOp",EDGE,"E154"),sQuery(id+"F8.wireOp",EDGE,"E155"),sQuery(id+"F8.wireOp",EDGE,"E156"),sQuery(id+"F8.wireOp",EDGE,"E156"),sQuery(id+"F8.wireOp",EDGE,"E156"),sQuery(id+"F8.wireOp",EDGE,"E157"),sQuery(id+"F8.wireOp",EDGE,"E158"),sQuery(id+"F8.wireOp",EDGE,"E159"),sQuery(id+"F8.wireOp",EDGE,"E160"),sQuery(id+"F8.wireOp",EDGE,"E161"),sQuery(id+"F8.wireOp",EDGE,"E162"),sQuery(id+"F8.wireOp",EDGE,"E163"),sQuery(id+"F8.wireOp",EDGE,"E164"),sQuery(id+"F8.wireOp",EDGE,"E165"),sQuery(id+"F8.wireOp",EDGE,"E166"),sQuery(id+"F8.wireOp",EDGE,"E167"),sQuery(id+"F8.wireOp",EDGE,"E168"),sQuery(id+"F8.wireOp",EDGE,"E169"),sQuery(id+"F8.wireOp",EDGE,"E170"),sQuery(id+"F8.wireOp",EDGE,"E171"),sQuery(id+"F8.wireOp",EDGE,"E172"),sQuery(id+"F8.wireOp",EDGE,"E173"),sQuery(id+"F8.wireOp",EDGE,"E174"),sQuery(id+"F8.wireOp",EDGE,"E175"),sQuery(id+"F8.wireOp",EDGE,"E176"),sQuery(id+"F8.wireOp",EDGE,"E177"),sQuery(id+"F8.wireOp",EDGE,"E178"),sQuery(id+"F8.wireOp",EDGE,"E179"),sQuery(id+"F8.wireOp",EDGE,"E180"),sQuery(id+"F8.wireOp",EDGE,"E181"),sQuery(id+"F8.wireOp",EDGE,"E182"),sQuery(id+"F8.wireOp",EDGE,"E183"),sQuery(id+"F8.wireOp",EDGE,"E184"),sQuery(id+"F8.wireOp",EDGE,"E185"),sQuery(id+"F8.wireOp",EDGE,"E186"),sQuery(id+"F8.wireOp",EDGE,"E187"),sQuery(id+"F8.wireOp",EDGE,"E188"),sQuery(id+"F8.wireOp",EDGE,"E189"),sQuery(id+"F8.wireOp",EDGE,"E190"),sQuery(id+"F8.wireOp",EDGE,"E191"),sQuery(id+"F8.wireOp",EDGE,"E192"),sQuery(id+"F8.wireOp",EDGE,"E193"),sQuery(id+"F8.wireOp",EDGE,"E194"),sQuery(id+"F8.wireOp",EDGE,"E195"),sQuery(id+"F8.wireOp",EDGE,"E196"),sQuery(id+"F8.wireOp",EDGE,"E197"),sQuery(id+"F8.wireOp",EDGE,"E198"),sQuery(id+"F8.wireOp",EDGE,"E199"),sQuery(id+"F8.wireOp",EDGE,"E200"),sQuery(id+"F8.wireOp",EDGE,"E201"),sQuery(id+"F8.wireOp",EDGE,"E202"),sQuery(id+"F8.wireOp",EDGE,"E203"),sQuery(id+"F8.wireOp",EDGE,"E204"),sQuery(id+"F8.wireOp",EDGE,"E205"),sQuery(id+"F8.wireOp",EDGE,"E206"),sQuery(id+"F8.wireOp",EDGE,"E207"),sQuery(id+"F8.wireOp",EDGE,"E208"),sQuery(id+"F8.wireOp",EDGE,"E209"),sQuery(id+"F8.wireOp",EDGE,"E210"),sQuery(id+"F8.wireOp",EDGE,"E211"),sQuery(id+"F8.wireOp",EDGE,"E212"),sQuery(id+"F8.wireOp",EDGE,"E213"),sQuery(id+"F8.wireOp",EDGE,"E214"),sQuery(id+"F8.wireOp",EDGE,"E215"),sQuery(id+"F8.wireOp",EDGE,"E216"),sQuery(id+"F8.wireOp",EDGE,"E217"),sQuery(id+"F8.wireOp",EDGE,"E218"),sQuery(id+"F8.wireOp",EDGE,"E219"),sQuery(id+"F8.wireOp",EDGE,"E220"),sQuery(id+"F8.wireOp",EDGE,"E221"),sQuery(id+"F8.wireOp",EDGE,"E222"),sQuery(id+"F8.wireOp",EDGE,"E223"),sQuery(id+"F8.wireOp",EDGE,"E224"),sQuery(id+"F8.wireOp",EDGE,"E225"),sQuery(id+"F8.wireOp",EDGE,"E226"),sQuery(id+"F8.wireOp",EDGE,"E227"),sQuery(id+"F8.wireOp",EDGE,"E228"),sQuery(id+"F8.wireOp",EDGE,"E229"),sQuery(id+"F8.wireOp",EDGE,"E230"),sQuery(id+"F8.wireOp",EDGE,"E231"),sQuery(id+"F8.wireOp",EDGE,"E232"),sQuery(id+"F8.wireOp",EDGE,"E233"),sQuery(id+"F8.wireOp",EDGE,"E234"),sQuery(id+"F8.wireOp",EDGE,"E235"),sQuery(id+"F8.wireOp",EDGE,"E236")])]});
            var Q2;
            Q2=makeQuery(id+"F9.opExtrude","SWEPT_BODY",BODY,{"disambiguationData":[OSD([sQuery(id+"F8.wireOp",EDGE,"E111"),sQuery(id+"F8.wireOp",EDGE,"E112"),sQuery(id+"F8.wireOp",EDGE,"E113"),sQuery(id+"F8.wireOp",EDGE,"E114"),sQuery(id+"F8.wireOp",EDGE,"E115"),sQuery(id+"F8.wireOp",EDGE,"E116"),sQuery(id+"F8.wireOp",EDGE,"E117"),sQuery(id+"F8.wireOp",EDGE,"E118"),sQuery(id+"F8.wireOp",EDGE,"E119"),sQuery(id+"F8.wireOp",EDGE,"E120"),sQuery(id+"F8.wireOp",EDGE,"E121"),sQuery(id+"F8.wireOp",EDGE,"E122"),sQuery(id+"F8.wireOp",EDGE,"E123"),sQuery(id+"F8.wireOp",EDGE,"E124"),sQuery(id+"F8.wireOp",EDGE,"E125"),sQuery(id+"F8.wireOp",EDGE,"E126"),sQuery(id+"F8.wireOp",EDGE,"E127"),sQuery(id+"F8.wireOp",EDGE,"E128"),sQuery(id+"F8.wireOp",EDGE,"E129"),sQuery(id+"F8.wireOp",EDGE,"E130"),sQuery(id+"F8.wireOp",EDGE,"E131"),sQuery(id+"F8.wireOp",EDGE,"E132"),sQuery(id+"F8.wireOp",EDGE,"E133"),sQuery(id+"F8.wireOp",EDGE,"E134"),sQuery(id+"F8.wireOp",EDGE,"E135"),sQuery(id+"F8.wireOp",EDGE,"E136"),sQuery(id+"F8.wireOp",EDGE,"E137"),sQuery(id+"F8.wireOp",EDGE,"E138"),sQuery(id+"F8.wireOp",EDGE,"E139"),sQuery(id+"F8.wireOp",EDGE,"E140"),sQuery(id+"F8.wireOp",EDGE,"E141"),sQuery(id+"F8.wireOp",EDGE,"E142")])]});
            var Q3;
            Q3=makeQuery(id+"F9.opExtrude","SWEPT_BODY",BODY,{"disambiguationData":[OSD([sQuery(id+"F8.wireOp",EDGE,"E4"),sQuery(id+"F8.wireOp",EDGE,"E5"),sQuery(id+"F8.wireOp",EDGE,"E6"),sQuery(id+"F8.wireOp",EDGE,"E7"),sQuery(id+"F8.wireOp",EDGE,"E8"),sQuery(id+"F8.wireOp",EDGE,"E9"),sQuery(id+"F8.wireOp",EDGE,"E10"),sQuery(id+"F8.wireOp",EDGE,"E11"),sQuery(id+"F8.wireOp",EDGE,"E12"),sQuery(id+"F8.wireOp",EDGE,"E13"),sQuery(id+"F8.wireOp",EDGE,"E14"),sQuery(id+"F8.wireOp",EDGE,"E15"),sQuery(id+"F8.wireOp",EDGE,"E16"),sQuery(id+"F8.wireOp",EDGE,"E17"),sQuery(id+"F8.wireOp",EDGE,"E18"),sQuery(id+"F8.wireOp",EDGE,"E19"),sQuery(id+"F8.wireOp",EDGE,"E20"),sQuery(id+"F8.wireOp",EDGE,"E21"),sQuery(id+"F8.wireOp",EDGE,"E22"),sQuery(id+"F8.wireOp",EDGE,"E23"),sQuery(id+"F8.wireOp",EDGE,"E24"),sQuery(id+"F8.wireOp",EDGE,"E25"),sQuery(id+"F8.wireOp",EDGE,"E26"),sQuery(id+"F8.wireOp",EDGE,"E27"),sQuery(id+"F8.wireOp",EDGE,"E28"),sQuery(id+"F8.wireOp",EDGE,"E29"),sQuery(id+"F8.wireOp",EDGE,"E30"),sQuery(id+"F8.wireOp",EDGE,"E31"),sQuery(id+"F8.wireOp",EDGE,"E32"),sQuery(id+"F8.wireOp",EDGE,"E33"),sQuery(id+"F8.wireOp",EDGE,"E34"),sQuery(id+"F8.wireOp",EDGE,"E35"),sQuery(id+"F8.wireOp",EDGE,"E36"),sQuery(id+"F8.wireOp",EDGE,"E37"),sQuery(id+"F8.wireOp",EDGE,"E38"),sQuery(id+"F8.wireOp",EDGE,"E39"),sQuery(id+"F8.wireOp",EDGE,"E40"),sQuery(id+"F8.wireOp",EDGE,"E41"),sQuery(id+"F8.wireOp",EDGE,"E42"),sQuery(id+"F8.wireOp",EDGE,"E43"),sQuery(id+"F8.wireOp",EDGE,"E44"),sQuery(id+"F8.wireOp",EDGE,"E45"),sQuery(id+"F8.wireOp",EDGE,"E46"),sQuery(id+"F8.wireOp",EDGE,"E47"),sQuery(id+"F8.wireOp",EDGE,"E48"),sQuery(id+"F8.wireOp",EDGE,"E49"),sQuery(id+"F8.wireOp",EDGE,"E50"),sQuery(id+"F8.wireOp",EDGE,"E51"),sQuery(id+"F8.wireOp",EDGE,"E52"),sQuery(id+"F8.wireOp",EDGE,"E53"),sQuery(id+"F8.wireOp",EDGE,"E54"),sQuery(id+"F8.wireOp",EDGE,"E55"),sQuery(id+"F8.wireOp",EDGE,"E56"),sQuery(id+"F8.wireOp",EDGE,"E57"),sQuery(id+"F8.wireOp",EDGE,"E58"),sQuery(id+"F8.wireOp",EDGE,"E59"),sQuery(id+"F8.wireOp",EDGE,"E60"),sQuery(id+"F8.wireOp",EDGE,"E61"),sQuery(id+"F8.wireOp",EDGE,"E62"),sQuery(id+"F8.wireOp",EDGE,"E63"),sQuery(id+"F8.wireOp",EDGE,"E64"),sQuery(id+"F8.wireOp",EDGE,"E65"),sQuery(id+"F8.wireOp",EDGE,"E66"),sQuery(id+"F8.wireOp",EDGE,"E67"),sQuery(id+"F8.wireOp",EDGE,"E68"),sQuery(id+"F8.wireOp",EDGE,"E69"),sQuery(id+"F8.wireOp",EDGE,"E70"),sQuery(id+"F8.wireOp",EDGE,"E71"),sQuery(id+"F8.wireOp",EDGE,"E72"),sQuery(id+"F8.wireOp",EDGE,"E73"),sQuery(id+"F8.wireOp",EDGE,"E74"),sQuery(id+"F8.wireOp",EDGE,"E75"),sQuery(id+"F8.wireOp",EDGE,"E76"),sQuery(id+"F8.wireOp",EDGE,"E77"),sQuery(id+"F8.wireOp",EDGE,"E78"),sQuery(id+"F8.wireOp",EDGE,"E79"),sQuery(id+"F8.wireOp",EDGE,"E80"),sQuery(id+"F8.wireOp",EDGE,"E81"),sQuery(id+"F8.wireOp",EDGE,"E82"),sQuery(id+"F8.wireOp",EDGE,"E83"),sQuery(id+"F8.wireOp",EDGE,"E84"),sQuery(id+"F8.wireOp",EDGE,"E85"),sQuery(id+"F8.wireOp",EDGE,"E86"),sQuery(id+"F8.wireOp",EDGE,"E87"),sQuery(id+"F8.wireOp",EDGE,"E88"),sQuery(id+"F8.wireOp",EDGE,"E89"),sQuery(id+"F8.wireOp",EDGE,"E90"),sQuery(id+"F8.wireOp",EDGE,"E91"),sQuery(id+"F8.wireOp",EDGE,"E92"),sQuery(id+"F8.wireOp",EDGE,"E93"),sQuery(id+"F8.wireOp",EDGE,"E94"),sQuery(id+"F8.wireOp",EDGE,"E95"),sQuery(id+"F8.wireOp",EDGE,"E96"),sQuery(id+"F8.wireOp",EDGE,"E97"),sQuery(id+"F8.wireOp",EDGE,"E98"),sQuery(id+"F8.wireOp",EDGE,"E99"),sQuery(id+"F8.wireOp",EDGE,"E100"),sQuery(id+"F8.wireOp",EDGE,"E100"),sQuery(id+"F8.wireOp",EDGE,"E100"),sQuery(id+"F8.wireOp",EDGE,"E101"),sQuery(id+"F8.wireOp",EDGE,"E102"),sQuery(id+"F8.wireOp",EDGE,"E102"),sQuery(id+"F8.wireOp",EDGE,"E102"),sQuery(id+"F8.wireOp",EDGE,"E102"),sQuery(id+"F8.wireOp",EDGE,"E103"),sQuery(id+"F8.wireOp",EDGE,"E104"),sQuery(id+"F8.wireOp",EDGE,"E105"),sQuery(id+"F8.wireOp",EDGE,"E106"),sQuery(id+"F8.wireOp",EDGE,"E107"),sQuery(id+"F8.wireOp",EDGE,"E108"),sQuery(id+"F8.wireOp",EDGE,"E109"),sQuery(id+"F8.wireOp",EDGE,"E110")])]});
            var Q4;
            Q4=makeQuery(id+"F3.opLoft","SWEPT_BODY",BODY,{"disambiguationData":[OSD([makeQuery(id+"F0.imprint","IMPRINT",FACE,{"disambiguationData":[TD([[makeQuery(id+"F0.imprint","IMPRINT",EDGE,{"derivedFrom":sQuery(id+"F0.wireOp",EDGE,"E0")}),1.0]])]}),makeQuery(id+"F2.imprint","IMPRINT",FACE,{"disambiguationData":[TD([[makeQuery(id+"F2.imprint","IMPRINT",EDGE,{"derivedFrom":sQuery(id+"F2.wireOp",EDGE,"E1")}),1.0]])]})])]});
            booleanBodies(context, id + "F18", {"operationType" : BooleanOperationType.SUBTRACTION, "tools" : qUnion([Q0, Q1, Q2, Q3]), "targets" : qUnion([Q4])});
        }
        {
            var Q0;
            Q0=qCreatedBy(makeId("Top.planeOp"),FACE);
            var sketch = newSketch(context, id + "F19", { "sketchPlane" : qUnion([Q0])});
            skCircle(sketch, "E397", {"center": v(-60.04, 0) * mm, "radius": 12.5 * mm});
            skSolve(sketch);
        }
        {
            var Q0;
            Q0 = qSketchRegion(id + "F19", true);
            extrude(context, id + "F20", {"entities" : qUnion([Q0]), "depth" : 3 * mm, "offsetDistance" : 25 * mm});
        }
        {
            var Q0;
            Q0=qCreatedBy(makeId("Top.planeOp"),FACE);
            var sketch = newSketch(context, id + "F21", { "sketchPlane" : qUnion([Q0])});
            skLineSegment(sketch, "E398", {"start": v(-53.33, 1.55) * mm, "end": v(-53.31, 1.64) * mm});
            skLineSegment(sketch, "E399", {"start": v(-53.31, 1.64) * mm, "end": v(-53.29, 1.74) * mm});
            skLineSegment(sketch, "E400", {"start": v(-53.29, 1.74) * mm, "end": v(-53.25, 1.84) * mm});
            skLineSegment(sketch, "E401", {"start": v(-53.25, 1.84) * mm, "end": v(-53.2, 1.94) * mm});
            skLineSegment(sketch, "E402", {"start": v(-53.2, 1.94) * mm, "end": v(-53.13, 2.03) * mm});
            skLineSegment(sketch, "E403", {"start": v(-53.13, 2.03) * mm, "end": v(-53.03, 2.1) * mm});
            skLineSegment(sketch, "E404", {"start": v(-53.03, 2.1) * mm, "end": v(-52.9, 2.15) * mm});
            skLineSegment(sketch, "E405", {"start": v(-52.9, 2.15) * mm, "end": v(-52.72, 2.16) * mm});
            skLineSegment(sketch, "E406", {"start": v(-52.72, 2.16) * mm, "end": v(-52.52, 2.16) * mm});
            skLineSegment(sketch, "E407", {"start": v(-52.52, 2.16) * mm, "end": v(-52.16, 2.16) * mm});
            skLineSegment(sketch, "E408", {"start": v(-52.16, 2.16) * mm, "end": v(-51.69, 2.16) * mm});
            skLineSegment(sketch, "E409", {"start": v(-51.69, 2.16) * mm, "end": v(-51.17, 2.16) * mm});
            skLineSegment(sketch, "E410", {"start": v(-51.17, 2.16) * mm, "end": v(-50.67, 2.16) * mm});
            skLineSegment(sketch, "E411", {"start": v(-50.67, 2.16) * mm, "end": v(-50.23, 2.16) * mm});
            skLineSegment(sketch, "E412", {"start": v(-50.23, 2.16) * mm, "end": v(-49.93, 2.16) * mm});
            skLineSegment(sketch, "E413", {"start": v(-49.93, 2.16) * mm, "end": v(-49.81, 2.16) * mm});
            skLineSegment(sketch, "E414", {"start": v(-49.81, 2.16) * mm, "end": v(-49.78, 2.3) * mm});
            skLineSegment(sketch, "E415", {"start": v(-49.78, 2.3) * mm, "end": v(-49.75, 2.44) * mm});
            skLineSegment(sketch, "E416", {"start": v(-49.75, 2.44) * mm, "end": v(-49.71, 2.58) * mm});
            skLineSegment(sketch, "E417", {"start": v(-49.71, 2.58) * mm, "end": v(-49.68, 2.72) * mm});
            skLineSegment(sketch, "E418", {"start": v(-49.68, 2.72) * mm, "end": v(-49.65, 2.85) * mm});
            skLineSegment(sketch, "E419", {"start": v(-49.65, 2.85) * mm, "end": v(-49.62, 3) * mm});
            skLineSegment(sketch, "E420", {"start": v(-49.62, 3) * mm, "end": v(-49.58, 3.13) * mm});
            skLineSegment(sketch, "E421", {"start": v(-49.58, 3.13) * mm, "end": v(-49.55, 3.27) * mm});
            skLineSegment(sketch, "E422", {"start": v(-49.55, 3.27) * mm, "end": v(-49.66, 3.27) * mm});
            skLineSegment(sketch, "E423", {"start": v(-49.66, 3.27) * mm, "end": v(-49.97, 3.27) * mm});
            skLineSegment(sketch, "E424", {"start": v(-49.97, 3.27) * mm, "end": v(-50.42, 3.27) * mm});
            skLineSegment(sketch, "E425", {"start": v(-50.42, 3.27) * mm, "end": v(-50.96, 3.27) * mm});
            skLineSegment(sketch, "E426", {"start": v(-50.96, 3.27) * mm, "end": v(-51.55, 3.27) * mm});
            skLineSegment(sketch, "E427", {"start": v(-51.55, 3.27) * mm, "end": v(-52.14, 3.27) * mm});
            skLineSegment(sketch, "E428", {"start": v(-52.14, 3.27) * mm, "end": v(-52.67, 3.27) * mm});
            skLineSegment(sketch, "E429", {"start": v(-52.67, 3.27) * mm, "end": v(-53.1, 3.27) * mm});
            skLineSegment(sketch, "E430", {"start": v(-53.1, 3.27) * mm, "end": v(-53.55, 3.2) * mm});
            skLineSegment(sketch, "E431", {"start": v(-53.55, 3.2) * mm, "end": v(-53.9, 3.05) * mm});
            skLineSegment(sketch, "E432", {"start": v(-53.9, 3.05) * mm, "end": v(-54.16, 2.81) * mm});
            skLineSegment(sketch, "E433", {"start": v(-54.16, 2.81) * mm, "end": v(-54.34, 2.53) * mm});
            skLineSegment(sketch, "E434", {"start": v(-54.34, 2.53) * mm, "end": v(-54.46, 2.22) * mm});
            skLineSegment(sketch, "E435", {"start": v(-54.46, 2.22) * mm, "end": v(-54.54, 1.92) * mm});
            skLineSegment(sketch, "E436", {"start": v(-54.54, 1.92) * mm, "end": v(-54.6, 1.65) * mm});
            skLineSegment(sketch, "E437", {"start": v(-54.6, 1.65) * mm, "end": v(-54.63, 1.44) * mm});
            skLineSegment(sketch, "E438", {"start": v(-54.63, 1.44) * mm, "end": v(-54.68, 1.17) * mm});
            skLineSegment(sketch, "E439", {"start": v(-54.68, 1.17) * mm, "end": v(-54.77, 0.74) * mm});
            skLineSegment(sketch, "E440", {"start": v(-54.77, 0.74) * mm, "end": v(-54.89, 0.2) * mm});
            skLineSegment(sketch, "E441", {"start": v(-54.89, 0.2) * mm, "end": v(-55, -0.39) * mm});
            skLineSegment(sketch, "E442", {"start": v(-55, -0.39) * mm, "end": v(-55.13, -0.96) * mm});
            skLineSegment(sketch, "E443", {"start": v(-55.13, -0.96) * mm, "end": v(-55.23, -1.45) * mm});
            skLineSegment(sketch, "E444", {"start": v(-55.23, -1.45) * mm, "end": v(-55.3, -1.8) * mm});
            skLineSegment(sketch, "E445", {"start": v(-55.3, -1.8) * mm, "end": v(-55.34, -1.97) * mm});
            skLineSegment(sketch, "E446", {"start": v(-55.34, -1.97) * mm, "end": v(-55.38, -2.28) * mm});
            skLineSegment(sketch, "E447", {"start": v(-55.38, -2.28) * mm, "end": v(-55.35, -2.57) * mm});
            skLineSegment(sketch, "E448", {"start": v(-55.35, -2.57) * mm, "end": v(-55.27, -2.85) * mm});
            skLineSegment(sketch, "E449", {"start": v(-55.27, -2.85) * mm, "end": v(-55.13, -3.1) * mm});
            skLineSegment(sketch, "E450", {"start": v(-55.13, -3.1) * mm, "end": v(-54.93, -3.32) * mm});
            skLineSegment(sketch, "E451", {"start": v(-54.93, -3.32) * mm, "end": v(-54.66, -3.49) * mm});
            skLineSegment(sketch, "E452", {"start": v(-54.66, -3.49) * mm, "end": v(-54.33, -3.6) * mm});
            skLineSegment(sketch, "E453", {"start": v(-54.33, -3.6) * mm, "end": v(-53.92, -3.63) * mm});
            skLineSegment(sketch, "E454", {"start": v(-53.92, -3.63) * mm, "end": v(-53.52, -3.63) * mm});
            skLineSegment(sketch, "E455", {"start": v(-53.52, -3.63) * mm, "end": v(-53.11, -3.63) * mm});
            skLineSegment(sketch, "E456", {"start": v(-53.11, -3.63) * mm, "end": v(-52.7, -3.63) * mm});
            skLineSegment(sketch, "E457", {"start": v(-52.7, -3.63) * mm, "end": v(-52.3, -3.63) * mm});
            skLineSegment(sketch, "E458", {"start": v(-52.3, -3.63) * mm, "end": v(-51.9, -3.63) * mm});
            skLineSegment(sketch, "E459", {"start": v(-51.9, -3.63) * mm, "end": v(-51.5, -3.63) * mm});
            skLineSegment(sketch, "E460", {"start": v(-51.5, -3.63) * mm, "end": v(-51.09, -3.63) * mm});
            skLineSegment(sketch, "E461", {"start": v(-51.09, -3.63) * mm, "end": v(-50.68, -3.63) * mm});
            skLineSegment(sketch, "E462", {"start": v(-50.68, -3.63) * mm, "end": v(-50.65, -3.5) * mm});
            skLineSegment(sketch, "E463", {"start": v(-50.65, -3.5) * mm, "end": v(-50.62, -3.35) * mm});
            skLineSegment(sketch, "E464", {"start": v(-50.62, -3.35) * mm, "end": v(-50.6, -3.21) * mm});
            skLineSegment(sketch, "E465", {"start": v(-50.6, -3.21) * mm, "end": v(-50.56, -3.07) * mm});
            skLineSegment(sketch, "E466", {"start": v(-50.56, -3.07) * mm, "end": v(-50.53, -2.94) * mm});
            skLineSegment(sketch, "E467", {"start": v(-50.53, -2.94) * mm, "end": v(-50.5, -2.8) * mm});
            skLineSegment(sketch, "E468", {"start": v(-50.5, -2.8) * mm, "end": v(-50.47, -2.66) * mm});
            skLineSegment(sketch, "E469", {"start": v(-50.47, -2.66) * mm, "end": v(-50.44, -2.52) * mm});
            skLineSegment(sketch, "E470", {"start": v(-50.44, -2.52) * mm, "end": v(-50.81, -2.52) * mm});
            skLineSegment(sketch, "E471", {"start": v(-50.81, -2.52) * mm, "end": v(-51.18, -2.52) * mm});
            skLineSegment(sketch, "E472", {"start": v(-51.18, -2.52) * mm, "end": v(-51.56, -2.52) * mm});
            skLineSegment(sketch, "E473", {"start": v(-51.56, -2.52) * mm, "end": v(-51.93, -2.52) * mm});
            skLineSegment(sketch, "E474", {"start": v(-51.93, -2.52) * mm, "end": v(-52.3, -2.52) * mm});
            skLineSegment(sketch, "E475", {"start": v(-52.3, -2.52) * mm, "end": v(-52.67, -2.52) * mm});
            skLineSegment(sketch, "E476", {"start": v(-52.67, -2.52) * mm, "end": v(-53.05, -2.52) * mm});
            skLineSegment(sketch, "E477", {"start": v(-53.05, -2.52) * mm, "end": v(-53.42, -2.52) * mm});
            skLineSegment(sketch, "E478", {"start": v(-53.42, -2.52) * mm, "end": v(-53.6, -2.5) * mm});
            skLineSegment(sketch, "E479", {"start": v(-53.6, -2.5) * mm, "end": v(-53.75, -2.46) * mm});
            skLineSegment(sketch, "E480", {"start": v(-53.75, -2.46) * mm, "end": v(-53.85, -2.38) * mm});
            skLineSegment(sketch, "E481", {"start": v(-53.85, -2.38) * mm, "end": v(-53.92, -2.28) * mm});
            skLineSegment(sketch, "E482", {"start": v(-53.92, -2.28) * mm, "end": v(-53.95, -2.16) * mm});
            skLineSegment(sketch, "E483", {"start": v(-53.95, -2.16) * mm, "end": v(-53.96, -2.03) * mm});
            skLineSegment(sketch, "E484", {"start": v(-53.96, -2.03) * mm, "end": v(-53.95, -1.88) * mm});
            skLineSegment(sketch, "E485", {"start": v(-53.95, -1.88) * mm, "end": v(-53.92, -1.71) * mm});
            skLineSegment(sketch, "E486", {"start": v(-53.92, -1.71) * mm, "end": v(-53.89, -1.5) * mm});
            skLineSegment(sketch, "E487", {"start": v(-53.89, -1.5) * mm, "end": v(-53.85, -1.3) * mm});
            skLineSegment(sketch, "E488", {"start": v(-53.85, -1.3) * mm, "end": v(-53.81, -1.1) * mm});
            skLineSegment(sketch, "E489", {"start": v(-53.81, -1.1) * mm, "end": v(-53.78, -0.9) * mm});
            skLineSegment(sketch, "E490", {"start": v(-53.78, -0.9) * mm, "end": v(-53.74, -0.7) * mm});
            skLineSegment(sketch, "E491", {"start": v(-53.74, -0.7) * mm, "end": v(-53.7, -0.5) * mm});
            skLineSegment(sketch, "E492", {"start": v(-53.7, -0.5) * mm, "end": v(-53.67, -0.29) * mm});
            skLineSegment(sketch, "E493", {"start": v(-53.67, -0.29) * mm, "end": v(-53.63, -0.08) * mm});
            skLineSegment(sketch, "E494", {"start": v(-53.63, -0.08) * mm, "end": v(-53.63, -0.08) * mm});
            skLineSegment(sketch, "E495", {"start": v(-53.63, -0.08) * mm, "end": v(-53.62, -0.04) * mm});
            skLineSegment(sketch, "E496", {"start": v(-53.62, -0.04) * mm, "end": v(-53.6, 0.08) * mm});
            skLineSegment(sketch, "E497", {"start": v(-53.6, 0.08) * mm, "end": v(-53.57, 0.26) * mm});
            skLineSegment(sketch, "E498", {"start": v(-53.57, 0.26) * mm, "end": v(-53.53, 0.5) * mm});
            skLineSegment(sketch, "E499", {"start": v(-53.53, 0.5) * mm, "end": v(-53.48, 0.75) * mm});
            skLineSegment(sketch, "E500", {"start": v(-53.48, 0.75) * mm, "end": v(-53.43, 1.03) * mm});
            skLineSegment(sketch, "E501", {"start": v(-53.43, 1.03) * mm, "end": v(-53.38, 1.3) * mm});
            skLineSegment(sketch, "E502", {"start": v(-53.38, 1.3) * mm, "end": v(-53.33, 1.55) * mm});
            skLineSegment(sketch, "E503", {"start": v(-55.56, 3.27) * mm, "end": v(-55.75, 3.27) * mm});
            skLineSegment(sketch, "E504", {"start": v(-55.75, 3.27) * mm, "end": v(-55.93, 3.27) * mm});
            skLineSegment(sketch, "E505", {"start": v(-55.93, 3.27) * mm, "end": v(-56.12, 3.27) * mm});
            skLineSegment(sketch, "E506", {"start": v(-56.12, 3.27) * mm, "end": v(-56.31, 3.27) * mm});
            skLineSegment(sketch, "E507", {"start": v(-56.31, 3.27) * mm, "end": v(-56.5, 3.27) * mm});
            skLineSegment(sketch, "E508", {"start": v(-56.5, 3.27) * mm, "end": v(-56.69, 3.27) * mm});
            skLineSegment(sketch, "E509", {"start": v(-56.69, 3.27) * mm, "end": v(-56.88, 3.27) * mm});
            skLineSegment(sketch, "E510", {"start": v(-56.88, 3.27) * mm, "end": v(-57.06, 3.27) * mm});
            skLineSegment(sketch, "E511", {"start": v(-57.06, 3.27) * mm, "end": v(-57.25, 2.4) * mm});
            skLineSegment(sketch, "E512", {"start": v(-57.25, 2.4) * mm, "end": v(-57.43, 1.55) * mm});
            skLineSegment(sketch, "E513", {"start": v(-57.43, 1.55) * mm, "end": v(-57.6, 0.68) * mm});
            skLineSegment(sketch, "E514", {"start": v(-57.6, 0.68) * mm, "end": v(-57.8, -0.18) * mm});
            skLineSegment(sketch, "E515", {"start": v(-57.8, -0.18) * mm, "end": v(-57.97, -1.04) * mm});
            skLineSegment(sketch, "E516", {"start": v(-57.97, -1.04) * mm, "end": v(-58.15, -1.9) * mm});
            skLineSegment(sketch, "E517", {"start": v(-58.15, -1.9) * mm, "end": v(-58.33, -2.76) * mm});
            skLineSegment(sketch, "E518", {"start": v(-58.33, -2.76) * mm, "end": v(-58.52, -3.63) * mm});
            skLineSegment(sketch, "E519", {"start": v(-58.52, -3.63) * mm, "end": v(-58.32, -3.63) * mm});
            skLineSegment(sketch, "E520", {"start": v(-58.32, -3.63) * mm, "end": v(-58.13, -3.63) * mm});
            skLineSegment(sketch, "E521", {"start": v(-58.13, -3.63) * mm, "end": v(-57.94, -3.63) * mm});
            skLineSegment(sketch, "E522", {"start": v(-57.94, -3.63) * mm, "end": v(-57.75, -3.63) * mm});
            skLineSegment(sketch, "E523", {"start": v(-57.75, -3.63) * mm, "end": v(-57.56, -3.63) * mm});
            skLineSegment(sketch, "E524", {"start": v(-57.56, -3.63) * mm, "end": v(-57.37, -3.63) * mm});
            skLineSegment(sketch, "E525", {"start": v(-57.37, -3.63) * mm, "end": v(-57.17, -3.63) * mm});
            skLineSegment(sketch, "E526", {"start": v(-57.17, -3.63) * mm, "end": v(-56.98, -3.63) * mm});
            skLineSegment(sketch, "E527", {"start": v(-56.98, -3.63) * mm, "end": v(-56.8, -2.76) * mm});
            skLineSegment(sketch, "E528", {"start": v(-56.8, -2.76) * mm, "end": v(-56.63, -1.9) * mm});
            skLineSegment(sketch, "E529", {"start": v(-56.63, -1.9) * mm, "end": v(-56.45, -1.04) * mm});
            skLineSegment(sketch, "E530", {"start": v(-56.45, -1.04) * mm, "end": v(-56.27, -0.18) * mm});
            skLineSegment(sketch, "E531", {"start": v(-56.27, -0.18) * mm, "end": v(-56.1, 0.68) * mm});
            skLineSegment(sketch, "E532", {"start": v(-56.1, 0.68) * mm, "end": v(-55.91, 1.55) * mm});
            skLineSegment(sketch, "E533", {"start": v(-55.91, 1.55) * mm, "end": v(-55.74, 2.4) * mm});
            skLineSegment(sketch, "E534", {"start": v(-55.74, 2.4) * mm, "end": v(-55.56, 3.27) * mm});
            skLineSegment(sketch, "E535", {"start": v(-61, 1.38) * mm, "end": v(-61.07, 1.26) * mm});
            skLineSegment(sketch, "E536", {"start": v(-61.07, 1.26) * mm, "end": v(-61.23, 0.98) * mm});
            skLineSegment(sketch, "E537", {"start": v(-61.23, 0.98) * mm, "end": v(-61.46, 0.58) * mm});
            skLineSegment(sketch, "E538", {"start": v(-61.46, 0.58) * mm, "end": v(-61.73, 0.13) * mm});
            skLineSegment(sketch, "E539", {"start": v(-61.73, 0.13) * mm, "end": v(-62, -0.33) * mm});
            skLineSegment(sketch, "E540", {"start": v(-62, -0.33) * mm, "end": v(-62.24, -0.75) * mm});
            skLineSegment(sketch, "E541", {"start": v(-62.24, -0.75) * mm, "end": v(-62.42, -1.07) * mm});
            skLineSegment(sketch, "E542", {"start": v(-62.42, -1.07) * mm, "end": v(-62.52, -1.24) * mm});
            skLineSegment(sketch, "E543", {"start": v(-62.52, -1.24) * mm, "end": v(-62.52, -1.24) * mm});
            skLineSegment(sketch, "E544", {"start": v(-62.52, -1.24) * mm, "end": v(-62.45, -1.24) * mm});
            skLineSegment(sketch, "E545", {"start": v(-62.45, -1.24) * mm, "end": v(-62.4, -1.24) * mm});
            skLineSegment(sketch, "E546", {"start": v(-62.4, -1.24) * mm, "end": v(-62.36, -1.24) * mm});
            skLineSegment(sketch, "E547", {"start": v(-62.36, -1.24) * mm, "end": v(-62.26, -1.24) * mm});
            skLineSegment(sketch, "E548", {"start": v(-62.26, -1.24) * mm, "end": v(-62.1, -1.24) * mm});
            skLineSegment(sketch, "E549", {"start": v(-62.1, -1.24) * mm, "end": v(-61.8, -1.24) * mm});
            skLineSegment(sketch, "E550", {"start": v(-61.8, -1.24) * mm, "end": v(-60.78, -1.24) * mm});
            skLineSegment(sketch, "E551", {"start": v(-61.98, -2.26) * mm, "end": v(-62.36, -2.26) * mm});
            skLineSegment(sketch, "E552", {"start": v(-62.36, -2.26) * mm, "end": v(-62.7, -2.26) * mm});
            skLineSegment(sketch, "E553", {"start": v(-62.7, -2.26) * mm, "end": v(-62.94, -2.26) * mm});
            skLineSegment(sketch, "E554", {"start": v(-62.94, -2.26) * mm, "end": v(-63.05, -2.26) * mm});
            skLineSegment(sketch, "E555", {"start": v(-63.05, -2.26) * mm, "end": v(-63.1, -2.34) * mm});
            skLineSegment(sketch, "E556", {"start": v(-63.1, -2.34) * mm, "end": v(-63.18, -2.5) * mm});
            skLineSegment(sketch, "E557", {"start": v(-63.18, -2.5) * mm, "end": v(-63.3, -2.72) * mm});
            skLineSegment(sketch, "E558", {"start": v(-63.3, -2.72) * mm, "end": v(-63.44, -2.97) * mm});
            skLineSegment(sketch, "E559", {"start": v(-63.44, -2.97) * mm, "end": v(-63.58, -3.21) * mm});
            skLineSegment(sketch, "E560", {"start": v(-63.58, -3.21) * mm, "end": v(-63.7, -3.42) * mm});
            skLineSegment(sketch, "E561", {"start": v(-63.7, -3.42) * mm, "end": v(-63.78, -3.57) * mm});
            skLineSegment(sketch, "E562", {"start": v(-63.78, -3.57) * mm, "end": v(-63.8, -3.63) * mm});
            skLineSegment(sketch, "E563", {"start": v(-63.8, -3.63) * mm, "end": v(-63.99, -3.63) * mm});
            skLineSegment(sketch, "E564", {"start": v(-63.99, -3.63) * mm, "end": v(-64.17, -3.63) * mm});
            skLineSegment(sketch, "E565", {"start": v(-64.17, -3.63) * mm, "end": v(-64.35, -3.63) * mm});
            skLineSegment(sketch, "E566", {"start": v(-64.35, -3.63) * mm, "end": v(-64.53, -3.63) * mm});
            skLineSegment(sketch, "E567", {"start": v(-64.53, -3.63) * mm, "end": v(-64.7, -3.63) * mm});
            skLineSegment(sketch, "E568", {"start": v(-64.7, -3.63) * mm, "end": v(-64.89, -3.63) * mm});
            skLineSegment(sketch, "E569", {"start": v(-64.89, -3.63) * mm, "end": v(-65.07, -3.63) * mm});
            skLineSegment(sketch, "E570", {"start": v(-65.07, -3.63) * mm, "end": v(-65.25, -3.63) * mm});
            skLineSegment(sketch, "E571", {"start": v(-65.25, -3.63) * mm, "end": v(-64.78, -2.76) * mm});
            skLineSegment(sketch, "E572", {"start": v(-64.78, -2.76) * mm, "end": v(-64.3, -1.9) * mm});
            skLineSegment(sketch, "E573", {"start": v(-64.3, -1.9) * mm, "end": v(-63.83, -1.04) * mm});
            skLineSegment(sketch, "E574", {"start": v(-63.83, -1.04) * mm, "end": v(-63.35, -0.18) * mm});
            skLineSegment(sketch, "E575", {"start": v(-63.35, -0.18) * mm, "end": v(-62.88, 0.68) * mm});
            skLineSegment(sketch, "E576", {"start": v(-62.88, 0.68) * mm, "end": v(-62.4, 1.54) * mm});
            skLineSegment(sketch, "E577", {"start": v(-62.4, 1.54) * mm, "end": v(-61.93, 2.4) * mm});
            skLineSegment(sketch, "E578", {"start": v(-61.93, 2.4) * mm, "end": v(-61.45, 3.26) * mm});
            skLineSegment(sketch, "E579", {"start": v(-61.45, 3.26) * mm, "end": v(-61.26, 3.26) * mm});
            skLineSegment(sketch, "E580", {"start": v(-61.26, 3.26) * mm, "end": v(-61.08, 3.26) * mm});
            skLineSegment(sketch, "E581", {"start": v(-61.08, 3.26) * mm, "end": v(-60.89, 3.26) * mm});
            skLineSegment(sketch, "E582", {"start": v(-60.89, 3.26) * mm, "end": v(-60.7, 3.26) * mm});
            skLineSegment(sketch, "E583", {"start": v(-60.7, 3.26) * mm, "end": v(-60.51, 3.26) * mm});
            skLineSegment(sketch, "E584", {"start": v(-60.51, 3.26) * mm, "end": v(-60.32, 3.26) * mm});
            skLineSegment(sketch, "E585", {"start": v(-60.32, 3.26) * mm, "end": v(-60.13, 3.26) * mm});
            skLineSegment(sketch, "E586", {"start": v(-60.13, 3.26) * mm, "end": v(-59.95, 3.26) * mm});
            skLineSegment(sketch, "E587", {"start": v(-59.95, 3.26) * mm, "end": v(-59.84, 2.4) * mm});
            skLineSegment(sketch, "E588", {"start": v(-59.84, 2.4) * mm, "end": v(-59.74, 1.54) * mm});
            skLineSegment(sketch, "E589", {"start": v(-59.74, 1.54) * mm, "end": v(-59.64, 0.68) * mm});
            skLineSegment(sketch, "E590", {"start": v(-59.64, 0.68) * mm, "end": v(-59.53, -0.18) * mm});
            skLineSegment(sketch, "E591", {"start": v(-59.53, -0.18) * mm, "end": v(-59.43, -1.04) * mm});
            skLineSegment(sketch, "E592", {"start": v(-59.43, -1.04) * mm, "end": v(-59.33, -1.9) * mm});
            skLineSegment(sketch, "E593", {"start": v(-59.33, -1.9) * mm, "end": v(-59.22, -2.76) * mm});
            skLineSegment(sketch, "E594", {"start": v(-59.22, -2.76) * mm, "end": v(-59.12, -3.63) * mm});
            skLineSegment(sketch, "E595", {"start": v(-59.12, -3.63) * mm, "end": v(-59.29, -3.63) * mm});
            skLineSegment(sketch, "E596", {"start": v(-59.29, -3.63) * mm, "end": v(-59.45, -3.63) * mm});
            skLineSegment(sketch, "E597", {"start": v(-59.45, -3.63) * mm, "end": v(-59.62, -3.63) * mm});
            skLineSegment(sketch, "E598", {"start": v(-59.62, -3.63) * mm, "end": v(-59.8, -3.63) * mm});
            skLineSegment(sketch, "E599", {"start": v(-59.8, -3.63) * mm, "end": v(-59.96, -3.63) * mm});
            skLineSegment(sketch, "E600", {"start": v(-59.96, -3.63) * mm, "end": v(-60.13, -3.63) * mm});
            skLineSegment(sketch, "E601", {"start": v(-60.13, -3.63) * mm, "end": v(-60.3, -3.63) * mm});
            skLineSegment(sketch, "E602", {"start": v(-60.3, -3.63) * mm, "end": v(-60.46, -3.63) * mm});
            skLineSegment(sketch, "E603", {"start": v(-60.46, -3.63) * mm, "end": v(-60.49, -3.41) * mm});
            skLineSegment(sketch, "E604", {"start": v(-60.49, -3.41) * mm, "end": v(-60.55, -2.85) * mm});
            skLineSegment(sketch, "E605", {"start": v(-60.55, -2.85) * mm, "end": v(-60.63, -2.05) * mm});
            skLineSegment(sketch, "E606", {"start": v(-60.63, -2.05) * mm, "end": v(-60.73, -1.14) * mm});
            skLineSegment(sketch, "E607", {"start": v(-60.73, -1.14) * mm, "end": v(-60.83, -0.22) * mm});
            skLineSegment(sketch, "E608", {"start": v(-60.83, -0.22) * mm, "end": v(-60.91, 0.58) * mm});
            skLineSegment(sketch, "E609", {"start": v(-60.91, 0.58) * mm, "end": v(-60.98, 1.15) * mm});
            skLineSegment(sketch, "E610", {"start": v(-60.98, 1.15) * mm, "end": v(-61, 1.38) * mm});
            skLineSegment(sketch, "E611", {"start": v(-68.24, 1.53) * mm, "end": v(-68.2, 1.7) * mm});
            skLineSegment(sketch, "E612", {"start": v(-68.2, 1.7) * mm, "end": v(-68.18, 1.83) * mm});
            skLineSegment(sketch, "E613", {"start": v(-68.18, 1.83) * mm, "end": v(-68.15, 1.94) * mm});
            skLineSegment(sketch, "E614", {"start": v(-68.15, 1.94) * mm, "end": v(-68.1, 2.03) * mm});
            skLineSegment(sketch, "E615", {"start": v(-68.1, 2.03) * mm, "end": v(-68.03, 2.1) * mm});
            skLineSegment(sketch, "E616", {"start": v(-68.03, 2.1) * mm, "end": v(-67.92, 2.13) * mm});
            skLineSegment(sketch, "E617", {"start": v(-67.92, 2.13) * mm, "end": v(-67.76, 2.16) * mm});
            skLineSegment(sketch, "E618", {"start": v(-67.76, 2.16) * mm, "end": v(-67.54, 2.17) * mm});
            skLineSegment(sketch, "E619", {"start": v(-67.54, 2.17) * mm, "end": v(-67.17, 2.16) * mm});
            skLineSegment(sketch, "E620", {"start": v(-67.17, 2.16) * mm, "end": v(-66.74, 2.16) * mm});
            skLineSegment(sketch, "E621", {"start": v(-66.74, 2.16) * mm, "end": v(-66.28, 2.16) * mm});
            skLineSegment(sketch, "E622", {"start": v(-66.28, 2.16) * mm, "end": v(-65.83, 2.16) * mm});
            skLineSegment(sketch, "E623", {"start": v(-65.83, 2.16) * mm, "end": v(-65.42, 2.16) * mm});
            skLineSegment(sketch, "E624", {"start": v(-65.42, 2.16) * mm, "end": v(-65.08, 2.16) * mm});
            skLineSegment(sketch, "E625", {"start": v(-65.08, 2.16) * mm, "end": v(-64.85, 2.16) * mm});
            skLineSegment(sketch, "E626", {"start": v(-64.85, 2.16) * mm, "end": v(-64.77, 2.16) * mm});
            skLineSegment(sketch, "E627", {"start": v(-64.77, 2.16) * mm, "end": v(-64.74, 2.3) * mm});
            skLineSegment(sketch, "E628", {"start": v(-64.74, 2.3) * mm, "end": v(-64.7, 2.44) * mm});
            skLineSegment(sketch, "E629", {"start": v(-64.7, 2.44) * mm, "end": v(-64.67, 2.58) * mm});
            skLineSegment(sketch, "E630", {"start": v(-64.67, 2.58) * mm, "end": v(-64.64, 2.72) * mm});
            skLineSegment(sketch, "E631", {"start": v(-64.64, 2.72) * mm, "end": v(-64.6, 2.85) * mm});
            skLineSegment(sketch, "E632", {"start": v(-64.6, 2.85) * mm, "end": v(-64.57, 3) * mm});
            skLineSegment(sketch, "E633", {"start": v(-64.57, 3) * mm, "end": v(-64.54, 3.13) * mm});
            skLineSegment(sketch, "E634", {"start": v(-64.54, 3.13) * mm, "end": v(-64.5, 3.27) * mm});
            skLineSegment(sketch, "E635", {"start": v(-64.5, 3.27) * mm, "end": v(-64.6, 3.27) * mm});
            skLineSegment(sketch, "E636", {"start": v(-64.6, 3.27) * mm, "end": v(-64.85, 3.27) * mm});
            skLineSegment(sketch, "E637", {"start": v(-64.85, 3.27) * mm, "end": v(-65.23, 3.27) * mm});
            skLineSegment(sketch, "E638", {"start": v(-65.23, 3.27) * mm, "end": v(-65.7, 3.27) * mm});
            skLineSegment(sketch, "E639", {"start": v(-65.7, 3.27) * mm, "end": v(-66.24, 3.27) * mm});
            skLineSegment(sketch, "E640", {"start": v(-66.24, 3.27) * mm, "end": v(-66.8, 3.27) * mm});
            skLineSegment(sketch, "E641", {"start": v(-66.8, 3.27) * mm, "end": v(-67.36, 3.27) * mm});
            skLineSegment(sketch, "E642", {"start": v(-67.36, 3.27) * mm, "end": v(-67.87, 3.27) * mm});
            skLineSegment(sketch, "E643", {"start": v(-67.87, 3.27) * mm, "end": v(-68.05, 3.27) * mm});
            skLineSegment(sketch, "E644", {"start": v(-68.05, 3.27) * mm, "end": v(-68.28, 3.26) * mm});
            skLineSegment(sketch, "E645", {"start": v(-68.28, 3.26) * mm, "end": v(-68.52, 3.22) * mm});
            skLineSegment(sketch, "E646", {"start": v(-68.52, 3.22) * mm, "end": v(-68.76, 3.11) * mm});
            skLineSegment(sketch, "E647", {"start": v(-68.76, 3.11) * mm, "end": v(-69, 2.93) * mm});
            skLineSegment(sketch, "E648", {"start": v(-69, 2.93) * mm, "end": v(-69.22, 2.64) * mm});
            skLineSegment(sketch, "E649", {"start": v(-69.22, 2.64) * mm, "end": v(-69.4, 2.21) * mm});
            skLineSegment(sketch, "E650", {"start": v(-69.4, 2.21) * mm, "end": v(-69.53, 1.63) * mm});
            skLineSegment(sketch, "E651", {"start": v(-69.53, 1.63) * mm, "end": v(-69.57, 1.37) * mm});
            skLineSegment(sketch, "E652", {"start": v(-69.57, 1.37) * mm, "end": v(-69.6, 1.13) * mm});
            skLineSegment(sketch, "E653", {"start": v(-69.6, 1.13) * mm, "end": v(-69.63, 0.93) * mm});
            skLineSegment(sketch, "E654", {"start": v(-69.63, 0.93) * mm, "end": v(-69.66, 0.75) * mm});
            skLineSegment(sketch, "E655", {"start": v(-69.66, 0.75) * mm, "end": v(-69.68, 0.6) * mm});
            skLineSegment(sketch, "E656", {"start": v(-69.68, 0.6) * mm, "end": v(-69.7, 0.47) * mm});
            skLineSegment(sketch, "E657", {"start": v(-69.7, 0.47) * mm, "end": v(-69.71, 0.35) * mm});
            skLineSegment(sketch, "E658", {"start": v(-69.71, 0.35) * mm, "end": v(-69.72, 0.25) * mm});
            skLineSegment(sketch, "E659", {"start": v(-69.72, 0.25) * mm, "end": v(-69.7, 0.04) * mm});
            skLineSegment(sketch, "E660", {"start": v(-69.7, 0.04) * mm, "end": v(-69.65, -0.13) * mm});
            skLineSegment(sketch, "E661", {"start": v(-69.65, -0.13) * mm, "end": v(-69.55, -0.27) * mm});
            skLineSegment(sketch, "E662", {"start": v(-69.55, -0.27) * mm, "end": v(-69.43, -0.38) * mm});
            skLineSegment(sketch, "E663", {"start": v(-69.43, -0.38) * mm, "end": v(-69.27, -0.46) * mm});
            skLineSegment(sketch, "E664", {"start": v(-69.27, -0.46) * mm, "end": v(-69.1, -0.51) * mm});
            skLineSegment(sketch, "E665", {"start": v(-69.1, -0.51) * mm, "end": v(-68.93, -0.54) * mm});
            skLineSegment(sketch, "E666", {"start": v(-68.93, -0.54) * mm, "end": v(-68.76, -0.55) * mm});
            skLineSegment(sketch, "E667", {"start": v(-68.76, -0.55) * mm, "end": v(-68.5, -0.55) * mm});
            skLineSegment(sketch, "E668", {"start": v(-68.5, -0.55) * mm, "end": v(-68.18, -0.55) * mm});
            skLineSegment(sketch, "E669", {"start": v(-68.18, -0.55) * mm, "end": v(-67.85, -0.55) * mm});
            skLineSegment(sketch, "E670", {"start": v(-67.85, -0.55) * mm, "end": v(-67.53, -0.55) * mm});
            skLineSegment(sketch, "E671", {"start": v(-67.53, -0.55) * mm, "end": v(-67.23, -0.55) * mm});
            skLineSegment(sketch, "E672", {"start": v(-67.23, -0.55) * mm, "end": v(-66.99, -0.55) * mm});
            skLineSegment(sketch, "E673", {"start": v(-66.99, -0.55) * mm, "end": v(-66.82, -0.56) * mm});
            skLineSegment(sketch, "E674", {"start": v(-66.82, -0.56) * mm, "end": v(-66.76, -0.56) * mm});
            skLineSegment(sketch, "E675", {"start": v(-66.76, -0.56) * mm, "end": v(-66.66, -0.56) * mm});
            skLineSegment(sketch, "E676", {"start": v(-66.66, -0.56) * mm, "end": v(-66.57, -0.56) * mm});
            skLineSegment(sketch, "E677", {"start": v(-66.57, -0.56) * mm, "end": v(-66.5, -0.57) * mm});
            skLineSegment(sketch, "E678", {"start": v(-66.5, -0.57) * mm, "end": v(-66.44, -0.58) * mm});
            skLineSegment(sketch, "E679", {"start": v(-66.44, -0.58) * mm, "end": v(-66.4, -0.6) * mm});
            skLineSegment(sketch, "E680", {"start": v(-66.4, -0.6) * mm, "end": v(-66.38, -0.65) * mm});
            skLineSegment(sketch, "E681", {"start": v(-66.38, -0.65) * mm, "end": v(-66.37, -0.7) * mm});
            skLineSegment(sketch, "E682", {"start": v(-66.37, -0.7) * mm, "end": v(-66.38, -0.78) * mm});
            skLineSegment(sketch, "E683", {"start": v(-66.38, -0.78) * mm, "end": v(-66.41, -0.95) * mm});
            skLineSegment(sketch, "E684", {"start": v(-66.41, -0.95) * mm, "end": v(-66.45, -1.14) * mm});
            skLineSegment(sketch, "E685", {"start": v(-66.45, -1.14) * mm, "end": v(-66.49, -1.35) * mm});
            skLineSegment(sketch, "E686", {"start": v(-66.49, -1.35) * mm, "end": v(-66.53, -1.55) * mm});
            skLineSegment(sketch, "E687", {"start": v(-66.53, -1.55) * mm, "end": v(-66.57, -1.75) * mm});
            skLineSegment(sketch, "E688", {"start": v(-66.57, -1.75) * mm, "end": v(-66.6, -1.94) * mm});
            skLineSegment(sketch, "E689", {"start": v(-66.6, -1.94) * mm, "end": v(-66.64, -2.09) * mm});
            skLineSegment(sketch, "E690", {"start": v(-66.64, -2.09) * mm, "end": v(-66.66, -2.2) * mm});
            skLineSegment(sketch, "E691", {"start": v(-66.66, -2.2) * mm, "end": v(-66.7, -2.32) * mm});
            skLineSegment(sketch, "E692", {"start": v(-66.7, -2.32) * mm, "end": v(-66.78, -2.4) * mm});
            skLineSegment(sketch, "E693", {"start": v(-66.78, -2.4) * mm, "end": v(-66.87, -2.46) * mm});
            skLineSegment(sketch, "E694", {"start": v(-66.87, -2.46) * mm, "end": v(-66.99, -2.5) * mm});
            skLineSegment(sketch, "E695", {"start": v(-66.99, -2.5) * mm, "end": v(-67.12, -2.51) * mm});
            skLineSegment(sketch, "E696", {"start": v(-67.12, -2.51) * mm, "end": v(-67.26, -2.52) * mm});
            skLineSegment(sketch, "E697", {"start": v(-67.26, -2.52) * mm, "end": v(-67.4, -2.52) * mm});
            skLineSegment(sketch, "E698", {"start": v(-67.4, -2.52) * mm, "end": v(-67.54, -2.52) * mm});
            skLineSegment(sketch, "E699", {"start": v(-67.54, -2.52) * mm, "end": v(-67.9, -2.52) * mm});
            skLineSegment(sketch, "E700", {"start": v(-67.9, -2.52) * mm, "end": v(-68.27, -2.52) * mm});
            skLineSegment(sketch, "E701", {"start": v(-68.27, -2.52) * mm, "end": v(-68.63, -2.52) * mm});
            skLineSegment(sketch, "E702", {"start": v(-68.63, -2.52) * mm, "end": v(-68.99, -2.52) * mm});
            skLineSegment(sketch, "E703", {"start": v(-68.99, -2.52) * mm, "end": v(-69.35, -2.52) * mm});
            skLineSegment(sketch, "E704", {"start": v(-69.35, -2.52) * mm, "end": v(-69.71, -2.52) * mm});
            skLineSegment(sketch, "E705", {"start": v(-69.71, -2.52) * mm, "end": v(-70.07, -2.52) * mm});
            skLineSegment(sketch, "E706", {"start": v(-70.07, -2.52) * mm, "end": v(-70.43, -2.52) * mm});
            skLineSegment(sketch, "E707", {"start": v(-70.43, -2.52) * mm, "end": v(-70.46, -2.66) * mm});
            skLineSegment(sketch, "E708", {"start": v(-70.46, -2.66) * mm, "end": v(-70.5, -2.8) * mm});
            skLineSegment(sketch, "E709", {"start": v(-70.5, -2.8) * mm, "end": v(-70.53, -2.93) * mm});
            skLineSegment(sketch, "E710", {"start": v(-70.53, -2.93) * mm, "end": v(-70.56, -3.07) * mm});
            skLineSegment(sketch, "E711", {"start": v(-70.56, -3.07) * mm, "end": v(-70.59, -3.21) * mm});
            skLineSegment(sketch, "E712", {"start": v(-70.59, -3.21) * mm, "end": v(-70.62, -3.35) * mm});
            skLineSegment(sketch, "E713", {"start": v(-70.62, -3.35) * mm, "end": v(-70.65, -3.49) * mm});
            skLineSegment(sketch, "E714", {"start": v(-70.65, -3.49) * mm, "end": v(-70.68, -3.63) * mm});
            skLineSegment(sketch, "E715", {"start": v(-70.68, -3.63) * mm, "end": v(-70.56, -3.63) * mm});
            skLineSegment(sketch, "E716", {"start": v(-70.56, -3.63) * mm, "end": v(-70.23, -3.63) * mm});
            skLineSegment(sketch, "E717", {"start": v(-70.23, -3.63) * mm, "end": v(-69.74, -3.63) * mm});
            skLineSegment(sketch, "E718", {"start": v(-69.74, -3.63) * mm, "end": v(-69.16, -3.63) * mm});
            skLineSegment(sketch, "E719", {"start": v(-69.16, -3.63) * mm, "end": v(-68.55, -3.63) * mm});
            skLineSegment(sketch, "E720", {"start": v(-68.55, -3.63) * mm, "end": v(-67.96, -3.63) * mm});
            skLineSegment(sketch, "E721", {"start": v(-67.96, -3.63) * mm, "end": v(-67.44, -3.63) * mm});
            skLineSegment(sketch, "E722", {"start": v(-67.44, -3.63) * mm, "end": v(-67.07, -3.63) * mm});
            skLineSegment(sketch, "E723", {"start": v(-67.07, -3.63) * mm, "end": v(-66.78, -3.61) * mm});
            skLineSegment(sketch, "E724", {"start": v(-66.78, -3.61) * mm, "end": v(-66.5, -3.57) * mm});
            skLineSegment(sketch, "E725", {"start": v(-66.5, -3.57) * mm, "end": v(-66.25, -3.5) * mm});
            skLineSegment(sketch, "E726", {"start": v(-66.25, -3.5) * mm, "end": v(-66.02, -3.4) * mm});
            skLineSegment(sketch, "E727", {"start": v(-66.02, -3.4) * mm, "end": v(-65.81, -3.25) * mm});
            skLineSegment(sketch, "E728", {"start": v(-65.81, -3.25) * mm, "end": v(-65.64, -3.07) * mm});
            skLineSegment(sketch, "E729", {"start": v(-65.64, -3.07) * mm, "end": v(-65.5, -2.85) * mm});
            skLineSegment(sketch, "E730", {"start": v(-65.5, -2.85) * mm, "end": v(-65.4, -2.58) * mm});
            skLineSegment(sketch, "E731", {"start": v(-65.4, -2.58) * mm, "end": v(-65.34, -2.3) * mm});
            skLineSegment(sketch, "E732", {"start": v(-65.34, -2.3) * mm, "end": v(-65.28, -2.04) * mm});
            skLineSegment(sketch, "E733", {"start": v(-65.28, -2.04) * mm, "end": v(-65.22, -1.8) * mm});
            skLineSegment(sketch, "E734", {"start": v(-65.22, -1.8) * mm, "end": v(-65.17, -1.56) * mm});
            skLineSegment(sketch, "E735", {"start": v(-65.17, -1.56) * mm, "end": v(-65.12, -1.33) * mm});
            skLineSegment(sketch, "E736", {"start": v(-65.12, -1.33) * mm, "end": v(-65.08, -1.1) * mm});
            skLineSegment(sketch, "E737", {"start": v(-65.08, -1.1) * mm, "end": v(-65.04, -0.88) * mm});
            skLineSegment(sketch, "E738", {"start": v(-65.04, -0.88) * mm, "end": v(-65, -0.65) * mm});
            skLineSegment(sketch, "E739", {"start": v(-65, -0.65) * mm, "end": v(-64.97, -0.38) * mm});
            skLineSegment(sketch, "E740", {"start": v(-64.97, -0.38) * mm, "end": v(-65, -0.13) * mm});
            skLineSegment(sketch, "E741", {"start": v(-65, -0.13) * mm, "end": v(-65.08, 0.09) * mm});
            skLineSegment(sketch, "E742", {"start": v(-65.08, 0.09) * mm, "end": v(-65.2, 0.28) * mm});
            skLineSegment(sketch, "E743", {"start": v(-65.2, 0.28) * mm, "end": v(-65.38, 0.43) * mm});
            skLineSegment(sketch, "E744", {"start": v(-65.38, 0.43) * mm, "end": v(-65.6, 0.55) * mm});
            skLineSegment(sketch, "E745", {"start": v(-65.6, 0.55) * mm, "end": v(-65.85, 0.62) * mm});
            skLineSegment(sketch, "E746", {"start": v(-65.85, 0.62) * mm, "end": v(-66.15, 0.64) * mm});
            skLineSegment(sketch, "E747", {"start": v(-66.15, 0.64) * mm, "end": v(-66.26, 0.64) * mm});
            skLineSegment(sketch, "E748", {"start": v(-66.26, 0.64) * mm, "end": v(-66.48, 0.64) * mm});
            skLineSegment(sketch, "E749", {"start": v(-66.48, 0.64) * mm, "end": v(-66.76, 0.64) * mm});
            skLineSegment(sketch, "E750", {"start": v(-66.76, 0.64) * mm, "end": v(-67.08, 0.64) * mm});
            skLineSegment(sketch, "E751", {"start": v(-67.08, 0.64) * mm, "end": v(-67.38, 0.64) * mm});
            skLineSegment(sketch, "E752", {"start": v(-67.38, 0.64) * mm, "end": v(-67.65, 0.64) * mm});
            skLineSegment(sketch, "E753", {"start": v(-67.65, 0.64) * mm, "end": v(-67.83, 0.64) * mm});
            skLineSegment(sketch, "E754", {"start": v(-67.83, 0.64) * mm, "end": v(-67.9, 0.64) * mm});
            skLineSegment(sketch, "E755", {"start": v(-67.9, 0.64) * mm, "end": v(-67.98, 0.64) * mm});
            skLineSegment(sketch, "E756", {"start": v(-67.98, 0.64) * mm, "end": v(-68.06, 0.64) * mm});
            skLineSegment(sketch, "E757", {"start": v(-68.06, 0.64) * mm, "end": v(-68.14, 0.65) * mm});
            skLineSegment(sketch, "E758", {"start": v(-68.14, 0.65) * mm, "end": v(-68.21, 0.66) * mm});
            skLineSegment(sketch, "E759", {"start": v(-68.21, 0.66) * mm, "end": v(-68.28, 0.7) * mm});
            skLineSegment(sketch, "E760", {"start": v(-68.28, 0.7) * mm, "end": v(-68.32, 0.74) * mm});
            skLineSegment(sketch, "E761", {"start": v(-68.32, 0.74) * mm, "end": v(-68.35, 0.82) * mm});
            skLineSegment(sketch, "E762", {"start": v(-68.35, 0.82) * mm, "end": v(-68.34, 0.92) * mm});
            skLineSegment(sketch, "E763", {"start": v(-68.34, 0.92) * mm, "end": v(-68.33, 0.98) * mm});
            skLineSegment(sketch, "E764", {"start": v(-68.33, 0.98) * mm, "end": v(-68.32, 1.03) * mm});
            skLineSegment(sketch, "E765", {"start": v(-68.32, 1.03) * mm, "end": v(-68.31, 1.1) * mm});
            skLineSegment(sketch, "E766", {"start": v(-68.31, 1.1) * mm, "end": v(-68.3, 1.17) * mm});
            skLineSegment(sketch, "E767", {"start": v(-68.3, 1.17) * mm, "end": v(-68.29, 1.24) * mm});
            skLineSegment(sketch, "E768", {"start": v(-68.29, 1.24) * mm, "end": v(-68.27, 1.33) * mm});
            skLineSegment(sketch, "E769", {"start": v(-68.27, 1.33) * mm, "end": v(-68.26, 1.42) * mm});
            skLineSegment(sketch, "E770", {"start": v(-68.26, 1.42) * mm, "end": v(-68.24, 1.53) * mm});
            skLineSegment(sketch, "E771", {"start": v(-60.78, -1.24) * mm, "end": v(-61.13, -2.26) * mm});
            skLineSegment(sketch, "E772", {"start": v(-61.98, -2.26) * mm, "end": v(-61.13, -2.26) * mm});
            skSolve(sketch);
        }
        {
            var Q0;
            Q0 = qSketchRegion(id + "F21", true);
            extrude(context, id + "F22", {"entities" : qUnion([Q0]), "operationType" : NewBodyOperationType.REMOVE, "depth" : 25 * mm, "offsetDistance" : 25 * mm, "hasSecondDirection" : true, "secondDirectionOppositeDirection" : true, "secondDirectionDepth" : -1 * mm});
        }
        {
            var Q0;
            Q0=qCreatedBy(makeId("Top.planeOp"),FACE);
            var sketch = newSketch(context, id + "F23", { "sketchPlane" : qUnion([Q0])});
            skCircle(sketch, "E773", {"center": v(-60.04, 0) * mm, "radius": 1 * mm});
            skCircle(sketch, "E774", {"center": v(-60.04, 0) * mm, "radius": 3 * mm});
            skLineSegment(sketch, "E775.bottom", {"start": v(-59.79, -1.75) * mm, "end": v(-60.29, -1.75) * mm});
            skLineSegment(sketch, "E775.top", {"start": v(-59.79, 1.75) * mm, "end": v(-60.29, 1.75) * mm});
            skLineSegment(sketch, "E775.left", {"start": v(-59.79, -1.75) * mm, "end": v(-59.79, 1.75) * mm});
            skLineSegment(sketch, "E775.right", {"start": v(-60.29, -1.75) * mm, "end": v(-60.29, 1.75) * mm});
            skLineSegment(sketch, "E776.bottom", {"start": v(-58.29, 0.25) * mm, "end": v(-61.79, 0.25) * mm});
            skLineSegment(sketch, "E776.top", {"start": v(-58.29, -0.25) * mm, "end": v(-61.79, -0.25) * mm});
            skLineSegment(sketch, "E776.left", {"start": v(-58.29, 0.25) * mm, "end": v(-58.29, -0.25) * mm});
            skLineSegment(sketch, "E776.right", {"start": v(-61.79, 0.25) * mm, "end": v(-61.79, -0.25) * mm});
            skSolve(sketch);
        }
        {
            var Q0;
            Q0 = qSketchRegion(id + "F23", true);
            extrude(context, id + "F24", {"entities" : qUnion([Q0]), "operationType" : NewBodyOperationType.ADD, "oppositeDirection" : true, "depth" : 7 * mm, "offsetDistance" : 25 * mm});
        }
        {
            var Q0;
            Q0=makeQuery(id+"F24.opExtrude","CAP_EDGE",EDGE,{"disambiguationData":[OSD([sQuery(id+"F23.wireOp",EDGE,"E774")])],"isStart":false});
            var Q1;
            Q1=makeQuery(id+"F20.opExtrude","CAP_EDGE",EDGE,{"disambiguationData":[OSD([sQuery(id+"F19.wireOp",EDGE,"E397")])],"isStart":false});
            var Q2;
            Q2=makeQuery(id+"F20.opExtrude","CAP_EDGE",EDGE,{"disambiguationData":[OSD([sQuery(id+"F19.wireOp",EDGE,"E397")])],"isStart":true});
            chamfer(context, id + "F25", {"entities" : qUnion([Q0, Q1, Q2]), "width" : 0.5 * mm, "tangentPropagation" : true});
        }
    });
